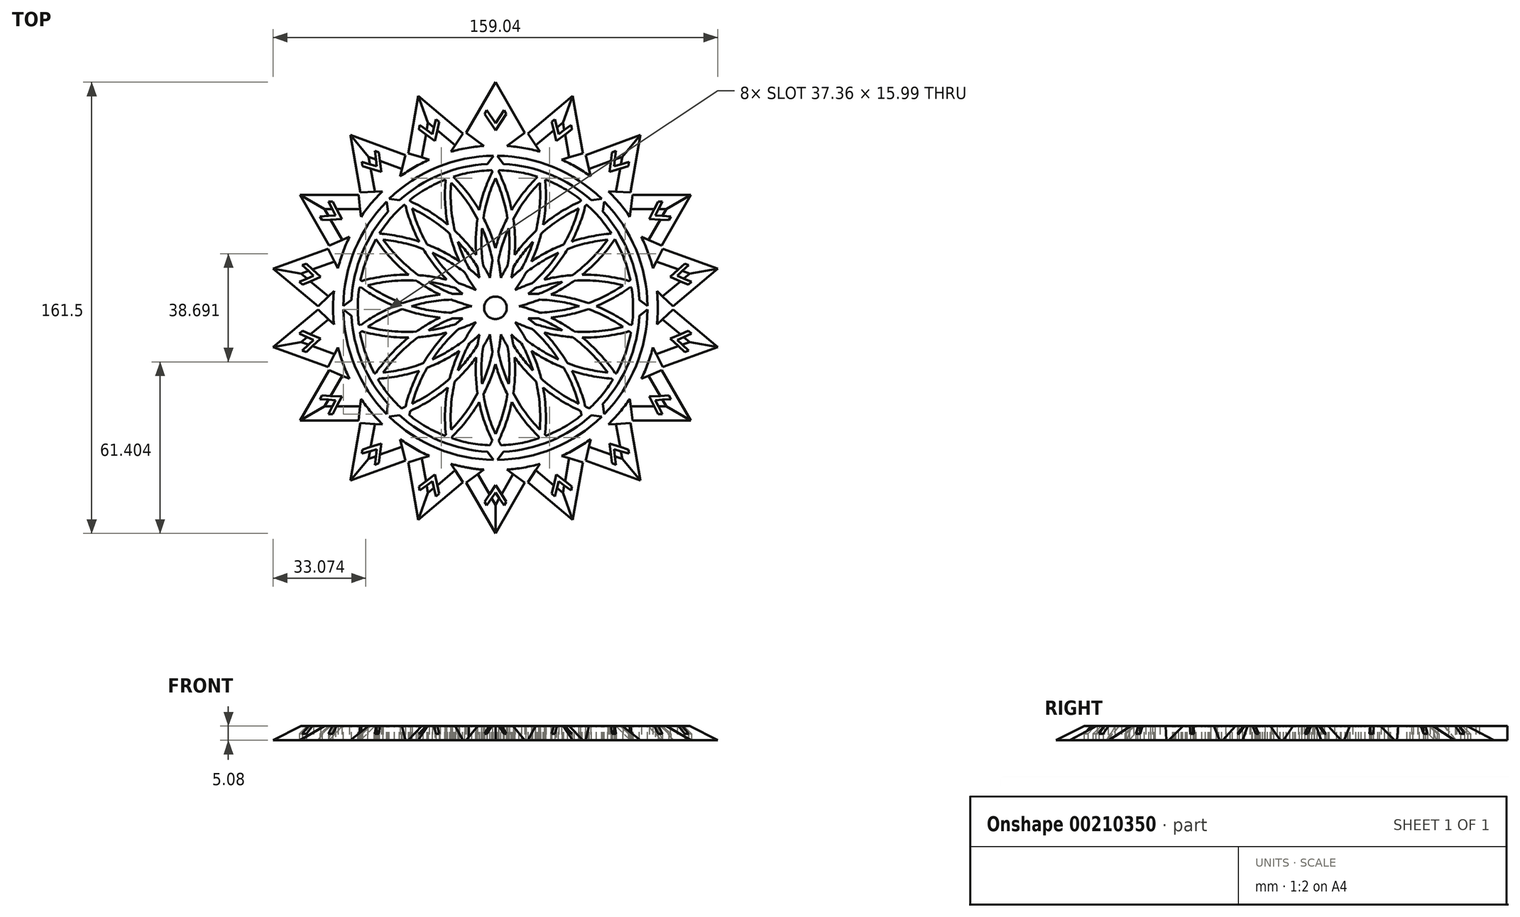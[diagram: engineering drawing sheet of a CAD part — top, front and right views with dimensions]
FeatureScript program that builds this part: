
annotation { "Feature Type Name" : "Feature", "Feature Type Description" : "" }
export const myFeature = defineFeature(function(context is Context, id is Id, definition is map)
    precondition{}
    {
        {
            var Q0;
            Q0=qCreatedBy(makeId("Top.planeOp"),FACE);
            var sketch = newSketch(context, id + "F0", { "sketchPlane" : qUnion([Q0])});
            skLineSegment(sketch, "E0", {"start": v(0, 0) * mm, "end": v(0, 63.5) * mm});
            skLineSegment(sketch, "E1", {"start": v(4.14, 57.94) * mm, "end": v(10.44, 62.64) * mm});
            skLineSegment(sketch, "E2", {"start": v(10.44, 62.64) * mm, "end": v(0, 80.75) * mm});
            skLineSegment(sketch, "E3", {"start": v(0, 80.75) * mm, "end": v(-10.44, 62.64) * mm});
            skLineSegment(sketch, "E4", {"start": v(-10.44, 62.64) * mm, "end": v(-4.14, 57.94) * mm});
            skLineSegment(sketch, "E5", {"start": v(0, 63.5) * mm, "end": v(3.84, 69.42) * mm});
            skLineSegment(sketch, "E6", {"start": v(3.08, 70.74) * mm, "end": v(0, 66.1) * mm});
            skLineSegment(sketch, "E7", {"start": v(0, 66.1) * mm, "end": v(-3.08, 70.74) * mm});
            skLineSegment(sketch, "E8", {"start": v(-3.84, 69.42) * mm, "end": v(0, 63.5) * mm});
            skLineSegment(sketch, "E9", {"start": v(0, 66.1) * mm, "end": v(0, 71.75) * mm});
            skLineSegment(sketch, "E10", {"start": v(-3.08, 70.74) * mm, "end": v(-3.84, 69.42) * mm});
            skLineSegment(sketch, "E11", {"start": v(3.08, 70.74) * mm, "end": v(3.84, 69.42) * mm});
            skLineSegment(sketch, "E12.1.0", {"start": v(31.24, 55.29) * mm, "end": v(27.62, 75.88) * mm});
            skLineSegment(sketch, "E12.1.1", {"start": v(27.62, 75.88) * mm, "end": v(11.6, 62.43) * mm});
            skLineSegment(sketch, "E12.1.2", {"start": v(22.61, 62.12) * mm, "end": v(21.3, 67.53) * mm});
            skLineSegment(sketch, "E12.1.3", {"start": v(21.3, 67.53) * mm, "end": v(20.13, 66.55) * mm});
            skLineSegment(sketch, "E12.1.4", {"start": v(20.13, 66.55) * mm, "end": v(21.72, 59.67) * mm});
            skLineSegment(sketch, "E12.1.5", {"start": v(21.72, 59.67) * mm, "end": v(27.35, 63.92) * mm});
            skLineSegment(sketch, "E12.1.6", {"start": v(27.09, 65.43) * mm, "end": v(27.35, 63.92) * mm});
            skLineSegment(sketch, "E12.1.7", {"start": v(27.09, 65.43) * mm, "end": v(22.61, 62.12) * mm});
            skLineSegment(sketch, "E12.1.10", {"start": v(11.6, 62.43) * mm, "end": v(15.93, 55.86) * mm});
            skLineSegment(sketch, "E12.1.11", {"start": v(23.7, 53.03) * mm, "end": v(31.24, 55.29) * mm});
            skLineSegment(sketch, "E12.2.0", {"start": v(48.26, 41.27) * mm, "end": v(51.9, 61.86) * mm});
            skLineSegment(sketch, "E12.2.1", {"start": v(51.9, 61.86) * mm, "end": v(32.26, 54.7) * mm});
            skLineSegment(sketch, "E12.2.2", {"start": v(42.5, 50.64) * mm, "end": v(43.12, 56.17) * mm});
            skLineSegment(sketch, "E12.2.3", {"start": v(43.12, 56.17) * mm, "end": v(41.68, 55.65) * mm});
            skLineSegment(sketch, "E12.2.4", {"start": v(41.68, 55.65) * mm, "end": v(40.82, 48.64) * mm});
            skLineSegment(sketch, "E12.2.5", {"start": v(40.82, 48.64) * mm, "end": v(47.56, 50.7) * mm});
            skLineSegment(sketch, "E12.2.6", {"start": v(47.83, 52.22) * mm, "end": v(47.56, 50.7) * mm});
            skLineSegment(sketch, "E12.2.7", {"start": v(47.83, 52.22) * mm, "end": v(42.5, 50.64) * mm});
            skLineSegment(sketch, "E12.2.10", {"start": v(32.26, 54.7) * mm, "end": v(34.07, 47.05) * mm});
            skLineSegment(sketch, "E12.2.11", {"start": v(40.41, 41.73) * mm, "end": v(48.26, 41.27) * mm});
            skLineSegment(sketch, "E12.3.0", {"start": v(59.47, 22.27) * mm, "end": v(69.93, 40.37) * mm});
            skLineSegment(sketch, "E12.3.1", {"start": v(69.93, 40.37) * mm, "end": v(49.02, 40.36) * mm});
            skLineSegment(sketch, "E12.3.2", {"start": v(57.25, 33.05) * mm, "end": v(59.73, 38.04) * mm});
            skLineSegment(sketch, "E12.3.3", {"start": v(59.73, 38.04) * mm, "end": v(58.2, 38.04) * mm});
            skLineSegment(sketch, "E12.3.4", {"start": v(58.2, 38.04) * mm, "end": v(55, 31.75) * mm});
            skLineSegment(sketch, "E12.3.5", {"start": v(55, 31.75) * mm, "end": v(62.04, 31.38) * mm});
            skLineSegment(sketch, "E12.3.6", {"start": v(62.8, 32.7) * mm, "end": v(62.04, 31.38) * mm});
            skLineSegment(sketch, "E12.3.7", {"start": v(62.8, 32.7) * mm, "end": v(57.25, 33.05) * mm});
            skLineSegment(sketch, "E12.3.10", {"start": v(49.02, 40.36) * mm, "end": v(48.1, 32.56) * mm});
            skLineSegment(sketch, "E12.3.11", {"start": v(52.25, 25.39) * mm, "end": v(59.47, 22.27) * mm});
            skLineSegment(sketch, "E12.4.0", {"start": v(63.5, 0.6) * mm, "end": v(79.52, 14.02) * mm});
            skLineSegment(sketch, "E12.4.1", {"start": v(79.52, 14.02) * mm, "end": v(59.87, 21.16) * mm});
            skLineSegment(sketch, "E12.4.2", {"start": v(65.1, 11.48) * mm, "end": v(69.14, 15.31) * mm});
            skLineSegment(sketch, "E12.4.3", {"start": v(69.14, 15.31) * mm, "end": v(67.7, 15.84) * mm});
            skLineSegment(sketch, "E12.4.4", {"start": v(67.7, 15.84) * mm, "end": v(62.54, 11.03) * mm});
            skLineSegment(sketch, "E12.4.5", {"start": v(62.54, 11.03) * mm, "end": v(69.03, 8.27) * mm});
            skLineSegment(sketch, "E12.4.6", {"start": v(70.2, 9.26) * mm, "end": v(69.03, 8.27) * mm});
            skLineSegment(sketch, "E12.4.7", {"start": v(70.2, 9.26) * mm, "end": v(65.1, 11.48) * mm});
            skLineSegment(sketch, "E12.4.10", {"start": v(59.87, 21.16) * mm, "end": v(56.34, 14.14) * mm});
            skLineSegment(sketch, "E12.4.11", {"start": v(57.78, 5.99) * mm, "end": v(63.5, 0.6) * mm});
            skLineSegment(sketch, "E12.5.0", {"start": v(59.87, -21.16) * mm, "end": v(79.52, -14.02) * mm});
            skLineSegment(sketch, "E12.5.1", {"start": v(79.52, -14.02) * mm, "end": v(63.5, -0.6) * mm});
            skLineSegment(sketch, "E12.5.2", {"start": v(65.1, -11.48) * mm, "end": v(70.2, -9.26) * mm});
            skLineSegment(sketch, "E12.5.3", {"start": v(70.2, -9.26) * mm, "end": v(69.03, -8.27) * mm});
            skLineSegment(sketch, "E12.5.4", {"start": v(69.03, -8.27) * mm, "end": v(62.54, -11.03) * mm});
            skLineSegment(sketch, "E12.5.5", {"start": v(62.54, -11.03) * mm, "end": v(67.7, -15.84) * mm});
            skLineSegment(sketch, "E12.5.6", {"start": v(69.14, -15.31) * mm, "end": v(67.7, -15.84) * mm});
            skLineSegment(sketch, "E12.5.7", {"start": v(69.14, -15.31) * mm, "end": v(65.1, -11.48) * mm});
            skLineSegment(sketch, "E12.5.10", {"start": v(63.5, -0.6) * mm, "end": v(57.78, -5.98) * mm});
            skLineSegment(sketch, "E12.5.11", {"start": v(56.34, -14.14) * mm, "end": v(59.87, -21.16) * mm});
            skLineSegment(sketch, "E12.6.0", {"start": v(49.02, -40.36) * mm, "end": v(69.93, -40.37) * mm});
            skLineSegment(sketch, "E12.6.1", {"start": v(69.93, -40.37) * mm, "end": v(59.47, -22.27) * mm});
            skLineSegment(sketch, "E12.6.2", {"start": v(57.25, -33.05) * mm, "end": v(62.8, -32.7) * mm});
            skLineSegment(sketch, "E12.6.3", {"start": v(62.8, -32.7) * mm, "end": v(62.04, -31.38) * mm});
            skLineSegment(sketch, "E12.6.4", {"start": v(62.04, -31.38) * mm, "end": v(55, -31.75) * mm});
            skLineSegment(sketch, "E12.6.5", {"start": v(55, -31.75) * mm, "end": v(58.2, -38.04) * mm});
            skLineSegment(sketch, "E12.6.6", {"start": v(59.73, -38.04) * mm, "end": v(58.2, -38.04) * mm});
            skLineSegment(sketch, "E12.6.7", {"start": v(59.73, -38.04) * mm, "end": v(57.25, -33.05) * mm});
            skLineSegment(sketch, "E12.6.10", {"start": v(59.47, -22.27) * mm, "end": v(52.25, -25.39) * mm});
            skLineSegment(sketch, "E12.6.11", {"start": v(48.1, -32.56) * mm, "end": v(49.02, -40.36) * mm});
            skLineSegment(sketch, "E12.7.0", {"start": v(32.26, -54.7) * mm, "end": v(51.9, -61.86) * mm});
            skLineSegment(sketch, "E12.7.1", {"start": v(51.9, -61.86) * mm, "end": v(48.26, -41.27) * mm});
            skLineSegment(sketch, "E12.7.2", {"start": v(42.5, -50.64) * mm, "end": v(47.83, -52.22) * mm});
            skLineSegment(sketch, "E12.7.3", {"start": v(47.83, -52.22) * mm, "end": v(47.56, -50.7) * mm});
            skLineSegment(sketch, "E12.7.4", {"start": v(47.56, -50.7) * mm, "end": v(40.82, -48.64) * mm});
            skLineSegment(sketch, "E12.7.5", {"start": v(40.82, -48.64) * mm, "end": v(41.68, -55.65) * mm});
            skLineSegment(sketch, "E12.7.6", {"start": v(43.12, -56.17) * mm, "end": v(41.68, -55.65) * mm});
            skLineSegment(sketch, "E12.7.7", {"start": v(43.12, -56.17) * mm, "end": v(42.5, -50.64) * mm});
            skLineSegment(sketch, "E12.7.10", {"start": v(48.26, -41.27) * mm, "end": v(40.42, -41.72) * mm});
            skLineSegment(sketch, "E12.7.11", {"start": v(34.07, -47.05) * mm, "end": v(32.26, -54.7) * mm});
            skLineSegment(sketch, "E12.8.0", {"start": v(11.6, -62.43) * mm, "end": v(27.62, -75.88) * mm});
            skLineSegment(sketch, "E12.8.1", {"start": v(27.62, -75.88) * mm, "end": v(31.24, -55.29) * mm});
            skLineSegment(sketch, "E12.8.2", {"start": v(22.61, -62.12) * mm, "end": v(27.09, -65.43) * mm});
            skLineSegment(sketch, "E12.8.3", {"start": v(27.09, -65.43) * mm, "end": v(27.35, -63.92) * mm});
            skLineSegment(sketch, "E12.8.4", {"start": v(27.35, -63.92) * mm, "end": v(21.72, -59.67) * mm});
            skLineSegment(sketch, "E12.8.5", {"start": v(21.72, -59.67) * mm, "end": v(20.13, -66.55) * mm});
            skLineSegment(sketch, "E12.8.6", {"start": v(21.3, -67.53) * mm, "end": v(20.13, -66.55) * mm});
            skLineSegment(sketch, "E12.8.7", {"start": v(21.3, -67.53) * mm, "end": v(22.61, -62.12) * mm});
            skLineSegment(sketch, "E12.8.10", {"start": v(31.24, -55.29) * mm, "end": v(23.7, -53.03) * mm});
            skLineSegment(sketch, "E12.8.11", {"start": v(15.93, -55.86) * mm, "end": v(11.6, -62.43) * mm});
            skLineSegment(sketch, "E12.9.0", {"start": v(-10.44, -62.64) * mm, "end": v(0, -80.75) * mm});
            skLineSegment(sketch, "E12.9.1", {"start": v(0, -80.75) * mm, "end": v(10.44, -62.64) * mm});
            skLineSegment(sketch, "E12.9.2", {"start": v(0, -66.1) * mm, "end": v(3.08, -70.74) * mm});
            skLineSegment(sketch, "E12.9.3", {"start": v(3.08, -70.74) * mm, "end": v(3.84, -69.42) * mm});
            skLineSegment(sketch, "E12.9.4", {"start": v(3.84, -69.42) * mm, "end": v(0, -63.5) * mm});
            skLineSegment(sketch, "E12.9.5", {"start": v(0, -63.5) * mm, "end": v(-3.84, -69.42) * mm});
            skLineSegment(sketch, "E12.9.6", {"start": v(-3.08, -70.74) * mm, "end": v(-3.84, -69.42) * mm});
            skLineSegment(sketch, "E12.9.7", {"start": v(-3.08, -70.74) * mm, "end": v(0, -66.1) * mm});
            skLineSegment(sketch, "E12.9.10", {"start": v(10.44, -62.64) * mm, "end": v(4.14, -57.94) * mm});
            skLineSegment(sketch, "E12.9.11", {"start": v(-4.14, -57.94) * mm, "end": v(-10.44, -62.64) * mm});
            skPoint(sketch, "E12.center", {"position": v(0, 0) * mm});
            skLineSegment(sketch, "E12.anchor1", {"start": v(0, 0) * mm, "end": v(10.44, 62.64) * mm, "construction": true});
            skLineSegment(sketch, "E12.anchor2", {"start": v(0, 0) * mm, "end": v(-10.44, -62.64) * mm, "construction": true});
            skLineSegment(sketch, "E13.1.0", {"start": v(-27.62, -75.88) * mm, "end": v(-11.6, -62.43) * mm});
            skLineSegment(sketch, "E13.1.1", {"start": v(-31.24, -55.29) * mm, "end": v(-27.62, -75.88) * mm});
            skLineSegment(sketch, "E13.1.2", {"start": v(-23.7, -53.03) * mm, "end": v(-31.24, -55.29) * mm});
            skLineSegment(sketch, "E13.1.5", {"start": v(-11.6, -62.43) * mm, "end": v(-15.93, -55.86) * mm});
            skLineSegment(sketch, "E13.1.6", {"start": v(-20.13, -66.55) * mm, "end": v(-21.72, -59.67) * mm});
            skLineSegment(sketch, "E13.1.7", {"start": v(-21.72, -59.67) * mm, "end": v(-27.35, -63.92) * mm});
            skLineSegment(sketch, "E13.1.8", {"start": v(-27.09, -65.43) * mm, "end": v(-27.35, -63.92) * mm});
            skLineSegment(sketch, "E13.1.9", {"start": v(-27.09, -65.43) * mm, "end": v(-22.61, -62.12) * mm});
            skLineSegment(sketch, "E13.1.10", {"start": v(-22.61, -62.12) * mm, "end": v(-21.3, -67.53) * mm});
            skLineSegment(sketch, "E13.1.11", {"start": v(-21.3, -67.53) * mm, "end": v(-20.13, -66.55) * mm});
            skLineSegment(sketch, "E13.2.0", {"start": v(-51.9, -61.86) * mm, "end": v(-32.26, -54.7) * mm});
            skLineSegment(sketch, "E13.2.1", {"start": v(-48.26, -41.27) * mm, "end": v(-51.9, -61.86) * mm});
            skLineSegment(sketch, "E13.2.2", {"start": v(-40.41, -41.73) * mm, "end": v(-48.26, -41.27) * mm});
            skLineSegment(sketch, "E13.2.5", {"start": v(-32.26, -54.7) * mm, "end": v(-34.07, -47.05) * mm});
            skLineSegment(sketch, "E13.2.6", {"start": v(-41.68, -55.65) * mm, "end": v(-40.82, -48.64) * mm});
            skLineSegment(sketch, "E13.2.7", {"start": v(-40.82, -48.64) * mm, "end": v(-47.56, -50.7) * mm});
            skLineSegment(sketch, "E13.2.8", {"start": v(-47.83, -52.22) * mm, "end": v(-47.56, -50.7) * mm});
            skLineSegment(sketch, "E13.2.9", {"start": v(-47.83, -52.22) * mm, "end": v(-42.5, -50.64) * mm});
            skLineSegment(sketch, "E13.2.10", {"start": v(-42.5, -50.64) * mm, "end": v(-43.12, -56.17) * mm});
            skLineSegment(sketch, "E13.2.11", {"start": v(-43.12, -56.17) * mm, "end": v(-41.68, -55.65) * mm});
            skLineSegment(sketch, "E13.3.0", {"start": v(-69.93, -40.37) * mm, "end": v(-49.02, -40.36) * mm});
            skLineSegment(sketch, "E13.3.1", {"start": v(-59.47, -22.27) * mm, "end": v(-69.93, -40.37) * mm});
            skLineSegment(sketch, "E13.3.2", {"start": v(-52.25, -25.39) * mm, "end": v(-59.47, -22.27) * mm});
            skLineSegment(sketch, "E13.3.5", {"start": v(-49.02, -40.36) * mm, "end": v(-48.1, -32.56) * mm});
            skLineSegment(sketch, "E13.3.6", {"start": v(-58.2, -38.04) * mm, "end": v(-55, -31.75) * mm});
            skLineSegment(sketch, "E13.3.7", {"start": v(-55, -31.75) * mm, "end": v(-62.04, -31.38) * mm});
            skLineSegment(sketch, "E13.3.8", {"start": v(-62.8, -32.7) * mm, "end": v(-62.04, -31.38) * mm});
            skLineSegment(sketch, "E13.3.9", {"start": v(-62.8, -32.7) * mm, "end": v(-57.25, -33.05) * mm});
            skLineSegment(sketch, "E13.3.10", {"start": v(-57.25, -33.05) * mm, "end": v(-59.73, -38.04) * mm});
            skLineSegment(sketch, "E13.3.11", {"start": v(-59.73, -38.04) * mm, "end": v(-58.2, -38.04) * mm});
            skLineSegment(sketch, "E13.4.0", {"start": v(-79.52, -14.02) * mm, "end": v(-59.87, -21.16) * mm});
            skLineSegment(sketch, "E13.4.1", {"start": v(-63.5, -0.6) * mm, "end": v(-79.52, -14.02) * mm});
            skLineSegment(sketch, "E13.4.2", {"start": v(-57.78, -5.99) * mm, "end": v(-63.5, -0.6) * mm});
            skLineSegment(sketch, "E13.4.5", {"start": v(-59.87, -21.16) * mm, "end": v(-56.34, -14.14) * mm});
            skLineSegment(sketch, "E13.4.6", {"start": v(-67.7, -15.84) * mm, "end": v(-62.54, -11.03) * mm});
            skLineSegment(sketch, "E13.4.7", {"start": v(-62.54, -11.03) * mm, "end": v(-69.03, -8.27) * mm});
            skLineSegment(sketch, "E13.4.8", {"start": v(-70.2, -9.26) * mm, "end": v(-69.03, -8.27) * mm});
            skLineSegment(sketch, "E13.4.9", {"start": v(-70.2, -9.26) * mm, "end": v(-65.1, -11.48) * mm});
            skLineSegment(sketch, "E13.4.10", {"start": v(-65.1, -11.48) * mm, "end": v(-69.14, -15.31) * mm});
            skLineSegment(sketch, "E13.4.11", {"start": v(-69.14, -15.31) * mm, "end": v(-67.7, -15.84) * mm});
            skLineSegment(sketch, "E13.5.0", {"start": v(-79.52, 14.02) * mm, "end": v(-63.5, 0.6) * mm});
            skLineSegment(sketch, "E13.5.1", {"start": v(-59.87, 21.16) * mm, "end": v(-79.52, 14.02) * mm});
            skLineSegment(sketch, "E13.5.2", {"start": v(-56.34, 14.14) * mm, "end": v(-59.87, 21.16) * mm});
            skLineSegment(sketch, "E13.5.5", {"start": v(-63.5, 0.6) * mm, "end": v(-57.78, 5.98) * mm});
            skLineSegment(sketch, "E13.5.6", {"start": v(-69.03, 8.27) * mm, "end": v(-62.54, 11.03) * mm});
            skLineSegment(sketch, "E13.5.7", {"start": v(-62.54, 11.03) * mm, "end": v(-67.7, 15.84) * mm});
            skLineSegment(sketch, "E13.5.8", {"start": v(-69.14, 15.31) * mm, "end": v(-67.7, 15.84) * mm});
            skLineSegment(sketch, "E13.5.9", {"start": v(-69.14, 15.31) * mm, "end": v(-65.1, 11.48) * mm});
            skLineSegment(sketch, "E13.5.10", {"start": v(-65.1, 11.48) * mm, "end": v(-70.2, 9.26) * mm});
            skLineSegment(sketch, "E13.5.11", {"start": v(-70.2, 9.26) * mm, "end": v(-69.03, 8.27) * mm});
            skLineSegment(sketch, "E13.6.0", {"start": v(-69.93, 40.37) * mm, "end": v(-59.47, 22.27) * mm});
            skLineSegment(sketch, "E13.6.1", {"start": v(-49.02, 40.36) * mm, "end": v(-69.93, 40.37) * mm});
            skLineSegment(sketch, "E13.6.2", {"start": v(-48.1, 32.56) * mm, "end": v(-49.02, 40.36) * mm});
            skLineSegment(sketch, "E13.6.5", {"start": v(-59.47, 22.27) * mm, "end": v(-52.25, 25.39) * mm});
            skLineSegment(sketch, "E13.6.6", {"start": v(-62.04, 31.38) * mm, "end": v(-55, 31.75) * mm});
            skLineSegment(sketch, "E13.6.7", {"start": v(-55, 31.75) * mm, "end": v(-58.2, 38.04) * mm});
            skLineSegment(sketch, "E13.6.8", {"start": v(-59.73, 38.04) * mm, "end": v(-58.2, 38.04) * mm});
            skLineSegment(sketch, "E13.6.9", {"start": v(-59.73, 38.04) * mm, "end": v(-57.25, 33.05) * mm});
            skLineSegment(sketch, "E13.6.10", {"start": v(-57.25, 33.05) * mm, "end": v(-62.8, 32.7) * mm});
            skLineSegment(sketch, "E13.6.11", {"start": v(-62.8, 32.7) * mm, "end": v(-62.04, 31.38) * mm});
            skLineSegment(sketch, "E13.7.0", {"start": v(-51.9, 61.86) * mm, "end": v(-48.26, 41.27) * mm});
            skLineSegment(sketch, "E13.7.1", {"start": v(-32.26, 54.7) * mm, "end": v(-51.9, 61.86) * mm});
            skLineSegment(sketch, "E13.7.2", {"start": v(-34.07, 47.05) * mm, "end": v(-32.26, 54.7) * mm});
            skLineSegment(sketch, "E13.7.5", {"start": v(-48.26, 41.27) * mm, "end": v(-40.42, 41.72) * mm});
            skLineSegment(sketch, "E13.7.6", {"start": v(-47.56, 50.7) * mm, "end": v(-40.82, 48.64) * mm});
            skLineSegment(sketch, "E13.7.7", {"start": v(-40.82, 48.64) * mm, "end": v(-41.68, 55.65) * mm});
            skLineSegment(sketch, "E13.7.8", {"start": v(-43.12, 56.17) * mm, "end": v(-41.68, 55.65) * mm});
            skLineSegment(sketch, "E13.7.9", {"start": v(-43.12, 56.17) * mm, "end": v(-42.5, 50.64) * mm});
            skLineSegment(sketch, "E13.7.10", {"start": v(-42.5, 50.64) * mm, "end": v(-47.83, 52.22) * mm});
            skLineSegment(sketch, "E13.7.11", {"start": v(-47.83, 52.22) * mm, "end": v(-47.56, 50.7) * mm});
            skLineSegment(sketch, "E13.8.0", {"start": v(-27.62, 75.88) * mm, "end": v(-31.24, 55.29) * mm});
            skLineSegment(sketch, "E13.8.1", {"start": v(-11.6, 62.43) * mm, "end": v(-27.62, 75.88) * mm});
            skLineSegment(sketch, "E13.8.2", {"start": v(-15.93, 55.86) * mm, "end": v(-11.6, 62.43) * mm});
            skLineSegment(sketch, "E13.8.5", {"start": v(-31.24, 55.29) * mm, "end": v(-23.7, 53.03) * mm});
            skLineSegment(sketch, "E13.8.6", {"start": v(-27.35, 63.92) * mm, "end": v(-21.72, 59.67) * mm});
            skLineSegment(sketch, "E13.8.7", {"start": v(-21.72, 59.67) * mm, "end": v(-20.13, 66.55) * mm});
            skLineSegment(sketch, "E13.8.8", {"start": v(-21.3, 67.53) * mm, "end": v(-20.13, 66.55) * mm});
            skLineSegment(sketch, "E13.8.9", {"start": v(-21.3, 67.53) * mm, "end": v(-22.61, 62.12) * mm});
            skLineSegment(sketch, "E13.8.10", {"start": v(-22.61, 62.12) * mm, "end": v(-27.09, 65.43) * mm});
            skLineSegment(sketch, "E13.8.11", {"start": v(-27.09, 65.43) * mm, "end": v(-27.35, 63.92) * mm});
            skLineSegment(sketch, "E13.anchor1", {"start": v(0, 0) * mm, "end": v(0, -80.75) * mm, "construction": true});
            skLineSegment(sketch, "E13.anchor2", {"start": v(0, 0) * mm, "end": v(0, 80.75) * mm, "construction": true});
            skArc(sketch, "E14", {"start": v(-56.34, -14.14) * mm, "mid": v(-54.59, -19.87) * mm, "end": v(-52.25, -25.39) * mm});
            skCircle(sketch, "E15", {"center": v(0, 0) * mm, "radius": 53.43 * mm});
            skArc(sketch, "E16.trimOffspring", {"start": v(10.44, -62.64) * mm, "mid": v(11.03, -62.54) * mm, "end": v(11.6, -62.43) * mm});
            skArc(sketch, "E17.trimOffspring", {"start": v(59.87, 21.16) * mm, "mid": v(59.67, 21.72) * mm, "end": v(59.47, 22.27) * mm});
            skArc(sketch, "E18.trimOffspring", {"start": v(-10.44, 62.64) * mm, "mid": v(-11.03, 62.54) * mm, "end": v(-11.6, 62.43) * mm});
            skArc(sketch, "E19.trimOffspring", {"start": v(-59.47, 22.27) * mm, "mid": v(-59.67, 21.72) * mm, "end": v(-59.87, 21.16) * mm});
            skArc(sketch, "E20.trimOffspring", {"start": v(-57.78, 5.98) * mm, "mid": v(-58.09, 0) * mm, "end": v(-57.78, -5.99) * mm});
            skArc(sketch, "E21.trimOffspring", {"start": v(-52.25, 25.39) * mm, "mid": v(-54.59, 19.87) * mm, "end": v(-56.34, 14.14) * mm});
            skArc(sketch, "E22.trimOffspring", {"start": v(-48.1, -32.56) * mm, "mid": v(-44.5, -37.34) * mm, "end": v(-40.41, -41.73) * mm});
            skArc(sketch, "E23.trimOffspring", {"start": v(-34.07, -47.05) * mm, "mid": v(-29.04, -50.3) * mm, "end": v(-23.7, -53.03) * mm});
            skArc(sketch, "E24.trimOffspring", {"start": v(-40.42, 41.72) * mm, "mid": v(-44.5, 37.34) * mm, "end": v(-48.1, 32.56) * mm});
            skArc(sketch, "E25.trimOffspring", {"start": v(-23.7, 53.03) * mm, "mid": v(-29.04, 50.3) * mm, "end": v(-34.07, 47.05) * mm});
            skArc(sketch, "E26.trimOffspring", {"start": v(-4.14, 57.94) * mm, "mid": v(-10.09, 57.2) * mm, "end": v(-15.93, 55.86) * mm});
            skArc(sketch, "E27.trimOffspring", {"start": v(15.93, 55.86) * mm, "mid": v(10.09, 57.2) * mm, "end": v(4.14, 57.94) * mm});
            skArc(sketch, "E28.trimOffspring", {"start": v(-15.93, -55.86) * mm, "mid": v(-12.76, -56.67) * mm, "end": v(-9.55, -57.3) * mm});
            skArc(sketch, "E29.trimOffspring", {"start": v(4.14, -57.94) * mm, "mid": v(10.09, -57.2) * mm, "end": v(15.93, -55.86) * mm});
            skArc(sketch, "E30.trimOffspring", {"start": v(23.7, -53.03) * mm, "mid": v(29.04, -50.3) * mm, "end": v(34.07, -47.05) * mm});
            skArc(sketch, "E31.trimOffspring", {"start": v(40.42, -41.72) * mm, "mid": v(44.5, -37.34) * mm, "end": v(48.1, -32.56) * mm});
            skArc(sketch, "E32.trimOffspring", {"start": v(52.25, -25.39) * mm, "mid": v(54.59, -19.87) * mm, "end": v(56.34, -14.14) * mm});
            skArc(sketch, "E33.trimOffspring", {"start": v(57.78, -5.98) * mm, "mid": v(58.09, 0) * mm, "end": v(57.78, 5.99) * mm});
            skArc(sketch, "E34.trimOffspring", {"start": v(56.34, 14.14) * mm, "mid": v(54.59, 19.87) * mm, "end": v(52.25, 25.39) * mm});
            skArc(sketch, "E35.trimOffspring", {"start": v(48.1, 32.56) * mm, "mid": v(44.5, 37.34) * mm, "end": v(40.41, 41.73) * mm});
            skArc(sketch, "E36.trimOffspring", {"start": v(34.07, 47.05) * mm, "mid": v(29.04, 50.3) * mm, "end": v(23.7, 53.03) * mm});
            skArc(sketch, "E37", {"start": v(-9.55, -57.3) * mm, "mid": v(-6.86, -57.72) * mm, "end": v(-4.14, -57.94) * mm});
            skSolve(sketch);
        }
        {
            var Q0;
            Q0=makeQuery(id+"F0.imprint","IMPRINT",FACE,{"disambiguationData":[TD([[makeQuery(id+"F0.imprint","IMPRINT",EDGE,{"derivedFrom":sQuery(id+"F0.wireOp",EDGE,"E12.1.0")}),1.0]])]});
            extrude(context, id + "F1", {"entities" : qUnion([Q0]), "depth" : 5.08 * mm});
        }
        {
            var Q0;
            Q0=makeQuery(id+"F1.opExtrude","CAP_EDGE",EDGE,{"disambiguationData":[OSD([sQuery(id+"F0.wireOp",EDGE,"E13.2.1")])],"isStart":false});
            var Q1;
            Q1=makeQuery(id+"F1.opExtrude","CAP_EDGE",EDGE,{"disambiguationData":[OSD([sQuery(id+"F0.wireOp",EDGE,"E13.2.0")])],"isStart":false});
            var Q2;
            Q2=makeQuery(id+"F1.opExtrude","CAP_EDGE",EDGE,{"disambiguationData":[OSD([sQuery(id+"F0.wireOp",EDGE,"E13.1.1")])],"isStart":false});
            var Q3;
            Q3=makeQuery(id+"F1.opExtrude","CAP_EDGE",EDGE,{"disambiguationData":[OSD([sQuery(id+"F0.wireOp",EDGE,"E13.1.0")])],"isStart":false});
            var Q4;
            Q4=makeQuery(id+"F1.opExtrude","CAP_EDGE",EDGE,{"disambiguationData":[OSD([sQuery(id+"F0.wireOp",EDGE,"E12.9.0")])],"isStart":false});
            var Q5;
            Q5=makeQuery(id+"F1.opExtrude","CAP_EDGE",EDGE,{"disambiguationData":[OSD([sQuery(id+"F0.wireOp",EDGE,"E12.9.1")])],"isStart":false});
            var Q6;
            Q6=makeQuery(id+"F1.opExtrude","CAP_EDGE",EDGE,{"disambiguationData":[OSD([sQuery(id+"F0.wireOp",EDGE,"E12.8.0")])],"isStart":false});
            var Q7;
            Q7=makeQuery(id+"F1.opExtrude","CAP_EDGE",EDGE,{"disambiguationData":[OSD([sQuery(id+"F0.wireOp",EDGE,"E12.8.1")])],"isStart":false});
            var Q8;
            Q8=makeQuery(id+"F1.opExtrude","CAP_EDGE",EDGE,{"disambiguationData":[OSD([sQuery(id+"F0.wireOp",EDGE,"E12.7.0")])],"isStart":false});
            var Q9;
            Q9=makeQuery(id+"F1.opExtrude","CAP_EDGE",EDGE,{"disambiguationData":[OSD([sQuery(id+"F0.wireOp",EDGE,"E12.7.1")])],"isStart":false});
            var Q10;
            Q10=makeQuery(id+"F1.opExtrude","CAP_EDGE",EDGE,{"disambiguationData":[OSD([sQuery(id+"F0.wireOp",EDGE,"E12.6.0")])],"isStart":false});
            var Q11;
            Q11=makeQuery(id+"F1.opExtrude","CAP_EDGE",EDGE,{"disambiguationData":[OSD([sQuery(id+"F0.wireOp",EDGE,"E12.6.1")])],"isStart":false});
            var Q12;
            Q12=makeQuery(id+"F1.opExtrude","CAP_EDGE",EDGE,{"disambiguationData":[OSD([sQuery(id+"F0.wireOp",EDGE,"E12.5.0")])],"isStart":false});
            var Q13;
            Q13=makeQuery(id+"F1.opExtrude","CAP_EDGE",EDGE,{"disambiguationData":[OSD([sQuery(id+"F0.wireOp",EDGE,"E12.5.1")])],"isStart":false});
            var Q14;
            Q14=makeQuery(id+"F1.opExtrude","CAP_EDGE",EDGE,{"disambiguationData":[OSD([sQuery(id+"F0.wireOp",EDGE,"E12.4.0")])],"isStart":false});
            var Q15;
            Q15=makeQuery(id+"F1.opExtrude","CAP_EDGE",EDGE,{"disambiguationData":[OSD([sQuery(id+"F0.wireOp",EDGE,"E12.4.1")])],"isStart":false});
            var Q16;
            Q16=makeQuery(id+"F1.opExtrude","CAP_EDGE",EDGE,{"disambiguationData":[OSD([sQuery(id+"F0.wireOp",EDGE,"E3")])],"isStart":false});
            var Q17;
            Q17=makeQuery(id+"F1.opExtrude","CAP_EDGE",EDGE,{"disambiguationData":[OSD([sQuery(id+"F0.wireOp",EDGE,"E13.8.1")])],"isStart":false});
            var Q18;
            Q18=makeQuery(id+"F1.opExtrude","CAP_EDGE",EDGE,{"disambiguationData":[OSD([sQuery(id+"F0.wireOp",EDGE,"E13.8.0")])],"isStart":false});
            var Q19;
            Q19=makeQuery(id+"F1.opExtrude","CAP_EDGE",EDGE,{"disambiguationData":[OSD([sQuery(id+"F0.wireOp",EDGE,"E13.7.1")])],"isStart":false});
            var Q20;
            Q20=makeQuery(id+"F1.opExtrude","CAP_EDGE",EDGE,{"disambiguationData":[OSD([sQuery(id+"F0.wireOp",EDGE,"E13.7.0")])],"isStart":false});
            var Q21;
            Q21=makeQuery(id+"F1.opExtrude","CAP_EDGE",EDGE,{"disambiguationData":[OSD([sQuery(id+"F0.wireOp",EDGE,"E13.6.1")])],"isStart":false});
            var Q22;
            Q22=makeQuery(id+"F1.opExtrude","CAP_EDGE",EDGE,{"disambiguationData":[OSD([sQuery(id+"F0.wireOp",EDGE,"E13.6.0")])],"isStart":false});
            var Q23;
            Q23=makeQuery(id+"F1.opExtrude","CAP_EDGE",EDGE,{"disambiguationData":[OSD([sQuery(id+"F0.wireOp",EDGE,"E13.5.1")])],"isStart":false});
            var Q24;
            Q24=makeQuery(id+"F1.opExtrude","CAP_EDGE",EDGE,{"disambiguationData":[OSD([sQuery(id+"F0.wireOp",EDGE,"E13.5.0")])],"isStart":false});
            var Q25;
            Q25=makeQuery(id+"F1.opExtrude","CAP_EDGE",EDGE,{"disambiguationData":[OSD([sQuery(id+"F0.wireOp",EDGE,"E13.4.1")])],"isStart":false});
            var Q26;
            Q26=makeQuery(id+"F1.opExtrude","CAP_EDGE",EDGE,{"disambiguationData":[OSD([sQuery(id+"F0.wireOp",EDGE,"E13.4.0")])],"isStart":false});
            var Q27;
            Q27=makeQuery(id+"F1.opExtrude","CAP_EDGE",EDGE,{"disambiguationData":[OSD([sQuery(id+"F0.wireOp",EDGE,"E13.3.1")])],"isStart":false});
            var Q28;
            Q28=makeQuery(id+"F1.opExtrude","CAP_EDGE",EDGE,{"disambiguationData":[OSD([sQuery(id+"F0.wireOp",EDGE,"E13.3.0")])],"isStart":false});
            var Q29;
            Q29=makeQuery(id+"F1.opExtrude","CAP_EDGE",EDGE,{"disambiguationData":[OSD([sQuery(id+"F0.wireOp",EDGE,"E2")])],"isStart":false});
            var Q30;
            Q30=makeQuery(id+"F1.opExtrude","CAP_EDGE",EDGE,{"disambiguationData":[OSD([sQuery(id+"F0.wireOp",EDGE,"E12.1.1")])],"isStart":false});
            var Q31;
            Q31=makeQuery(id+"F1.opExtrude","CAP_EDGE",EDGE,{"disambiguationData":[OSD([sQuery(id+"F0.wireOp",EDGE,"E12.1.0")])],"isStart":false});
            var Q32;
            Q32=makeQuery(id+"F1.opExtrude","CAP_EDGE",EDGE,{"disambiguationData":[OSD([sQuery(id+"F0.wireOp",EDGE,"E12.2.1")])],"isStart":false});
            var Q33;
            Q33=makeQuery(id+"F1.opExtrude","CAP_EDGE",EDGE,{"disambiguationData":[OSD([sQuery(id+"F0.wireOp",EDGE,"E12.2.0")])],"isStart":false});
            var Q34;
            Q34=makeQuery(id+"F1.opExtrude","CAP_EDGE",EDGE,{"disambiguationData":[OSD([sQuery(id+"F0.wireOp",EDGE,"E12.3.1")])],"isStart":false});
            var Q35;
            Q35=makeQuery(id+"F1.opExtrude","CAP_EDGE",EDGE,{"disambiguationData":[OSD([sQuery(id+"F0.wireOp",EDGE,"E12.3.0")])],"isStart":false});
            chamfer(context, id + "F2", {"entities" : qUnion([Q0, Q1, Q2, Q3, Q4, Q5, Q6, Q7, Q8, Q9, Q10, Q11, Q12, Q13, Q14, Q15, Q16, Q17, Q18, Q19, Q20, Q21, Q22, Q23, Q24, Q25, Q26, Q27, Q28, Q29, Q30, Q31, Q32, Q33, Q34, Q35]), "width" : 5.08 * mm, "tangentPropagation" : true});
        }
        {
            var Q0;
            Q0=makeQuery(id+"F1.opExtrude","CAP_FACE",FACE,{"disambiguationData":[OSD([sQuery(id+"F0.wireOp",EDGE,"E12.1.0"),sQuery(id+"F0.wireOp",EDGE,"E12.1.1"),sQuery(id+"F0.wireOp",EDGE,"E12.1.2"),sQuery(id+"F0.wireOp",EDGE,"E12.1.3"),sQuery(id+"F0.wireOp",EDGE,"E12.1.4"),sQuery(id+"F0.wireOp",EDGE,"E12.1.5"),sQuery(id+"F0.wireOp",EDGE,"E12.1.6"),sQuery(id+"F0.wireOp",EDGE,"E12.1.7"),sQuery(id+"F0.wireOp",EDGE,"E12.1.10"),sQuery(id+"F0.wireOp",EDGE,"E12.1.11"),sQuery(id+"F0.wireOp",EDGE,"E12.2.0"),sQuery(id+"F0.wireOp",EDGE,"E12.2.1"),sQuery(id+"F0.wireOp",EDGE,"E12.2.2"),sQuery(id+"F0.wireOp",EDGE,"E12.2.3"),sQuery(id+"F0.wireOp",EDGE,"E12.2.4"),sQuery(id+"F0.wireOp",EDGE,"E12.2.5"),sQuery(id+"F0.wireOp",EDGE,"E12.2.6"),sQuery(id+"F0.wireOp",EDGE,"E12.2.7"),sQuery(id+"F0.wireOp",EDGE,"E12.2.10"),sQuery(id+"F0.wireOp",EDGE,"E12.2.11"),sQuery(id+"F0.wireOp",EDGE,"E12.3.0"),sQuery(id+"F0.wireOp",EDGE,"E12.3.1"),sQuery(id+"F0.wireOp",EDGE,"E12.3.2"),sQuery(id+"F0.wireOp",EDGE,"E12.3.3"),sQuery(id+"F0.wireOp",EDGE,"E12.3.4"),sQuery(id+"F0.wireOp",EDGE,"E12.3.5"),sQuery(id+"F0.wireOp",EDGE,"E12.3.6"),sQuery(id+"F0.wireOp",EDGE,"E12.3.7"),sQuery(id+"F0.wireOp",EDGE,"E12.3.10"),sQuery(id+"F0.wireOp",EDGE,"E12.3.11"),sQuery(id+"F0.wireOp",EDGE,"E12.4.0"),sQuery(id+"F0.wireOp",EDGE,"E12.4.1"),sQuery(id+"F0.wireOp",EDGE,"E12.4.2"),sQuery(id+"F0.wireOp",EDGE,"E12.4.3"),sQuery(id+"F0.wireOp",EDGE,"E12.4.4"),sQuery(id+"F0.wireOp",EDGE,"E12.4.5"),sQuery(id+"F0.wireOp",EDGE,"E12.4.6"),sQuery(id+"F0.wireOp",EDGE,"E12.4.7"),sQuery(id+"F0.wireOp",EDGE,"E12.4.10"),sQuery(id+"F0.wireOp",EDGE,"E12.4.11"),sQuery(id+"F0.wireOp",EDGE,"E12.5.0"),sQuery(id+"F0.wireOp",EDGE,"E12.5.1"),sQuery(id+"F0.wireOp",EDGE,"E12.5.2"),sQuery(id+"F0.wireOp",EDGE,"E12.5.3"),sQuery(id+"F0.wireOp",EDGE,"E12.5.4"),sQuery(id+"F0.wireOp",EDGE,"E12.5.5"),sQuery(id+"F0.wireOp",EDGE,"E12.5.6"),sQuery(id+"F0.wireOp",EDGE,"E12.5.7"),sQuery(id+"F0.wireOp",EDGE,"E12.5.10"),sQuery(id+"F0.wireOp",EDGE,"E12.5.11"),sQuery(id+"F0.wireOp",EDGE,"E12.6.0"),sQuery(id+"F0.wireOp",EDGE,"E12.6.1"),sQuery(id+"F0.wireOp",EDGE,"E12.6.2"),sQuery(id+"F0.wireOp",EDGE,"E12.6.3"),sQuery(id+"F0.wireOp",EDGE,"E12.6.4"),sQuery(id+"F0.wireOp",EDGE,"E12.6.5"),sQuery(id+"F0.wireOp",EDGE,"E12.6.6"),sQuery(id+"F0.wireOp",EDGE,"E12.6.7"),sQuery(id+"F0.wireOp",EDGE,"E12.6.10"),sQuery(id+"F0.wireOp",EDGE,"E12.6.11"),sQuery(id+"F0.wireOp",EDGE,"E12.7.0"),sQuery(id+"F0.wireOp",EDGE,"E12.7.1"),sQuery(id+"F0.wireOp",EDGE,"E12.7.2"),sQuery(id+"F0.wireOp",EDGE,"E12.7.3"),sQuery(id+"F0.wireOp",EDGE,"E12.7.4"),sQuery(id+"F0.wireOp",EDGE,"E12.7.5"),sQuery(id+"F0.wireOp",EDGE,"E12.7.6"),sQuery(id+"F0.wireOp",EDGE,"E12.7.7"),sQuery(id+"F0.wireOp",EDGE,"E12.7.10"),sQuery(id+"F0.wireOp",EDGE,"E12.7.11"),sQuery(id+"F0.wireOp",EDGE,"E12.8.0"),sQuery(id+"F0.wireOp",EDGE,"E12.8.1"),sQuery(id+"F0.wireOp",EDGE,"E12.8.2"),sQuery(id+"F0.wireOp",EDGE,"E12.8.3"),sQuery(id+"F0.wireOp",EDGE,"E12.8.4"),sQuery(id+"F0.wireOp",EDGE,"E12.8.5"),sQuery(id+"F0.wireOp",EDGE,"E12.8.6"),sQuery(id+"F0.wireOp",EDGE,"E12.8.7"),sQuery(id+"F0.wireOp",EDGE,"E12.8.10"),sQuery(id+"F0.wireOp",EDGE,"E12.8.11"),sQuery(id+"F0.wireOp",EDGE,"E12.9.0"),sQuery(id+"F0.wireOp",EDGE,"E12.9.1"),sQuery(id+"F0.wireOp",EDGE,"E12.9.2"),sQuery(id+"F0.wireOp",EDGE,"E12.9.3"),sQuery(id+"F0.wireOp",EDGE,"E12.9.4"),sQuery(id+"F0.wireOp",EDGE,"E12.9.5"),sQuery(id+"F0.wireOp",EDGE,"E12.9.6"),sQuery(id+"F0.wireOp",EDGE,"E12.9.7"),sQuery(id+"F0.wireOp",EDGE,"E12.9.10"),sQuery(id+"F0.wireOp",EDGE,"E12.9.11"),sQuery(id+"F0.wireOp",EDGE,"E13.1.0"),sQuery(id+"F0.wireOp",EDGE,"E13.1.1"),sQuery(id+"F0.wireOp",EDGE,"E13.1.2"),sQuery(id+"F0.wireOp",EDGE,"E13.1.5"),sQuery(id+"F0.wireOp",EDGE,"E13.1.6"),sQuery(id+"F0.wireOp",EDGE,"E13.1.7"),sQuery(id+"F0.wireOp",EDGE,"E13.1.8"),sQuery(id+"F0.wireOp",EDGE,"E13.1.9"),sQuery(id+"F0.wireOp",EDGE,"E13.1.10"),sQuery(id+"F0.wireOp",EDGE,"E13.1.11"),sQuery(id+"F0.wireOp",EDGE,"E13.2.0"),sQuery(id+"F0.wireOp",EDGE,"E13.2.1"),sQuery(id+"F0.wireOp",EDGE,"E13.2.2"),sQuery(id+"F0.wireOp",EDGE,"E13.2.5"),sQuery(id+"F0.wireOp",EDGE,"E13.2.6"),sQuery(id+"F0.wireOp",EDGE,"E13.2.7"),sQuery(id+"F0.wireOp",EDGE,"E13.2.8"),sQuery(id+"F0.wireOp",EDGE,"E13.2.9"),sQuery(id+"F0.wireOp",EDGE,"E13.2.10"),sQuery(id+"F0.wireOp",EDGE,"E13.2.11"),sQuery(id+"F0.wireOp",EDGE,"E13.3.0"),sQuery(id+"F0.wireOp",EDGE,"E13.3.1"),sQuery(id+"F0.wireOp",EDGE,"E13.3.2"),sQuery(id+"F0.wireOp",EDGE,"E13.3.5"),sQuery(id+"F0.wireOp",EDGE,"E13.3.6"),sQuery(id+"F0.wireOp",EDGE,"E13.3.7"),sQuery(id+"F0.wireOp",EDGE,"E13.3.8"),sQuery(id+"F0.wireOp",EDGE,"E13.3.9"),sQuery(id+"F0.wireOp",EDGE,"E13.3.10"),sQuery(id+"F0.wireOp",EDGE,"E13.3.11"),sQuery(id+"F0.wireOp",EDGE,"E13.4.0"),sQuery(id+"F0.wireOp",EDGE,"E13.4.1"),sQuery(id+"F0.wireOp",EDGE,"E13.4.2"),sQuery(id+"F0.wireOp",EDGE,"E13.4.5"),sQuery(id+"F0.wireOp",EDGE,"E13.4.6"),sQuery(id+"F0.wireOp",EDGE,"E13.4.7"),sQuery(id+"F0.wireOp",EDGE,"E13.4.8"),sQuery(id+"F0.wireOp",EDGE,"E13.4.9"),sQuery(id+"F0.wireOp",EDGE,"E13.4.10"),sQuery(id+"F0.wireOp",EDGE,"E13.4.11"),sQuery(id+"F0.wireOp",EDGE,"E13.5.0"),sQuery(id+"F0.wireOp",EDGE,"E13.5.1"),sQuery(id+"F0.wireOp",EDGE,"E13.5.2"),sQuery(id+"F0.wireOp",EDGE,"E13.5.5"),sQuery(id+"F0.wireOp",EDGE,"E13.5.6"),sQuery(id+"F0.wireOp",EDGE,"E13.5.7"),sQuery(id+"F0.wireOp",EDGE,"E13.5.8"),sQuery(id+"F0.wireOp",EDGE,"E13.5.9"),sQuery(id+"F0.wireOp",EDGE,"E13.5.10"),sQuery(id+"F0.wireOp",EDGE,"E13.5.11"),sQuery(id+"F0.wireOp",EDGE,"E13.6.0"),sQuery(id+"F0.wireOp",EDGE,"E13.6.1"),sQuery(id+"F0.wireOp",EDGE,"E13.6.2"),sQuery(id+"F0.wireOp",EDGE,"E13.6.5"),sQuery(id+"F0.wireOp",EDGE,"E13.6.6"),sQuery(id+"F0.wireOp",EDGE,"E13.6.7"),sQuery(id+"F0.wireOp",EDGE,"E13.6.8"),sQuery(id+"F0.wireOp",EDGE,"E13.6.9"),sQuery(id+"F0.wireOp",EDGE,"E13.6.10"),sQuery(id+"F0.wireOp",EDGE,"E13.6.11"),sQuery(id+"F0.wireOp",EDGE,"E13.7.0"),sQuery(id+"F0.wireOp",EDGE,"E13.7.1"),sQuery(id+"F0.wireOp",EDGE,"E13.7.2"),sQuery(id+"F0.wireOp",EDGE,"E13.7.5"),sQuery(id+"F0.wireOp",EDGE,"E13.7.6"),sQuery(id+"F0.wireOp",EDGE,"E13.7.7"),sQuery(id+"F0.wireOp",EDGE,"E13.7.8"),sQuery(id+"F0.wireOp",EDGE,"E13.7.9"),sQuery(id+"F0.wireOp",EDGE,"E13.7.10"),sQuery(id+"F0.wireOp",EDGE,"E13.7.11"),sQuery(id+"F0.wireOp",EDGE,"E13.8.0"),sQuery(id+"F0.wireOp",EDGE,"E13.8.1"),sQuery(id+"F0.wireOp",EDGE,"E13.8.2"),sQuery(id+"F0.wireOp",EDGE,"E13.8.5"),sQuery(id+"F0.wireOp",EDGE,"E13.8.6"),sQuery(id+"F0.wireOp",EDGE,"E13.8.7"),sQuery(id+"F0.wireOp",EDGE,"E13.8.8"),sQuery(id+"F0.wireOp",EDGE,"E13.8.9"),sQuery(id+"F0.wireOp",EDGE,"E13.8.10"),sQuery(id+"F0.wireOp",EDGE,"E13.8.11"),sQuery(id+"F0.wireOp",EDGE,"E3"),sQuery(id+"F0.wireOp",EDGE,"E2"),sQuery(id+"F0.wireOp",EDGE,"E1"),sQuery(id+"F0.wireOp",EDGE,"E4"),sQuery(id+"F0.wireOp",EDGE,"E8"),sQuery(id+"F0.wireOp",EDGE,"E5"),sQuery(id+"F0.wireOp",EDGE,"E11"),sQuery(id+"F0.wireOp",EDGE,"E6"),sQuery(id+"F0.wireOp",EDGE,"E7"),sQuery(id+"F0.wireOp",EDGE,"E10"),sQuery(id+"F0.wireOp",EDGE,"E14"),sQuery(id+"F0.wireOp",EDGE,"E15"),sQuery(id+"F0.wireOp",EDGE,"E20.trimOffspring"),sQuery(id+"F0.wireOp",EDGE,"E21.trimOffspring"),sQuery(id+"F0.wireOp",EDGE,"E22.trimOffspring"),sQuery(id+"F0.wireOp",EDGE,"E23.trimOffspring"),sQuery(id+"F0.wireOp",EDGE,"E24.trimOffspring"),sQuery(id+"F0.wireOp",EDGE,"E25.trimOffspring"),sQuery(id+"F0.wireOp",EDGE,"E26.trimOffspring"),sQuery(id+"F0.wireOp",EDGE,"E27.trimOffspring"),sQuery(id+"F0.wireOp",EDGE,"E28.trimOffspring"),sQuery(id+"F0.wireOp",EDGE,"E29.trimOffspring"),sQuery(id+"F0.wireOp",EDGE,"E30.trimOffspring"),sQuery(id+"F0.wireOp",EDGE,"E31.trimOffspring"),sQuery(id+"F0.wireOp",EDGE,"E32.trimOffspring"),sQuery(id+"F0.wireOp",EDGE,"E33.trimOffspring"),sQuery(id+"F0.wireOp",EDGE,"E34.trimOffspring"),sQuery(id+"F0.wireOp",EDGE,"E35.trimOffspring"),sQuery(id+"F0.wireOp",EDGE,"E36.trimOffspring"),sQuery(id+"F0.wireOp",EDGE,"E37")])],"isStart":true});
            var sketch = newSketch(context, id + "F3", { "sketchPlane" : qUnion([Q0])});
            skCircle(sketch, "E38", {"center": v(0, 0) * mm, "radius": 53.54 * mm});
            skLineSegment(sketch, "E39", {"start": v(0, 0) * mm, "end": v(0, -53.43) * mm});
            skLineSegment(sketch, "E40", {"start": v(0, -53.43) * mm, "end": v(3.81, -53.43) * mm});
            skLineSegment(sketch, "E41", {"start": v(0, -53.43) * mm, "end": v(-3.8, -53.43) * mm});
            skArc(sketch, "E42", {"start": v(-3.8, -53.43) * mm, "mid": v(-2.42, -51.12) * mm, "end": v(-1.14, -48.75) * mm});
            skArc(sketch, "E43.0", {"start": v(-2.1, -54.52) * mm, "mid": v(-1.02, -52.76) * mm, "end": v(0, -50.96) * mm});
            skLineSegment(sketch, "E44", {"start": v(-2.1, -54.52) * mm, "end": v(-3.8, -53.43) * mm});
            skLineSegment(sketch, "E45", {"start": v(2.1, -54.52) * mm, "end": v(3.81, -53.43) * mm});
            skArc(sketch, "E46.trimOffspring", {"start": v(0, -46.4) * mm, "mid": v(4.44, -31.13) * mm, "end": v(4.44, -15.23) * mm});
            skArc(sketch, "E47.trimOffspring", {"start": v(1.14, -48.75) * mm, "mid": v(2.42, -51.12) * mm, "end": v(3.81, -53.43) * mm});
            skArc(sketch, "E48.trimOffspring", {"start": v(1.14, -48.75) * mm, "mid": v(5.99, -34.21) * mm, "end": v(6.88, -18.9) * mm});
            skArc(sketch, "E49.trimOffspring", {"start": v(0, -50.96) * mm, "mid": v(1.02, -52.76) * mm, "end": v(2.1, -54.52) * mm});
            skArc(sketch, "E50.1.0", {"start": v(32.2, -36.62) * mm, "mid": v(26.58, -22.36) * mm, "end": v(17.42, -10.06) * mm});
            skArc(sketch, "E50.1.1", {"start": v(29.82, -35.54) * mm, "mid": v(23.42, -21) * mm, "end": v(13.2, -8.82) * mm});
            skArc(sketch, "E50.1.5", {"start": v(32.2, -36.62) * mm, "mid": v(34.71, -37.6) * mm, "end": v(37.26, -38.48) * mm});
            skArc(sketch, "E50.1.6", {"start": v(32.76, -39.04) * mm, "mid": v(34.7, -39.76) * mm, "end": v(36.65, -40.42) * mm});
            skLineSegment(sketch, "E50.1.7", {"start": v(36.65, -40.42) * mm, "end": v(37.26, -38.48) * mm});
            skArc(sketch, "E50.1.8", {"start": v(33.44, -43.11) * mm, "mid": v(33.13, -41.07) * mm, "end": v(32.76, -39.04) * mm});
            skLineSegment(sketch, "E50.1.9", {"start": v(33.44, -43.11) * mm, "end": v(31.42, -43.38) * mm});
            skArc(sketch, "E50.1.10", {"start": v(31.42, -43.38) * mm, "mid": v(31.01, -40.72) * mm, "end": v(30.47, -38.08) * mm});
            skArc(sketch, "E50.2.0", {"start": v(48.21, -7.35) * mm, "mid": v(34.73, -0.04) * mm, "end": v(19.81, 3.5) * mm});
            skArc(sketch, "E50.2.1", {"start": v(45.69, -8.06) * mm, "mid": v(31.43, -1.03) * mm, "end": v(15.77, 1.73) * mm});
            skArc(sketch, "E50.2.5", {"start": v(48.21, -7.35) * mm, "mid": v(50.77, -6.5) * mm, "end": v(53.28, -5.53) * mm});
            skArc(sketch, "E50.2.6", {"start": v(50.19, -8.85) * mm, "mid": v(52.13, -8.16) * mm, "end": v(54.06, -7.4) * mm});
            skLineSegment(sketch, "E50.2.7", {"start": v(54.06, -7.4) * mm, "end": v(53.28, -5.53) * mm});
            skArc(sketch, "E50.2.8", {"start": v(53.33, -11.53) * mm, "mid": v(51.78, -10.16) * mm, "end": v(50.19, -8.85) * mm});
            skLineSegment(sketch, "E50.2.9", {"start": v(53.33, -11.53) * mm, "end": v(51.96, -13.03) * mm});
            skArc(sketch, "E50.2.10", {"start": v(51.96, -13.03) * mm, "mid": v(49.93, -11.26) * mm, "end": v(47.82, -9.58) * mm});
            skArc(sketch, "E50.3.0", {"start": v(41.65, 25.36) * mm, "mid": v(26.63, 22.3) * mm, "end": v(12.93, 15.41) * mm});
            skArc(sketch, "E50.3.1", {"start": v(40.18, 23.2) * mm, "mid": v(24.74, 19.41) * mm, "end": v(10.97, 11.46) * mm});
            skArc(sketch, "E50.3.5", {"start": v(41.65, 25.36) * mm, "mid": v(43.07, 27.65) * mm, "end": v(44.37, 30.01) * mm});
            skArc(sketch, "E50.3.6", {"start": v(44.13, 25.48) * mm, "mid": v(45.18, 27.26) * mm, "end": v(46.17, 29.08) * mm});
            skLineSegment(sketch, "E50.3.7", {"start": v(46.17, 29.08) * mm, "end": v(44.37, 30.01) * mm});
            skArc(sketch, "E50.3.8", {"start": v(48.27, 25.44) * mm, "mid": v(46.2, 25.5) * mm, "end": v(44.13, 25.48) * mm});
            skLineSegment(sketch, "E50.3.9", {"start": v(48.27, 25.44) * mm, "end": v(48.18, 23.41) * mm});
            skArc(sketch, "E50.3.10", {"start": v(48.18, 23.41) * mm, "mid": v(45.48, 23.47) * mm, "end": v(42.79, 23.4) * mm});
            skArc(sketch, "E50.4.0", {"start": v(15.6, 46.2) * mm, "mid": v(6.07, 34.2) * mm, "end": v(0, 20.12) * mm});
            skArc(sketch, "E50.4.1", {"start": v(15.87, 43.6) * mm, "mid": v(6.47, 30.77) * mm, "end": v(1.04, 15.83) * mm});
            skArc(sketch, "E50.4.5", {"start": v(15.6, 46.2) * mm, "mid": v(15.21, 48.87) * mm, "end": v(14.7, 51.5) * mm});
            skArc(sketch, "E50.4.6", {"start": v(17.43, 47.89) * mm, "mid": v(17.09, 49.93) * mm, "end": v(16.68, 51.95) * mm});
            skLineSegment(sketch, "E50.4.7", {"start": v(16.68, 51.95) * mm, "end": v(14.7, 51.5) * mm});
            skArc(sketch, "E50.4.8", {"start": v(20.62, 50.52) * mm, "mid": v(19, 49.23) * mm, "end": v(17.43, 47.89) * mm});
            skLineSegment(sketch, "E50.4.9", {"start": v(20.62, 50.52) * mm, "end": v(21.85, 48.9) * mm});
            skArc(sketch, "E50.4.10", {"start": v(21.85, 48.9) * mm, "mid": v(19.76, 47.21) * mm, "end": v(17.74, 45.43) * mm});
            skArc(sketch, "E50.5.0", {"start": v(-17.74, 45.43) * mm, "mid": v(-17.33, 30.1) * mm, "end": v(-12.93, 15.41) * mm});
            skArc(sketch, "E50.5.1", {"start": v(-15.87, 43.6) * mm, "mid": v(-14.82, 27.73) * mm, "end": v(-9.38, 12.8) * mm});
            skArc(sketch, "E50.5.5", {"start": v(-17.74, 45.43) * mm, "mid": v(-19.76, 47.21) * mm, "end": v(-21.85, 48.9) * mm});
            skArc(sketch, "E50.5.6", {"start": v(-17.43, 47.89) * mm, "mid": v(-19, 49.23) * mm, "end": v(-20.62, 50.52) * mm});
            skLineSegment(sketch, "E50.5.7", {"start": v(-20.62, 50.52) * mm, "end": v(-21.85, 48.9) * mm});
            skArc(sketch, "E50.5.8", {"start": v(-16.68, 51.95) * mm, "mid": v(-17.09, 49.93) * mm, "end": v(-17.43, 47.89) * mm});
            skLineSegment(sketch, "E50.5.9", {"start": v(-16.68, 51.95) * mm, "end": v(-14.7, 51.5) * mm});
            skArc(sketch, "E50.5.10", {"start": v(-14.7, 51.5) * mm, "mid": v(-15.21, 48.87) * mm, "end": v(-15.6, 46.2) * mm});
            skArc(sketch, "E50.6.0", {"start": v(-42.79, 23.4) * mm, "mid": v(-32.62, 11.92) * mm, "end": v(-19.81, 3.5) * mm});
            skArc(sketch, "E50.6.1", {"start": v(-40.18, 23.2) * mm, "mid": v(-29.18, 11.72) * mm, "end": v(-15.41, 3.77) * mm});
            skArc(sketch, "E50.6.5", {"start": v(-42.79, 23.4) * mm, "mid": v(-45.48, 23.47) * mm, "end": v(-48.18, 23.41) * mm});
            skArc(sketch, "E50.6.6", {"start": v(-44.13, 25.48) * mm, "mid": v(-46.2, 25.5) * mm, "end": v(-48.27, 25.44) * mm});
            skLineSegment(sketch, "E50.6.7", {"start": v(-48.27, 25.44) * mm, "end": v(-48.18, 23.41) * mm});
            skArc(sketch, "E50.6.8", {"start": v(-46.17, 29.08) * mm, "mid": v(-45.18, 27.26) * mm, "end": v(-44.13, 25.48) * mm});
            skLineSegment(sketch, "E50.6.9", {"start": v(-46.17, 29.08) * mm, "end": v(-44.37, 30.01) * mm});
            skArc(sketch, "E50.6.10", {"start": v(-44.37, 30.01) * mm, "mid": v(-43.07, 27.65) * mm, "end": v(-41.65, 25.36) * mm});
            skArc(sketch, "E50.7.0", {"start": v(-47.82, -9.58) * mm, "mid": v(-32.65, -11.84) * mm, "end": v(-17.42, -10.06) * mm});
            skArc(sketch, "E50.7.1", {"start": v(-45.69, -8.06) * mm, "mid": v(-29.89, -9.78) * mm, "end": v(-14.23, -7.02) * mm});
            skArc(sketch, "E50.7.5", {"start": v(-47.82, -9.58) * mm, "mid": v(-49.93, -11.26) * mm, "end": v(-51.96, -13.03) * mm});
            skArc(sketch, "E50.7.6", {"start": v(-50.19, -8.85) * mm, "mid": v(-51.78, -10.16) * mm, "end": v(-53.33, -11.53) * mm});
            skLineSegment(sketch, "E50.7.7", {"start": v(-53.33, -11.53) * mm, "end": v(-51.96, -13.03) * mm});
            skArc(sketch, "E50.7.8", {"start": v(-54.06, -7.4) * mm, "mid": v(-52.13, -8.16) * mm, "end": v(-50.19, -8.85) * mm});
            skLineSegment(sketch, "E50.7.9", {"start": v(-54.06, -7.4) * mm, "end": v(-53.28, -5.53) * mm});
            skArc(sketch, "E50.7.10", {"start": v(-53.28, -5.53) * mm, "mid": v(-50.77, -6.5) * mm, "end": v(-48.21, -7.35) * mm});
            skArc(sketch, "E50.8.0", {"start": v(-30.47, -38.08) * mm, "mid": v(-17.4, -30.06) * mm, "end": v(-6.88, -18.9) * mm});
            skArc(sketch, "E50.8.1", {"start": v(-29.82, -35.54) * mm, "mid": v(-16.6, -26.7) * mm, "end": v(-6.4, -14.52) * mm});
            skArc(sketch, "E50.8.5", {"start": v(-30.47, -38.08) * mm, "mid": v(-31.01, -40.72) * mm, "end": v(-31.42, -43.38) * mm});
            skArc(sketch, "E50.8.6", {"start": v(-32.76, -39.04) * mm, "mid": v(-33.13, -41.07) * mm, "end": v(-33.44, -43.11) * mm});
            skLineSegment(sketch, "E50.8.7", {"start": v(-33.44, -43.11) * mm, "end": v(-31.42, -43.38) * mm});
            skArc(sketch, "E50.8.8", {"start": v(-36.65, -40.42) * mm, "mid": v(-34.7, -39.76) * mm, "end": v(-32.76, -39.04) * mm});
            skLineSegment(sketch, "E50.8.9", {"start": v(-36.65, -40.42) * mm, "end": v(-37.26, -38.48) * mm});
            skArc(sketch, "E50.8.10", {"start": v(-37.26, -38.48) * mm, "mid": v(-34.71, -37.6) * mm, "end": v(-32.2, -36.62) * mm});
            skArc(sketch, "E51.trimOffspring", {"start": v(-17.42, -10.06) * mm, "mid": v(-26.58, -22.36) * mm, "end": v(-32.2, -36.62) * mm});
            skArc(sketch, "E52.trimOffspring", {"start": v(-13.2, -8.82) * mm, "mid": v(-8.55, -7.03) * mm, "end": v(-4.08, -4.86) * mm});
            skArc(sketch, "E53.trimOffspring", {"start": v(-13.2, -8.82) * mm, "mid": v(-23.42, -21) * mm, "end": v(-29.82, -35.54) * mm});
            skArc(sketch, "E54.trimOffspring", {"start": v(-15.77, 1.73) * mm, "mid": v(-11.07, 0.1) * mm, "end": v(-6.25, -1.1) * mm});
            skArc(sketch, "E55.trimOffspring", {"start": v(-19.81, 3.5) * mm, "mid": v(-34.73, -0.04) * mm, "end": v(-48.21, -7.35) * mm});
            skArc(sketch, "E56.trimOffspring", {"start": v(-15.77, 1.73) * mm, "mid": v(-31.43, -1.03) * mm, "end": v(-45.69, -8.06) * mm});
            skArc(sketch, "E57.trimOffspring", {"start": v(-10.97, 11.46) * mm, "mid": v(-24.74, 19.41) * mm, "end": v(-40.18, 23.2) * mm});
            skArc(sketch, "E58.trimOffspring", {"start": v(-12.93, 15.41) * mm, "mid": v(-26.63, 22.3) * mm, "end": v(-41.65, 25.36) * mm});
            skArc(sketch, "E59.trimOffspring", {"start": v(-10.97, 11.46) * mm, "mid": v(-8.41, 7.2) * mm, "end": v(-5.5, 3.17) * mm});
            skArc(sketch, "E60.trimOffspring", {"start": v(-1.04, 15.83) * mm, "mid": v(-6.47, 30.77) * mm, "end": v(-15.87, 43.6) * mm});
            skArc(sketch, "E61.trimOffspring", {"start": v(-1.04, 15.83) * mm, "mid": v(-1.81, 10.92) * mm, "end": v(-2.17, 5.96) * mm});
            skArc(sketch, "E62.trimOffspring", {"start": v(0, 20.12) * mm, "mid": v(-6.07, 34.2) * mm, "end": v(-15.6, 46.2) * mm});
            skArc(sketch, "E63.trimOffspring", {"start": v(9.38, 12.8) * mm, "mid": v(14.82, 27.73) * mm, "end": v(15.87, 43.6) * mm});
            skArc(sketch, "E64.trimOffspring", {"start": v(9.38, 12.8) * mm, "mid": v(5.63, 9.53) * mm, "end": v(2.17, 5.96) * mm});
            skArc(sketch, "E65.trimOffspring", {"start": v(12.93, 15.41) * mm, "mid": v(17.33, 30.1) * mm, "end": v(17.74, 45.43) * mm});
            skArc(sketch, "E66.trimOffspring", {"start": v(19.81, 3.5) * mm, "mid": v(32.62, 11.92) * mm, "end": v(42.79, 23.4) * mm});
            skArc(sketch, "E67.trimOffspring", {"start": v(15.41, 3.77) * mm, "mid": v(10.44, 3.68) * mm, "end": v(5.5, 3.17) * mm});
            skArc(sketch, "E68.trimOffspring", {"start": v(15.41, 3.77) * mm, "mid": v(29.18, 11.72) * mm, "end": v(40.18, 23.2) * mm});
            skArc(sketch, "E69.trimOffspring", {"start": v(14.23, -7.02) * mm, "mid": v(29.89, -9.78) * mm, "end": v(45.69, -8.06) * mm});
            skArc(sketch, "E70.trimOffspring", {"start": v(17.42, -10.06) * mm, "mid": v(32.65, -11.84) * mm, "end": v(47.82, -9.58) * mm});
            skArc(sketch, "E71.trimOffspring", {"start": v(14.23, -7.02) * mm, "mid": v(10.37, -3.89) * mm, "end": v(6.25, -1.1) * mm});
            skArc(sketch, "E72.trimOffspring", {"start": v(6.88, -18.9) * mm, "mid": v(17.4, -30.06) * mm, "end": v(30.47, -38.08) * mm});
            skArc(sketch, "E73.trimOffspring", {"start": v(6.4, -14.52) * mm, "mid": v(5.44, -9.64) * mm, "end": v(4.08, -4.86) * mm});
            skArc(sketch, "E74.trimOffspring", {"start": v(6.4, -14.52) * mm, "mid": v(16.6, -26.7) * mm, "end": v(29.82, -35.54) * mm});
            skArc(sketch, "E75.trimOffspring", {"start": v(-4.44, -15.23) * mm, "mid": v(-4.44, -31.13) * mm, "end": v(0, -46.4) * mm});
            skArc(sketch, "E76.trimOffspring", {"start": v(-4.44, -15.23) * mm, "mid": v(-2.03, -10.88) * mm, "end": v(0, -6.35) * mm});
            skArc(sketch, "E77.trimOffspring", {"start": v(-6.88, -18.9) * mm, "mid": v(-5.99, -34.21) * mm, "end": v(-1.14, -48.75) * mm});
            skArc(sketch, "E78.trimOffspring", {"start": v(-6.25, -1.1) * mm, "mid": v(-10.37, -3.89) * mm, "end": v(-14.23, -7.02) * mm});
            skArc(sketch, "E79.trimOffspring", {"start": v(-4.08, -4.86) * mm, "mid": v(-5.44, -9.64) * mm, "end": v(-6.4, -14.52) * mm});
            skArc(sketch, "E80.trimOffspring", {"start": v(0, -6.35) * mm, "mid": v(2.03, -10.88) * mm, "end": v(4.44, -15.23) * mm});
            skArc(sketch, "E81.trimOffspring", {"start": v(4.08, -4.86) * mm, "mid": v(8.55, -7.03) * mm, "end": v(13.2, -8.82) * mm});
            skArc(sketch, "E82.trimOffspring", {"start": v(6.25, -1.1) * mm, "mid": v(11.07, 0.1) * mm, "end": v(15.77, 1.73) * mm});
            skArc(sketch, "E83.trimOffspring", {"start": v(5.5, 3.17) * mm, "mid": v(8.41, 7.2) * mm, "end": v(10.97, 11.46) * mm});
            skArc(sketch, "E84.trimOffspring", {"start": v(2.17, 5.96) * mm, "mid": v(1.81, 10.92) * mm, "end": v(1.04, 15.83) * mm});
            skArc(sketch, "E85.trimOffspring", {"start": v(-2.17, 5.96) * mm, "mid": v(-5.63, 9.53) * mm, "end": v(-9.38, 12.8) * mm});
            skArc(sketch, "E86.trimOffspring", {"start": v(-5.5, 3.17) * mm, "mid": v(-10.44, 3.68) * mm, "end": v(-15.41, 3.77) * mm});
            skSolve(sketch);
        }
        {
            var Q0;
            Q0=makeQuery(id+"F3.imprint","IMPRINT",FACE,{"disambiguationData":[TD([[makeQuery(id+"F3.imprint","IMPRINT",EDGE,{"derivedFrom":sQuery(id+"F3.wireOp",EDGE,"E46.trimOffspring")}),-1.0]])]});
            extrude(context, id + "F4", {"entities" : qUnion([Q0]), "operationType" : NewBodyOperationType.ADD, "oppositeDirection" : true, "depth" : 5.08 * mm});
        }
        {
            var Q0;
            {var subQ0=sQuery(id+"F0.wireOp",EDGE,"E15");Q0=makeQuery(id+"F4.boolean.opBoolean","MERGE",FACE,{"derivedFrom":[makeQuery(id+"F2.opChamfer","SPLIT",FACE,{"disambiguationData":[OD(18.0)],"derivedFrom":makeQuery(id+"F1.opExtrude","CAP_FACE",FACE,{"disambiguationData":[OSD([sQuery(id+"F0.wireOp",EDGE,"E12.1.0"),sQuery(id+"F0.wireOp",EDGE,"E12.1.1"),sQuery(id+"F0.wireOp",EDGE,"E12.1.2"),sQuery(id+"F0.wireOp",EDGE,"E12.1.3"),sQuery(id+"F0.wireOp",EDGE,"E12.1.4"),sQuery(id+"F0.wireOp",EDGE,"E12.1.5"),sQuery(id+"F0.wireOp",EDGE,"E12.1.6"),sQuery(id+"F0.wireOp",EDGE,"E12.1.7"),sQuery(id+"F0.wireOp",EDGE,"E12.1.10"),sQuery(id+"F0.wireOp",EDGE,"E12.1.11"),sQuery(id+"F0.wireOp",EDGE,"E12.2.0"),sQuery(id+"F0.wireOp",EDGE,"E12.2.1"),sQuery(id+"F0.wireOp",EDGE,"E12.2.2"),sQuery(id+"F0.wireOp",EDGE,"E12.2.3"),sQuery(id+"F0.wireOp",EDGE,"E12.2.4"),sQuery(id+"F0.wireOp",EDGE,"E12.2.5"),sQuery(id+"F0.wireOp",EDGE,"E12.2.6"),sQuery(id+"F0.wireOp",EDGE,"E12.2.7"),sQuery(id+"F0.wireOp",EDGE,"E12.2.10"),sQuery(id+"F0.wireOp",EDGE,"E12.2.11"),sQuery(id+"F0.wireOp",EDGE,"E12.3.0"),sQuery(id+"F0.wireOp",EDGE,"E12.3.1"),sQuery(id+"F0.wireOp",EDGE,"E12.3.2"),sQuery(id+"F0.wireOp",EDGE,"E12.3.3"),sQuery(id+"F0.wireOp",EDGE,"E12.3.4"),sQuery(id+"F0.wireOp",EDGE,"E12.3.5"),sQuery(id+"F0.wireOp",EDGE,"E12.3.6"),sQuery(id+"F0.wireOp",EDGE,"E12.3.7"),sQuery(id+"F0.wireOp",EDGE,"E12.3.10"),sQuery(id+"F0.wireOp",EDGE,"E12.3.11"),sQuery(id+"F0.wireOp",EDGE,"E12.4.0"),sQuery(id+"F0.wireOp",EDGE,"E12.4.1"),sQuery(id+"F0.wireOp",EDGE,"E12.4.2"),sQuery(id+"F0.wireOp",EDGE,"E12.4.3"),sQuery(id+"F0.wireOp",EDGE,"E12.4.4"),sQuery(id+"F0.wireOp",EDGE,"E12.4.5"),sQuery(id+"F0.wireOp",EDGE,"E12.4.6"),sQuery(id+"F0.wireOp",EDGE,"E12.4.7"),sQuery(id+"F0.wireOp",EDGE,"E12.4.10"),sQuery(id+"F0.wireOp",EDGE,"E12.4.11"),sQuery(id+"F0.wireOp",EDGE,"E12.5.0"),sQuery(id+"F0.wireOp",EDGE,"E12.5.1"),sQuery(id+"F0.wireOp",EDGE,"E12.5.2"),sQuery(id+"F0.wireOp",EDGE,"E12.5.3"),sQuery(id+"F0.wireOp",EDGE,"E12.5.4"),sQuery(id+"F0.wireOp",EDGE,"E12.5.5"),sQuery(id+"F0.wireOp",EDGE,"E12.5.6"),sQuery(id+"F0.wireOp",EDGE,"E12.5.7"),sQuery(id+"F0.wireOp",EDGE,"E12.5.10"),sQuery(id+"F0.wireOp",EDGE,"E12.5.11"),sQuery(id+"F0.wireOp",EDGE,"E12.6.0"),sQuery(id+"F0.wireOp",EDGE,"E12.6.1"),sQuery(id+"F0.wireOp",EDGE,"E12.6.2"),sQuery(id+"F0.wireOp",EDGE,"E12.6.3"),sQuery(id+"F0.wireOp",EDGE,"E12.6.4"),sQuery(id+"F0.wireOp",EDGE,"E12.6.5"),sQuery(id+"F0.wireOp",EDGE,"E12.6.6"),sQuery(id+"F0.wireOp",EDGE,"E12.6.7"),sQuery(id+"F0.wireOp",EDGE,"E12.6.10"),sQuery(id+"F0.wireOp",EDGE,"E12.6.11"),sQuery(id+"F0.wireOp",EDGE,"E12.7.0"),sQuery(id+"F0.wireOp",EDGE,"E12.7.1"),sQuery(id+"F0.wireOp",EDGE,"E12.7.2"),sQuery(id+"F0.wireOp",EDGE,"E12.7.3"),sQuery(id+"F0.wireOp",EDGE,"E12.7.4"),sQuery(id+"F0.wireOp",EDGE,"E12.7.5"),sQuery(id+"F0.wireOp",EDGE,"E12.7.6"),sQuery(id+"F0.wireOp",EDGE,"E12.7.7"),sQuery(id+"F0.wireOp",EDGE,"E12.7.10"),sQuery(id+"F0.wireOp",EDGE,"E12.7.11"),sQuery(id+"F0.wireOp",EDGE,"E12.8.0"),sQuery(id+"F0.wireOp",EDGE,"E12.8.1"),sQuery(id+"F0.wireOp",EDGE,"E12.8.2"),sQuery(id+"F0.wireOp",EDGE,"E12.8.3"),sQuery(id+"F0.wireOp",EDGE,"E12.8.4"),sQuery(id+"F0.wireOp",EDGE,"E12.8.5"),sQuery(id+"F0.wireOp",EDGE,"E12.8.6"),sQuery(id+"F0.wireOp",EDGE,"E12.8.7"),sQuery(id+"F0.wireOp",EDGE,"E12.8.10"),sQuery(id+"F0.wireOp",EDGE,"E12.8.11"),sQuery(id+"F0.wireOp",EDGE,"E12.9.0"),sQuery(id+"F0.wireOp",EDGE,"E12.9.1"),sQuery(id+"F0.wireOp",EDGE,"E12.9.2"),sQuery(id+"F0.wireOp",EDGE,"E12.9.3"),sQuery(id+"F0.wireOp",EDGE,"E12.9.4"),sQuery(id+"F0.wireOp",EDGE,"E12.9.5"),sQuery(id+"F0.wireOp",EDGE,"E12.9.6"),sQuery(id+"F0.wireOp",EDGE,"E12.9.7"),sQuery(id+"F0.wireOp",EDGE,"E12.9.10"),sQuery(id+"F0.wireOp",EDGE,"E12.9.11"),sQuery(id+"F0.wireOp",EDGE,"E13.1.0"),sQuery(id+"F0.wireOp",EDGE,"E13.1.1"),sQuery(id+"F0.wireOp",EDGE,"E13.1.2"),sQuery(id+"F0.wireOp",EDGE,"E13.1.5"),sQuery(id+"F0.wireOp",EDGE,"E13.1.6"),sQuery(id+"F0.wireOp",EDGE,"E13.1.7"),sQuery(id+"F0.wireOp",EDGE,"E13.1.8"),sQuery(id+"F0.wireOp",EDGE,"E13.1.9"),sQuery(id+"F0.wireOp",EDGE,"E13.1.10"),sQuery(id+"F0.wireOp",EDGE,"E13.1.11"),sQuery(id+"F0.wireOp",EDGE,"E13.2.0"),sQuery(id+"F0.wireOp",EDGE,"E13.2.1"),sQuery(id+"F0.wireOp",EDGE,"E13.2.2"),sQuery(id+"F0.wireOp",EDGE,"E13.2.5"),sQuery(id+"F0.wireOp",EDGE,"E13.2.6"),sQuery(id+"F0.wireOp",EDGE,"E13.2.7"),sQuery(id+"F0.wireOp",EDGE,"E13.2.8"),sQuery(id+"F0.wireOp",EDGE,"E13.2.9"),sQuery(id+"F0.wireOp",EDGE,"E13.2.10"),sQuery(id+"F0.wireOp",EDGE,"E13.2.11"),sQuery(id+"F0.wireOp",EDGE,"E13.3.0"),sQuery(id+"F0.wireOp",EDGE,"E13.3.1"),sQuery(id+"F0.wireOp",EDGE,"E13.3.2"),sQuery(id+"F0.wireOp",EDGE,"E13.3.5"),sQuery(id+"F0.wireOp",EDGE,"E13.3.6"),sQuery(id+"F0.wireOp",EDGE,"E13.3.7"),sQuery(id+"F0.wireOp",EDGE,"E13.3.8"),sQuery(id+"F0.wireOp",EDGE,"E13.3.9"),sQuery(id+"F0.wireOp",EDGE,"E13.3.10"),sQuery(id+"F0.wireOp",EDGE,"E13.3.11"),sQuery(id+"F0.wireOp",EDGE,"E13.4.0"),sQuery(id+"F0.wireOp",EDGE,"E13.4.1"),sQuery(id+"F0.wireOp",EDGE,"E13.4.2"),sQuery(id+"F0.wireOp",EDGE,"E13.4.5"),sQuery(id+"F0.wireOp",EDGE,"E13.4.6"),sQuery(id+"F0.wireOp",EDGE,"E13.4.7"),sQuery(id+"F0.wireOp",EDGE,"E13.4.8"),sQuery(id+"F0.wireOp",EDGE,"E13.4.9"),sQuery(id+"F0.wireOp",EDGE,"E13.4.10"),sQuery(id+"F0.wireOp",EDGE,"E13.4.11"),sQuery(id+"F0.wireOp",EDGE,"E13.5.0"),sQuery(id+"F0.wireOp",EDGE,"E13.5.1"),sQuery(id+"F0.wireOp",EDGE,"E13.5.2"),sQuery(id+"F0.wireOp",EDGE,"E13.5.5"),sQuery(id+"F0.wireOp",EDGE,"E13.5.6"),sQuery(id+"F0.wireOp",EDGE,"E13.5.7"),sQuery(id+"F0.wireOp",EDGE,"E13.5.8"),sQuery(id+"F0.wireOp",EDGE,"E13.5.9"),sQuery(id+"F0.wireOp",EDGE,"E13.5.10"),sQuery(id+"F0.wireOp",EDGE,"E13.5.11"),sQuery(id+"F0.wireOp",EDGE,"E13.6.0"),sQuery(id+"F0.wireOp",EDGE,"E13.6.1"),sQuery(id+"F0.wireOp",EDGE,"E13.6.2"),sQuery(id+"F0.wireOp",EDGE,"E13.6.5"),sQuery(id+"F0.wireOp",EDGE,"E13.6.6"),sQuery(id+"F0.wireOp",EDGE,"E13.6.7"),sQuery(id+"F0.wireOp",EDGE,"E13.6.8"),sQuery(id+"F0.wireOp",EDGE,"E13.6.9"),sQuery(id+"F0.wireOp",EDGE,"E13.6.10"),sQuery(id+"F0.wireOp",EDGE,"E13.6.11"),sQuery(id+"F0.wireOp",EDGE,"E13.7.0"),sQuery(id+"F0.wireOp",EDGE,"E13.7.1"),sQuery(id+"F0.wireOp",EDGE,"E13.7.2"),sQuery(id+"F0.wireOp",EDGE,"E13.7.5"),sQuery(id+"F0.wireOp",EDGE,"E13.7.6"),sQuery(id+"F0.wireOp",EDGE,"E13.7.7"),sQuery(id+"F0.wireOp",EDGE,"E13.7.8"),sQuery(id+"F0.wireOp",EDGE,"E13.7.9"),sQuery(id+"F0.wireOp",EDGE,"E13.7.10"),sQuery(id+"F0.wireOp",EDGE,"E13.7.11"),sQuery(id+"F0.wireOp",EDGE,"E13.8.0"),sQuery(id+"F0.wireOp",EDGE,"E13.8.1"),sQuery(id+"F0.wireOp",EDGE,"E13.8.2"),sQuery(id+"F0.wireOp",EDGE,"E13.8.5"),sQuery(id+"F0.wireOp",EDGE,"E13.8.6"),sQuery(id+"F0.wireOp",EDGE,"E13.8.7"),sQuery(id+"F0.wireOp",EDGE,"E13.8.8"),sQuery(id+"F0.wireOp",EDGE,"E13.8.9"),sQuery(id+"F0.wireOp",EDGE,"E13.8.10"),sQuery(id+"F0.wireOp",EDGE,"E13.8.11"),sQuery(id+"F0.wireOp",EDGE,"E3"),sQuery(id+"F0.wireOp",EDGE,"E2"),sQuery(id+"F0.wireOp",EDGE,"E1"),sQuery(id+"F0.wireOp",EDGE,"E4"),sQuery(id+"F0.wireOp",EDGE,"E8"),sQuery(id+"F0.wireOp",EDGE,"E5"),sQuery(id+"F0.wireOp",EDGE,"E11"),sQuery(id+"F0.wireOp",EDGE,"E6"),sQuery(id+"F0.wireOp",EDGE,"E7"),sQuery(id+"F0.wireOp",EDGE,"E10"),sQuery(id+"F0.wireOp",EDGE,"E14"),subQ0,sQuery(id+"F0.wireOp",EDGE,"E20.trimOffspring"),sQuery(id+"F0.wireOp",EDGE,"E21.trimOffspring"),sQuery(id+"F0.wireOp",EDGE,"E22.trimOffspring"),sQuery(id+"F0.wireOp",EDGE,"E23.trimOffspring"),sQuery(id+"F0.wireOp",EDGE,"E24.trimOffspring"),sQuery(id+"F0.wireOp",EDGE,"E25.trimOffspring"),sQuery(id+"F0.wireOp",EDGE,"E26.trimOffspring"),sQuery(id+"F0.wireOp",EDGE,"E27.trimOffspring"),sQuery(id+"F0.wireOp",EDGE,"E28.trimOffspring"),sQuery(id+"F0.wireOp",EDGE,"E29.trimOffspring"),sQuery(id+"F0.wireOp",EDGE,"E30.trimOffspring"),sQuery(id+"F0.wireOp",EDGE,"E31.trimOffspring"),sQuery(id+"F0.wireOp",EDGE,"E32.trimOffspring"),sQuery(id+"F0.wireOp",EDGE,"E33.trimOffspring"),sQuery(id+"F0.wireOp",EDGE,"E34.trimOffspring"),sQuery(id+"F0.wireOp",EDGE,"E35.trimOffspring"),sQuery(id+"F0.wireOp",EDGE,"E36.trimOffspring"),sQuery(id+"F0.wireOp",EDGE,"E37")])],"isStart":false})}),makeQuery(id+"F4.opExtrude","CAP_FACE",FACE,{"disambiguationData":[OSD([subQ0,sQuery(id+"F3.wireOp",EDGE,"E42"),sQuery(id+"F3.wireOp",EDGE,"E43.0"),sQuery(id+"F3.wireOp",EDGE,"E46.trimOffspring"),sQuery(id+"F3.wireOp",EDGE,"E47.trimOffspring"),sQuery(id+"F3.wireOp",EDGE,"E48.trimOffspring"),sQuery(id+"F3.wireOp",EDGE,"E49.trimOffspring"),sQuery(id+"F3.wireOp",EDGE,"E50.1.0"),sQuery(id+"F3.wireOp",EDGE,"E50.1.1"),sQuery(id+"F3.wireOp",EDGE,"E50.1.5"),sQuery(id+"F3.wireOp",EDGE,"E50.1.6"),sQuery(id+"F3.wireOp",EDGE,"E50.1.8"),sQuery(id+"F3.wireOp",EDGE,"E50.1.10"),sQuery(id+"F3.wireOp",EDGE,"E50.2.0"),sQuery(id+"F3.wireOp",EDGE,"E50.2.1"),sQuery(id+"F3.wireOp",EDGE,"E50.2.5"),sQuery(id+"F3.wireOp",EDGE,"E50.2.6"),sQuery(id+"F3.wireOp",EDGE,"E50.2.8"),sQuery(id+"F3.wireOp",EDGE,"E50.2.10"),sQuery(id+"F3.wireOp",EDGE,"E50.3.0"),sQuery(id+"F3.wireOp",EDGE,"E50.3.1"),sQuery(id+"F3.wireOp",EDGE,"E50.3.5"),sQuery(id+"F3.wireOp",EDGE,"E50.3.6"),sQuery(id+"F3.wireOp",EDGE,"E50.3.8"),sQuery(id+"F3.wireOp",EDGE,"E50.3.10"),sQuery(id+"F3.wireOp",EDGE,"E50.4.0"),sQuery(id+"F3.wireOp",EDGE,"E50.4.1"),sQuery(id+"F3.wireOp",EDGE,"E50.4.5"),sQuery(id+"F3.wireOp",EDGE,"E50.4.6"),sQuery(id+"F3.wireOp",EDGE,"E50.4.8"),sQuery(id+"F3.wireOp",EDGE,"E50.4.10"),sQuery(id+"F3.wireOp",EDGE,"E50.5.0"),sQuery(id+"F3.wireOp",EDGE,"E50.5.1"),sQuery(id+"F3.wireOp",EDGE,"E50.5.5"),sQuery(id+"F3.wireOp",EDGE,"E50.5.6"),sQuery(id+"F3.wireOp",EDGE,"E50.5.8"),sQuery(id+"F3.wireOp",EDGE,"E50.5.10"),sQuery(id+"F3.wireOp",EDGE,"E50.6.0"),sQuery(id+"F3.wireOp",EDGE,"E50.6.1"),sQuery(id+"F3.wireOp",EDGE,"E50.6.5"),sQuery(id+"F3.wireOp",EDGE,"E50.6.6"),sQuery(id+"F3.wireOp",EDGE,"E50.6.8"),sQuery(id+"F3.wireOp",EDGE,"E50.6.10"),sQuery(id+"F3.wireOp",EDGE,"E50.7.0"),sQuery(id+"F3.wireOp",EDGE,"E50.7.1"),sQuery(id+"F3.wireOp",EDGE,"E50.7.5"),sQuery(id+"F3.wireOp",EDGE,"E50.7.6"),sQuery(id+"F3.wireOp",EDGE,"E50.7.8"),sQuery(id+"F3.wireOp",EDGE,"E50.7.10"),sQuery(id+"F3.wireOp",EDGE,"E50.8.0"),sQuery(id+"F3.wireOp",EDGE,"E50.8.1"),sQuery(id+"F3.wireOp",EDGE,"E50.8.5"),sQuery(id+"F3.wireOp",EDGE,"E50.8.6"),sQuery(id+"F3.wireOp",EDGE,"E50.8.8"),sQuery(id+"F3.wireOp",EDGE,"E50.8.10"),sQuery(id+"F3.wireOp",EDGE,"E51.trimOffspring"),sQuery(id+"F3.wireOp",EDGE,"E52.trimOffspring"),sQuery(id+"F3.wireOp",EDGE,"E53.trimOffspring"),sQuery(id+"F3.wireOp",EDGE,"E54.trimOffspring"),sQuery(id+"F3.wireOp",EDGE,"E55.trimOffspring"),sQuery(id+"F3.wireOp",EDGE,"E56.trimOffspring"),sQuery(id+"F3.wireOp",EDGE,"E57.trimOffspring"),sQuery(id+"F3.wireOp",EDGE,"E58.trimOffspring"),sQuery(id+"F3.wireOp",EDGE,"E59.trimOffspring"),sQuery(id+"F3.wireOp",EDGE,"E60.trimOffspring"),sQuery(id+"F3.wireOp",EDGE,"E61.trimOffspring"),sQuery(id+"F3.wireOp",EDGE,"E62.trimOffspring"),sQuery(id+"F3.wireOp",EDGE,"E63.trimOffspring"),sQuery(id+"F3.wireOp",EDGE,"E64.trimOffspring"),sQuery(id+"F3.wireOp",EDGE,"E65.trimOffspring"),sQuery(id+"F3.wireOp",EDGE,"E66.trimOffspring"),sQuery(id+"F3.wireOp",EDGE,"E67.trimOffspring"),sQuery(id+"F3.wireOp",EDGE,"E68.trimOffspring"),sQuery(id+"F3.wireOp",EDGE,"E69.trimOffspring"),sQuery(id+"F3.wireOp",EDGE,"E70.trimOffspring"),sQuery(id+"F3.wireOp",EDGE,"E71.trimOffspring"),sQuery(id+"F3.wireOp",EDGE,"E72.trimOffspring"),sQuery(id+"F3.wireOp",EDGE,"E73.trimOffspring"),sQuery(id+"F3.wireOp",EDGE,"E74.trimOffspring"),sQuery(id+"F3.wireOp",EDGE,"E75.trimOffspring"),sQuery(id+"F3.wireOp",EDGE,"E76.trimOffspring"),sQuery(id+"F3.wireOp",EDGE,"E77.trimOffspring"),sQuery(id+"F3.wireOp",EDGE,"E78.trimOffspring"),sQuery(id+"F3.wireOp",EDGE,"E79.trimOffspring"),sQuery(id+"F3.wireOp",EDGE,"E80.trimOffspring"),sQuery(id+"F3.wireOp",EDGE,"E81.trimOffspring"),sQuery(id+"F3.wireOp",EDGE,"E82.trimOffspring"),sQuery(id+"F3.wireOp",EDGE,"E83.trimOffspring"),sQuery(id+"F3.wireOp",EDGE,"E84.trimOffspring"),sQuery(id+"F3.wireOp",EDGE,"E85.trimOffspring"),sQuery(id+"F3.wireOp",EDGE,"E86.trimOffspring")])],"isStart":false})]});}
            var sketch = newSketch(context, id + "F5", { "sketchPlane" : qUnion([Q0])});
            skLineSegment(sketch, "E87", {"start": v(0, 1.2) * mm, "end": v(0, -52.24) * mm});
            skLineSegment(sketch, "E88", {"start": v(0, -52.24) * mm, "end": v(3.8, -52.24) * mm});
            skLineSegment(sketch, "E89", {"start": v(0, -52.24) * mm, "end": v(-3.81, -52.24) * mm});
            skArc(sketch, "E90", {"start": v(-3.81, -52.24) * mm, "mid": v(-2.42, -49.93) * mm, "end": v(-1.14, -47.56) * mm});
            skArc(sketch, "E91.0", {"start": v(-2.1, -53.33) * mm, "mid": v(-1.02, -51.57) * mm, "end": v(0, -49.77) * mm});
            skLineSegment(sketch, "E92", {"start": v(-2.1, -53.33) * mm, "end": v(-3.81, -52.24) * mm});
            skLineSegment(sketch, "E93", {"start": v(2.1, -53.33) * mm, "end": v(3.8, -52.24) * mm});
            skArc(sketch, "E94.trimOffspring", {"start": v(0, -45.2) * mm, "mid": v(4.44, -29.94) * mm, "end": v(4.44, -14.04) * mm});
            skArc(sketch, "E95.trimOffspring", {"start": v(1.14, -47.56) * mm, "mid": v(2.42, -49.93) * mm, "end": v(3.8, -52.24) * mm});
            skArc(sketch, "E96.trimOffspring", {"start": v(1.14, -47.56) * mm, "mid": v(5.99, -33.02) * mm, "end": v(6.88, -17.71) * mm});
            skArc(sketch, "E97.trimOffspring", {"start": v(0, -49.77) * mm, "mid": v(1.02, -51.57) * mm, "end": v(2.1, -53.33) * mm});
            skArc(sketch, "E98.1.0", {"start": v(32.2, -35.43) * mm, "mid": v(26.58, -21.17) * mm, "end": v(17.42, -8.87) * mm});
            skArc(sketch, "E98.1.1", {"start": v(29.82, -34.35) * mm, "mid": v(23.42, -19.8) * mm, "end": v(13.2, -7.62) * mm});
            skArc(sketch, "E98.1.5", {"start": v(32.2, -35.43) * mm, "mid": v(34.71, -36.42) * mm, "end": v(37.26, -37.29) * mm});
            skArc(sketch, "E98.1.6", {"start": v(32.76, -37.85) * mm, "mid": v(34.7, -38.57) * mm, "end": v(36.65, -39.23) * mm});
            skLineSegment(sketch, "E98.1.7", {"start": v(36.65, -39.23) * mm, "end": v(37.26, -37.29) * mm});
            skArc(sketch, "E98.1.8", {"start": v(33.44, -41.92) * mm, "mid": v(33.13, -39.88) * mm, "end": v(32.76, -37.85) * mm});
            skLineSegment(sketch, "E98.1.9", {"start": v(33.44, -41.92) * mm, "end": v(31.42, -42.19) * mm});
            skArc(sketch, "E98.1.10", {"start": v(31.42, -42.19) * mm, "mid": v(31.01, -39.53) * mm, "end": v(30.47, -36.89) * mm});
            skArc(sketch, "E98.2.0", {"start": v(48.21, -6.16) * mm, "mid": v(34.73, 1.15) * mm, "end": v(19.81, 4.68) * mm});
            skArc(sketch, "E98.2.1", {"start": v(45.69, -6.87) * mm, "mid": v(31.43, 0.16) * mm, "end": v(15.77, 2.92) * mm});
            skArc(sketch, "E98.2.5", {"start": v(48.21, -6.16) * mm, "mid": v(50.77, -5.3) * mm, "end": v(53.28, -4.33) * mm});
            skArc(sketch, "E98.2.6", {"start": v(50.19, -7.66) * mm, "mid": v(52.13, -6.97) * mm, "end": v(54.06, -6.21) * mm});
            skLineSegment(sketch, "E98.2.7", {"start": v(54.06, -6.21) * mm, "end": v(53.28, -4.33) * mm});
            skArc(sketch, "E98.2.8", {"start": v(53.33, -10.34) * mm, "mid": v(51.78, -8.97) * mm, "end": v(50.19, -7.66) * mm});
            skLineSegment(sketch, "E98.2.9", {"start": v(53.33, -10.34) * mm, "end": v(51.96, -11.84) * mm});
            skArc(sketch, "E98.2.10", {"start": v(51.96, -11.84) * mm, "mid": v(49.93, -10.07) * mm, "end": v(47.82, -8.4) * mm});
            skArc(sketch, "E98.3.0", {"start": v(41.65, 26.55) * mm, "mid": v(26.63, 23.48) * mm, "end": v(12.93, 16.6) * mm});
            skArc(sketch, "E98.3.1", {"start": v(40.18, 24.39) * mm, "mid": v(24.74, 20.6) * mm, "end": v(10.97, 12.65) * mm});
            skArc(sketch, "E98.3.5", {"start": v(41.65, 26.55) * mm, "mid": v(43.07, 28.85) * mm, "end": v(44.37, 31.2) * mm});
            skArc(sketch, "E98.3.6", {"start": v(44.13, 26.67) * mm, "mid": v(45.18, 28.45) * mm, "end": v(46.17, 30.27) * mm});
            skLineSegment(sketch, "E98.3.7", {"start": v(46.17, 30.27) * mm, "end": v(44.37, 31.2) * mm});
            skArc(sketch, "E98.3.8", {"start": v(48.26, 26.64) * mm, "mid": v(46.2, 26.7) * mm, "end": v(44.13, 26.67) * mm});
            skLineSegment(sketch, "E98.3.9", {"start": v(48.26, 26.64) * mm, "end": v(48.18, 24.6) * mm});
            skArc(sketch, "E98.3.10", {"start": v(48.18, 24.6) * mm, "mid": v(45.48, 24.66) * mm, "end": v(42.79, 24.58) * mm});
            skArc(sketch, "E98.4.0", {"start": v(15.6, 47.4) * mm, "mid": v(6.07, 35.39) * mm, "end": v(0, 21.31) * mm});
            skArc(sketch, "E98.4.1", {"start": v(15.87, 44.79) * mm, "mid": v(6.47, 31.96) * mm, "end": v(1.04, 17.02) * mm});
            skArc(sketch, "E98.4.5", {"start": v(15.6, 47.4) * mm, "mid": v(15.21, 50.06) * mm, "end": v(14.7, 52.7) * mm});
            skArc(sketch, "E98.4.6", {"start": v(17.43, 49.08) * mm, "mid": v(17.09, 51.12) * mm, "end": v(16.68, 53.14) * mm});
            skLineSegment(sketch, "E98.4.7", {"start": v(16.68, 53.14) * mm, "end": v(14.7, 52.7) * mm});
            skArc(sketch, "E98.4.8", {"start": v(20.62, 51.7) * mm, "mid": v(19, 50.42) * mm, "end": v(17.43, 49.08) * mm});
            skLineSegment(sketch, "E98.4.9", {"start": v(20.62, 51.7) * mm, "end": v(21.85, 50.1) * mm});
            skArc(sketch, "E98.4.10", {"start": v(21.85, 50.1) * mm, "mid": v(19.76, 48.4) * mm, "end": v(17.74, 46.62) * mm});
            skArc(sketch, "E98.5.0", {"start": v(-17.74, 46.62) * mm, "mid": v(-17.33, 31.3) * mm, "end": v(-12.93, 16.6) * mm});
            skArc(sketch, "E98.5.1", {"start": v(-15.87, 44.79) * mm, "mid": v(-14.82, 28.92) * mm, "end": v(-9.38, 13.99) * mm});
            skArc(sketch, "E98.5.5", {"start": v(-17.74, 46.62) * mm, "mid": v(-19.76, 48.4) * mm, "end": v(-21.85, 50.1) * mm});
            skArc(sketch, "E98.5.6", {"start": v(-17.43, 49.08) * mm, "mid": v(-19, 50.42) * mm, "end": v(-20.62, 51.7) * mm});
            skLineSegment(sketch, "E98.5.7", {"start": v(-20.62, 51.7) * mm, "end": v(-21.85, 50.1) * mm});
            skArc(sketch, "E98.5.8", {"start": v(-16.68, 53.14) * mm, "mid": v(-17.09, 51.12) * mm, "end": v(-17.43, 49.08) * mm});
            skLineSegment(sketch, "E98.5.9", {"start": v(-16.68, 53.14) * mm, "end": v(-14.7, 52.7) * mm});
            skArc(sketch, "E98.5.10", {"start": v(-14.7, 52.7) * mm, "mid": v(-15.21, 50.06) * mm, "end": v(-15.6, 47.4) * mm});
            skArc(sketch, "E98.6.0", {"start": v(-42.8, 24.58) * mm, "mid": v(-32.62, 13.11) * mm, "end": v(-19.81, 4.68) * mm});
            skArc(sketch, "E98.6.1", {"start": v(-40.18, 24.39) * mm, "mid": v(-29.18, 12.9) * mm, "end": v(-15.41, 4.96) * mm});
            skArc(sketch, "E98.6.5", {"start": v(-42.8, 24.58) * mm, "mid": v(-45.48, 24.66) * mm, "end": v(-48.18, 24.6) * mm});
            skArc(sketch, "E98.6.6", {"start": v(-44.13, 26.67) * mm, "mid": v(-46.2, 26.7) * mm, "end": v(-48.27, 26.64) * mm});
            skLineSegment(sketch, "E98.6.7", {"start": v(-48.27, 26.64) * mm, "end": v(-48.18, 24.6) * mm});
            skArc(sketch, "E98.6.8", {"start": v(-46.17, 30.27) * mm, "mid": v(-45.18, 28.45) * mm, "end": v(-44.13, 26.67) * mm});
            skLineSegment(sketch, "E98.6.9", {"start": v(-46.17, 30.27) * mm, "end": v(-44.37, 31.2) * mm});
            skArc(sketch, "E98.6.10", {"start": v(-44.37, 31.2) * mm, "mid": v(-43.07, 28.85) * mm, "end": v(-41.65, 26.55) * mm});
            skArc(sketch, "E98.7.0", {"start": v(-47.82, -8.4) * mm, "mid": v(-32.65, -10.65) * mm, "end": v(-17.42, -8.87) * mm});
            skArc(sketch, "E98.7.1", {"start": v(-45.69, -6.87) * mm, "mid": v(-29.89, -8.6) * mm, "end": v(-14.23, -5.83) * mm});
            skArc(sketch, "E98.7.5", {"start": v(-47.82, -8.4) * mm, "mid": v(-49.93, -10.07) * mm, "end": v(-51.96, -11.84) * mm});
            skArc(sketch, "E98.7.6", {"start": v(-50.19, -7.66) * mm, "mid": v(-51.78, -8.97) * mm, "end": v(-53.33, -10.34) * mm});
            skLineSegment(sketch, "E98.7.7", {"start": v(-53.33, -10.34) * mm, "end": v(-51.96, -11.84) * mm});
            skArc(sketch, "E98.7.8", {"start": v(-54.06, -6.21) * mm, "mid": v(-52.13, -6.97) * mm, "end": v(-50.19, -7.66) * mm});
            skLineSegment(sketch, "E98.7.9", {"start": v(-54.06, -6.21) * mm, "end": v(-53.28, -4.33) * mm});
            skArc(sketch, "E98.7.10", {"start": v(-53.28, -4.33) * mm, "mid": v(-50.77, -5.3) * mm, "end": v(-48.21, -6.16) * mm});
            skArc(sketch, "E98.8.0", {"start": v(-30.47, -36.89) * mm, "mid": v(-17.4, -28.87) * mm, "end": v(-6.88, -17.71) * mm});
            skArc(sketch, "E98.8.1", {"start": v(-29.82, -34.35) * mm, "mid": v(-16.6, -25.51) * mm, "end": v(-6.4, -13.33) * mm});
            skArc(sketch, "E98.8.5", {"start": v(-30.47, -36.89) * mm, "mid": v(-31.01, -39.53) * mm, "end": v(-31.42, -42.19) * mm});
            skArc(sketch, "E98.8.6", {"start": v(-32.76, -37.85) * mm, "mid": v(-33.13, -39.88) * mm, "end": v(-33.44, -41.92) * mm});
            skLineSegment(sketch, "E98.8.7", {"start": v(-33.44, -41.92) * mm, "end": v(-31.42, -42.19) * mm});
            skArc(sketch, "E98.8.8", {"start": v(-36.65, -39.23) * mm, "mid": v(-34.7, -38.57) * mm, "end": v(-32.76, -37.85) * mm});
            skLineSegment(sketch, "E98.8.9", {"start": v(-36.65, -39.23) * mm, "end": v(-37.26, -37.29) * mm});
            skArc(sketch, "E98.8.10", {"start": v(-37.26, -37.29) * mm, "mid": v(-34.71, -36.42) * mm, "end": v(-32.2, -35.43) * mm});
            skArc(sketch, "E99.trimOffspring", {"start": v(-17.42, -8.87) * mm, "mid": v(-26.58, -21.17) * mm, "end": v(-32.2, -35.43) * mm});
            skArc(sketch, "E100.trimOffspring", {"start": v(-13.2, -7.62) * mm, "mid": v(-8.55, -5.84) * mm, "end": v(-4.08, -3.67) * mm});
            skArc(sketch, "E101.trimOffspring", {"start": v(-13.2, -7.62) * mm, "mid": v(-23.42, -19.8) * mm, "end": v(-29.82, -34.35) * mm});
            skArc(sketch, "E102.trimOffspring", {"start": v(-15.77, 2.92) * mm, "mid": v(-11.07, 1.3) * mm, "end": v(-6.25, 0.09) * mm});
            skArc(sketch, "E103.trimOffspring", {"start": v(-19.81, 4.68) * mm, "mid": v(-34.73, 1.15) * mm, "end": v(-48.21, -6.16) * mm});
            skArc(sketch, "E104.trimOffspring", {"start": v(-15.77, 2.92) * mm, "mid": v(-31.43, 0.16) * mm, "end": v(-45.69, -6.87) * mm});
            skArc(sketch, "E105.trimOffspring", {"start": v(-10.97, 12.65) * mm, "mid": v(-24.74, 20.6) * mm, "end": v(-40.18, 24.39) * mm});
            skArc(sketch, "E106.trimOffspring", {"start": v(-12.93, 16.6) * mm, "mid": v(-26.63, 23.48) * mm, "end": v(-41.65, 26.55) * mm});
            skArc(sketch, "E107.trimOffspring", {"start": v(-10.97, 12.65) * mm, "mid": v(-8.41, 8.4) * mm, "end": v(-5.5, 4.36) * mm});
            skArc(sketch, "E108.trimOffspring", {"start": v(-1.04, 17.02) * mm, "mid": v(-6.47, 31.96) * mm, "end": v(-15.87, 44.79) * mm});
            skArc(sketch, "E109.trimOffspring", {"start": v(-1.04, 17.02) * mm, "mid": v(-1.81, 12.11) * mm, "end": v(-2.17, 7.15) * mm});
            skArc(sketch, "E110.trimOffspring", {"start": v(0, 21.31) * mm, "mid": v(-6.07, 35.39) * mm, "end": v(-15.6, 47.4) * mm});
            skArc(sketch, "E111.trimOffspring", {"start": v(9.38, 13.99) * mm, "mid": v(14.82, 28.92) * mm, "end": v(15.87, 44.79) * mm});
            skArc(sketch, "E112.trimOffspring", {"start": v(9.38, 13.99) * mm, "mid": v(5.63, 10.72) * mm, "end": v(2.17, 7.15) * mm});
            skArc(sketch, "E113.trimOffspring", {"start": v(12.93, 16.6) * mm, "mid": v(17.33, 31.3) * mm, "end": v(17.74, 46.62) * mm});
            skArc(sketch, "E114.trimOffspring", {"start": v(19.81, 4.68) * mm, "mid": v(32.62, 13.11) * mm, "end": v(42.79, 24.58) * mm});
            skArc(sketch, "E115.trimOffspring", {"start": v(15.41, 4.96) * mm, "mid": v(10.44, 4.87) * mm, "end": v(5.5, 4.36) * mm});
            skArc(sketch, "E116.trimOffspring", {"start": v(15.41, 4.96) * mm, "mid": v(29.18, 12.9) * mm, "end": v(40.18, 24.39) * mm});
            skArc(sketch, "E117.trimOffspring", {"start": v(14.23, -5.83) * mm, "mid": v(29.89, -8.6) * mm, "end": v(45.69, -6.87) * mm});
            skArc(sketch, "E118.trimOffspring", {"start": v(17.42, -8.87) * mm, "mid": v(32.65, -10.65) * mm, "end": v(47.82, -8.4) * mm});
            skArc(sketch, "E119.trimOffspring", {"start": v(14.23, -5.83) * mm, "mid": v(10.37, -2.7) * mm, "end": v(6.25, 0.09) * mm});
            skArc(sketch, "E120.trimOffspring", {"start": v(6.88, -17.71) * mm, "mid": v(17.4, -28.87) * mm, "end": v(30.47, -36.89) * mm});
            skArc(sketch, "E121.trimOffspring", {"start": v(6.4, -13.33) * mm, "mid": v(5.44, -8.45) * mm, "end": v(4.08, -3.67) * mm});
            skArc(sketch, "E122.trimOffspring", {"start": v(6.4, -13.33) * mm, "mid": v(16.6, -25.51) * mm, "end": v(29.82, -34.35) * mm});
            skArc(sketch, "E123.trimOffspring", {"start": v(-4.44, -14.04) * mm, "mid": v(-4.45, -29.94) * mm, "end": v(0, -45.2) * mm});
            skArc(sketch, "E124.trimOffspring", {"start": v(-4.44, -14.04) * mm, "mid": v(-2.03, -9.7) * mm, "end": v(0, -5.15) * mm});
            skArc(sketch, "E125.trimOffspring", {"start": v(-6.88, -17.71) * mm, "mid": v(-5.99, -33.02) * mm, "end": v(-1.14, -47.56) * mm});
            skArc(sketch, "E126.trimOffspring", {"start": v(-6.25, 0.09) * mm, "mid": v(-10.37, -2.7) * mm, "end": v(-14.23, -5.83) * mm});
            skArc(sketch, "E127.trimOffspring", {"start": v(-4.08, -3.67) * mm, "mid": v(-5.44, -8.45) * mm, "end": v(-6.4, -13.33) * mm});
            skArc(sketch, "E128.trimOffspring", {"start": v(0, -5.15) * mm, "mid": v(2.03, -9.7) * mm, "end": v(4.44, -14.04) * mm});
            skArc(sketch, "E129.trimOffspring", {"start": v(4.08, -3.67) * mm, "mid": v(8.55, -5.84) * mm, "end": v(13.2, -7.62) * mm});
            skArc(sketch, "E130.trimOffspring", {"start": v(6.25, 0.09) * mm, "mid": v(11.07, 1.3) * mm, "end": v(15.77, 2.92) * mm});
            skArc(sketch, "E131.trimOffspring", {"start": v(5.5, 4.36) * mm, "mid": v(8.41, 8.4) * mm, "end": v(10.97, 12.65) * mm});
            skArc(sketch, "E132.trimOffspring", {"start": v(2.17, 7.15) * mm, "mid": v(1.81, 12.11) * mm, "end": v(1.04, 17.02) * mm});
            skArc(sketch, "E133.trimOffspring", {"start": v(-2.17, 7.15) * mm, "mid": v(-5.63, 10.72) * mm, "end": v(-9.38, 13.99) * mm});
            skArc(sketch, "E134.trimOffspring", {"start": v(-5.5, 4.36) * mm, "mid": v(-10.44, 4.87) * mm, "end": v(-15.41, 4.96) * mm});
            skSolve(sketch);
        }
        {
            var Q0;
            Q0=qSketchRegion(id+"F5",true);
            extrude(context, id + "F6", {"entities" : qUnion([Q0]), "operationType" : NewBodyOperationType.ADD, "oppositeDirection" : true, "depth" : 5.08 * mm});
        }
        {
            var Q0;
            {var subQ0=sQuery(id+"F0.wireOp",EDGE,"E15");Q0=makeQuery(id+"F6.boolean.opBoolean","MERGE",FACE,{"derivedFrom":[makeQuery(id+"F4.boolean.opBoolean","MERGE",FACE,{"derivedFrom":[makeQuery(id+"F2.opChamfer","SPLIT",FACE,{"disambiguationData":[OD(18.0)],"derivedFrom":makeQuery(id+"F1.opExtrude","CAP_FACE",FACE,{"disambiguationData":[OSD([sQuery(id+"F0.wireOp",EDGE,"E12.1.0"),sQuery(id+"F0.wireOp",EDGE,"E12.1.1"),sQuery(id+"F0.wireOp",EDGE,"E12.1.2"),sQuery(id+"F0.wireOp",EDGE,"E12.1.3"),sQuery(id+"F0.wireOp",EDGE,"E12.1.4"),sQuery(id+"F0.wireOp",EDGE,"E12.1.5"),sQuery(id+"F0.wireOp",EDGE,"E12.1.6"),sQuery(id+"F0.wireOp",EDGE,"E12.1.7"),sQuery(id+"F0.wireOp",EDGE,"E12.1.10"),sQuery(id+"F0.wireOp",EDGE,"E12.1.11"),sQuery(id+"F0.wireOp",EDGE,"E12.2.0"),sQuery(id+"F0.wireOp",EDGE,"E12.2.1"),sQuery(id+"F0.wireOp",EDGE,"E12.2.2"),sQuery(id+"F0.wireOp",EDGE,"E12.2.3"),sQuery(id+"F0.wireOp",EDGE,"E12.2.4"),sQuery(id+"F0.wireOp",EDGE,"E12.2.5"),sQuery(id+"F0.wireOp",EDGE,"E12.2.6"),sQuery(id+"F0.wireOp",EDGE,"E12.2.7"),sQuery(id+"F0.wireOp",EDGE,"E12.2.10"),sQuery(id+"F0.wireOp",EDGE,"E12.2.11"),sQuery(id+"F0.wireOp",EDGE,"E12.3.0"),sQuery(id+"F0.wireOp",EDGE,"E12.3.1"),sQuery(id+"F0.wireOp",EDGE,"E12.3.2"),sQuery(id+"F0.wireOp",EDGE,"E12.3.3"),sQuery(id+"F0.wireOp",EDGE,"E12.3.4"),sQuery(id+"F0.wireOp",EDGE,"E12.3.5"),sQuery(id+"F0.wireOp",EDGE,"E12.3.6"),sQuery(id+"F0.wireOp",EDGE,"E12.3.7"),sQuery(id+"F0.wireOp",EDGE,"E12.3.10"),sQuery(id+"F0.wireOp",EDGE,"E12.3.11"),sQuery(id+"F0.wireOp",EDGE,"E12.4.0"),sQuery(id+"F0.wireOp",EDGE,"E12.4.1"),sQuery(id+"F0.wireOp",EDGE,"E12.4.2"),sQuery(id+"F0.wireOp",EDGE,"E12.4.3"),sQuery(id+"F0.wireOp",EDGE,"E12.4.4"),sQuery(id+"F0.wireOp",EDGE,"E12.4.5"),sQuery(id+"F0.wireOp",EDGE,"E12.4.6"),sQuery(id+"F0.wireOp",EDGE,"E12.4.7"),sQuery(id+"F0.wireOp",EDGE,"E12.4.10"),sQuery(id+"F0.wireOp",EDGE,"E12.4.11"),sQuery(id+"F0.wireOp",EDGE,"E12.5.0"),sQuery(id+"F0.wireOp",EDGE,"E12.5.1"),sQuery(id+"F0.wireOp",EDGE,"E12.5.2"),sQuery(id+"F0.wireOp",EDGE,"E12.5.3"),sQuery(id+"F0.wireOp",EDGE,"E12.5.4"),sQuery(id+"F0.wireOp",EDGE,"E12.5.5"),sQuery(id+"F0.wireOp",EDGE,"E12.5.6"),sQuery(id+"F0.wireOp",EDGE,"E12.5.7"),sQuery(id+"F0.wireOp",EDGE,"E12.5.10"),sQuery(id+"F0.wireOp",EDGE,"E12.5.11"),sQuery(id+"F0.wireOp",EDGE,"E12.6.0"),sQuery(id+"F0.wireOp",EDGE,"E12.6.1"),sQuery(id+"F0.wireOp",EDGE,"E12.6.2"),sQuery(id+"F0.wireOp",EDGE,"E12.6.3"),sQuery(id+"F0.wireOp",EDGE,"E12.6.4"),sQuery(id+"F0.wireOp",EDGE,"E12.6.5"),sQuery(id+"F0.wireOp",EDGE,"E12.6.6"),sQuery(id+"F0.wireOp",EDGE,"E12.6.7"),sQuery(id+"F0.wireOp",EDGE,"E12.6.10"),sQuery(id+"F0.wireOp",EDGE,"E12.6.11"),sQuery(id+"F0.wireOp",EDGE,"E12.7.0"),sQuery(id+"F0.wireOp",EDGE,"E12.7.1"),sQuery(id+"F0.wireOp",EDGE,"E12.7.2"),sQuery(id+"F0.wireOp",EDGE,"E12.7.3"),sQuery(id+"F0.wireOp",EDGE,"E12.7.4"),sQuery(id+"F0.wireOp",EDGE,"E12.7.5"),sQuery(id+"F0.wireOp",EDGE,"E12.7.6"),sQuery(id+"F0.wireOp",EDGE,"E12.7.7"),sQuery(id+"F0.wireOp",EDGE,"E12.7.10"),sQuery(id+"F0.wireOp",EDGE,"E12.7.11"),sQuery(id+"F0.wireOp",EDGE,"E12.8.0"),sQuery(id+"F0.wireOp",EDGE,"E12.8.1"),sQuery(id+"F0.wireOp",EDGE,"E12.8.2"),sQuery(id+"F0.wireOp",EDGE,"E12.8.3"),sQuery(id+"F0.wireOp",EDGE,"E12.8.4"),sQuery(id+"F0.wireOp",EDGE,"E12.8.5"),sQuery(id+"F0.wireOp",EDGE,"E12.8.6"),sQuery(id+"F0.wireOp",EDGE,"E12.8.7"),sQuery(id+"F0.wireOp",EDGE,"E12.8.10"),sQuery(id+"F0.wireOp",EDGE,"E12.8.11"),sQuery(id+"F0.wireOp",EDGE,"E12.9.0"),sQuery(id+"F0.wireOp",EDGE,"E12.9.1"),sQuery(id+"F0.wireOp",EDGE,"E12.9.2"),sQuery(id+"F0.wireOp",EDGE,"E12.9.3"),sQuery(id+"F0.wireOp",EDGE,"E12.9.4"),sQuery(id+"F0.wireOp",EDGE,"E12.9.5"),sQuery(id+"F0.wireOp",EDGE,"E12.9.6"),sQuery(id+"F0.wireOp",EDGE,"E12.9.7"),sQuery(id+"F0.wireOp",EDGE,"E12.9.10"),sQuery(id+"F0.wireOp",EDGE,"E12.9.11"),sQuery(id+"F0.wireOp",EDGE,"E13.1.0"),sQuery(id+"F0.wireOp",EDGE,"E13.1.1"),sQuery(id+"F0.wireOp",EDGE,"E13.1.2"),sQuery(id+"F0.wireOp",EDGE,"E13.1.5"),sQuery(id+"F0.wireOp",EDGE,"E13.1.6"),sQuery(id+"F0.wireOp",EDGE,"E13.1.7"),sQuery(id+"F0.wireOp",EDGE,"E13.1.8"),sQuery(id+"F0.wireOp",EDGE,"E13.1.9"),sQuery(id+"F0.wireOp",EDGE,"E13.1.10"),sQuery(id+"F0.wireOp",EDGE,"E13.1.11"),sQuery(id+"F0.wireOp",EDGE,"E13.2.0"),sQuery(id+"F0.wireOp",EDGE,"E13.2.1"),sQuery(id+"F0.wireOp",EDGE,"E13.2.2"),sQuery(id+"F0.wireOp",EDGE,"E13.2.5"),sQuery(id+"F0.wireOp",EDGE,"E13.2.6"),sQuery(id+"F0.wireOp",EDGE,"E13.2.7"),sQuery(id+"F0.wireOp",EDGE,"E13.2.8"),sQuery(id+"F0.wireOp",EDGE,"E13.2.9"),sQuery(id+"F0.wireOp",EDGE,"E13.2.10"),sQuery(id+"F0.wireOp",EDGE,"E13.2.11"),sQuery(id+"F0.wireOp",EDGE,"E13.3.0"),sQuery(id+"F0.wireOp",EDGE,"E13.3.1"),sQuery(id+"F0.wireOp",EDGE,"E13.3.2"),sQuery(id+"F0.wireOp",EDGE,"E13.3.5"),sQuery(id+"F0.wireOp",EDGE,"E13.3.6"),sQuery(id+"F0.wireOp",EDGE,"E13.3.7"),sQuery(id+"F0.wireOp",EDGE,"E13.3.8"),sQuery(id+"F0.wireOp",EDGE,"E13.3.9"),sQuery(id+"F0.wireOp",EDGE,"E13.3.10"),sQuery(id+"F0.wireOp",EDGE,"E13.3.11"),sQuery(id+"F0.wireOp",EDGE,"E13.4.0"),sQuery(id+"F0.wireOp",EDGE,"E13.4.1"),sQuery(id+"F0.wireOp",EDGE,"E13.4.2"),sQuery(id+"F0.wireOp",EDGE,"E13.4.5"),sQuery(id+"F0.wireOp",EDGE,"E13.4.6"),sQuery(id+"F0.wireOp",EDGE,"E13.4.7"),sQuery(id+"F0.wireOp",EDGE,"E13.4.8"),sQuery(id+"F0.wireOp",EDGE,"E13.4.9"),sQuery(id+"F0.wireOp",EDGE,"E13.4.10"),sQuery(id+"F0.wireOp",EDGE,"E13.4.11"),sQuery(id+"F0.wireOp",EDGE,"E13.5.0"),sQuery(id+"F0.wireOp",EDGE,"E13.5.1"),sQuery(id+"F0.wireOp",EDGE,"E13.5.2"),sQuery(id+"F0.wireOp",EDGE,"E13.5.5"),sQuery(id+"F0.wireOp",EDGE,"E13.5.6"),sQuery(id+"F0.wireOp",EDGE,"E13.5.7"),sQuery(id+"F0.wireOp",EDGE,"E13.5.8"),sQuery(id+"F0.wireOp",EDGE,"E13.5.9"),sQuery(id+"F0.wireOp",EDGE,"E13.5.10"),sQuery(id+"F0.wireOp",EDGE,"E13.5.11"),sQuery(id+"F0.wireOp",EDGE,"E13.6.0"),sQuery(id+"F0.wireOp",EDGE,"E13.6.1"),sQuery(id+"F0.wireOp",EDGE,"E13.6.2"),sQuery(id+"F0.wireOp",EDGE,"E13.6.5"),sQuery(id+"F0.wireOp",EDGE,"E13.6.6"),sQuery(id+"F0.wireOp",EDGE,"E13.6.7"),sQuery(id+"F0.wireOp",EDGE,"E13.6.8"),sQuery(id+"F0.wireOp",EDGE,"E13.6.9"),sQuery(id+"F0.wireOp",EDGE,"E13.6.10"),sQuery(id+"F0.wireOp",EDGE,"E13.6.11"),sQuery(id+"F0.wireOp",EDGE,"E13.7.0"),sQuery(id+"F0.wireOp",EDGE,"E13.7.1"),sQuery(id+"F0.wireOp",EDGE,"E13.7.2"),sQuery(id+"F0.wireOp",EDGE,"E13.7.5"),sQuery(id+"F0.wireOp",EDGE,"E13.7.6"),sQuery(id+"F0.wireOp",EDGE,"E13.7.7"),sQuery(id+"F0.wireOp",EDGE,"E13.7.8"),sQuery(id+"F0.wireOp",EDGE,"E13.7.9"),sQuery(id+"F0.wireOp",EDGE,"E13.7.10"),sQuery(id+"F0.wireOp",EDGE,"E13.7.11"),sQuery(id+"F0.wireOp",EDGE,"E13.8.0"),sQuery(id+"F0.wireOp",EDGE,"E13.8.1"),sQuery(id+"F0.wireOp",EDGE,"E13.8.2"),sQuery(id+"F0.wireOp",EDGE,"E13.8.5"),sQuery(id+"F0.wireOp",EDGE,"E13.8.6"),sQuery(id+"F0.wireOp",EDGE,"E13.8.7"),sQuery(id+"F0.wireOp",EDGE,"E13.8.8"),sQuery(id+"F0.wireOp",EDGE,"E13.8.9"),sQuery(id+"F0.wireOp",EDGE,"E13.8.10"),sQuery(id+"F0.wireOp",EDGE,"E13.8.11"),sQuery(id+"F0.wireOp",EDGE,"E3"),sQuery(id+"F0.wireOp",EDGE,"E2"),sQuery(id+"F0.wireOp",EDGE,"E1"),sQuery(id+"F0.wireOp",EDGE,"E4"),sQuery(id+"F0.wireOp",EDGE,"E8"),sQuery(id+"F0.wireOp",EDGE,"E5"),sQuery(id+"F0.wireOp",EDGE,"E11"),sQuery(id+"F0.wireOp",EDGE,"E6"),sQuery(id+"F0.wireOp",EDGE,"E7"),sQuery(id+"F0.wireOp",EDGE,"E10"),sQuery(id+"F0.wireOp",EDGE,"E14"),subQ0,sQuery(id+"F0.wireOp",EDGE,"E20.trimOffspring"),sQuery(id+"F0.wireOp",EDGE,"E21.trimOffspring"),sQuery(id+"F0.wireOp",EDGE,"E22.trimOffspring"),sQuery(id+"F0.wireOp",EDGE,"E23.trimOffspring"),sQuery(id+"F0.wireOp",EDGE,"E24.trimOffspring"),sQuery(id+"F0.wireOp",EDGE,"E25.trimOffspring"),sQuery(id+"F0.wireOp",EDGE,"E26.trimOffspring"),sQuery(id+"F0.wireOp",EDGE,"E27.trimOffspring"),sQuery(id+"F0.wireOp",EDGE,"E28.trimOffspring"),sQuery(id+"F0.wireOp",EDGE,"E29.trimOffspring"),sQuery(id+"F0.wireOp",EDGE,"E30.trimOffspring"),sQuery(id+"F0.wireOp",EDGE,"E31.trimOffspring"),sQuery(id+"F0.wireOp",EDGE,"E32.trimOffspring"),sQuery(id+"F0.wireOp",EDGE,"E33.trimOffspring"),sQuery(id+"F0.wireOp",EDGE,"E34.trimOffspring"),sQuery(id+"F0.wireOp",EDGE,"E35.trimOffspring"),sQuery(id+"F0.wireOp",EDGE,"E36.trimOffspring"),sQuery(id+"F0.wireOp",EDGE,"E37")])],"isStart":false})}),makeQuery(id+"F4.opExtrude","CAP_FACE",FACE,{"disambiguationData":[OSD([subQ0,sQuery(id+"F3.wireOp",EDGE,"E42"),sQuery(id+"F3.wireOp",EDGE,"E43.0"),sQuery(id+"F3.wireOp",EDGE,"E46.trimOffspring"),sQuery(id+"F3.wireOp",EDGE,"E47.trimOffspring"),sQuery(id+"F3.wireOp",EDGE,"E48.trimOffspring"),sQuery(id+"F3.wireOp",EDGE,"E49.trimOffspring"),sQuery(id+"F3.wireOp",EDGE,"E50.1.0"),sQuery(id+"F3.wireOp",EDGE,"E50.1.1"),sQuery(id+"F3.wireOp",EDGE,"E50.1.5"),sQuery(id+"F3.wireOp",EDGE,"E50.1.6"),sQuery(id+"F3.wireOp",EDGE,"E50.1.8"),sQuery(id+"F3.wireOp",EDGE,"E50.1.10"),sQuery(id+"F3.wireOp",EDGE,"E50.2.0"),sQuery(id+"F3.wireOp",EDGE,"E50.2.1"),sQuery(id+"F3.wireOp",EDGE,"E50.2.5"),sQuery(id+"F3.wireOp",EDGE,"E50.2.6"),sQuery(id+"F3.wireOp",EDGE,"E50.2.8"),sQuery(id+"F3.wireOp",EDGE,"E50.2.10"),sQuery(id+"F3.wireOp",EDGE,"E50.3.0"),sQuery(id+"F3.wireOp",EDGE,"E50.3.1"),sQuery(id+"F3.wireOp",EDGE,"E50.3.5"),sQuery(id+"F3.wireOp",EDGE,"E50.3.6"),sQuery(id+"F3.wireOp",EDGE,"E50.3.8"),sQuery(id+"F3.wireOp",EDGE,"E50.3.10"),sQuery(id+"F3.wireOp",EDGE,"E50.4.0"),sQuery(id+"F3.wireOp",EDGE,"E50.4.1"),sQuery(id+"F3.wireOp",EDGE,"E50.4.5"),sQuery(id+"F3.wireOp",EDGE,"E50.4.6"),sQuery(id+"F3.wireOp",EDGE,"E50.4.8"),sQuery(id+"F3.wireOp",EDGE,"E50.4.10"),sQuery(id+"F3.wireOp",EDGE,"E50.5.0"),sQuery(id+"F3.wireOp",EDGE,"E50.5.1"),sQuery(id+"F3.wireOp",EDGE,"E50.5.5"),sQuery(id+"F3.wireOp",EDGE,"E50.5.6"),sQuery(id+"F3.wireOp",EDGE,"E50.5.8"),sQuery(id+"F3.wireOp",EDGE,"E50.5.10"),sQuery(id+"F3.wireOp",EDGE,"E50.6.0"),sQuery(id+"F3.wireOp",EDGE,"E50.6.1"),sQuery(id+"F3.wireOp",EDGE,"E50.6.5"),sQuery(id+"F3.wireOp",EDGE,"E50.6.6"),sQuery(id+"F3.wireOp",EDGE,"E50.6.8"),sQuery(id+"F3.wireOp",EDGE,"E50.6.10"),sQuery(id+"F3.wireOp",EDGE,"E50.7.0"),sQuery(id+"F3.wireOp",EDGE,"E50.7.1"),sQuery(id+"F3.wireOp",EDGE,"E50.7.5"),sQuery(id+"F3.wireOp",EDGE,"E50.7.6"),sQuery(id+"F3.wireOp",EDGE,"E50.7.8"),sQuery(id+"F3.wireOp",EDGE,"E50.7.10"),sQuery(id+"F3.wireOp",EDGE,"E50.8.0"),sQuery(id+"F3.wireOp",EDGE,"E50.8.1"),sQuery(id+"F3.wireOp",EDGE,"E50.8.5"),sQuery(id+"F3.wireOp",EDGE,"E50.8.6"),sQuery(id+"F3.wireOp",EDGE,"E50.8.8"),sQuery(id+"F3.wireOp",EDGE,"E50.8.10"),sQuery(id+"F3.wireOp",EDGE,"E51.trimOffspring"),sQuery(id+"F3.wireOp",EDGE,"E52.trimOffspring"),sQuery(id+"F3.wireOp",EDGE,"E53.trimOffspring"),sQuery(id+"F3.wireOp",EDGE,"E54.trimOffspring"),sQuery(id+"F3.wireOp",EDGE,"E55.trimOffspring"),sQuery(id+"F3.wireOp",EDGE,"E56.trimOffspring"),sQuery(id+"F3.wireOp",EDGE,"E57.trimOffspring"),sQuery(id+"F3.wireOp",EDGE,"E58.trimOffspring"),sQuery(id+"F3.wireOp",EDGE,"E59.trimOffspring"),sQuery(id+"F3.wireOp",EDGE,"E60.trimOffspring"),sQuery(id+"F3.wireOp",EDGE,"E61.trimOffspring"),sQuery(id+"F3.wireOp",EDGE,"E62.trimOffspring"),sQuery(id+"F3.wireOp",EDGE,"E63.trimOffspring"),sQuery(id+"F3.wireOp",EDGE,"E64.trimOffspring"),sQuery(id+"F3.wireOp",EDGE,"E65.trimOffspring"),sQuery(id+"F3.wireOp",EDGE,"E66.trimOffspring"),sQuery(id+"F3.wireOp",EDGE,"E67.trimOffspring"),sQuery(id+"F3.wireOp",EDGE,"E68.trimOffspring"),sQuery(id+"F3.wireOp",EDGE,"E69.trimOffspring"),sQuery(id+"F3.wireOp",EDGE,"E70.trimOffspring"),sQuery(id+"F3.wireOp",EDGE,"E71.trimOffspring"),sQuery(id+"F3.wireOp",EDGE,"E72.trimOffspring"),sQuery(id+"F3.wireOp",EDGE,"E73.trimOffspring"),sQuery(id+"F3.wireOp",EDGE,"E74.trimOffspring"),sQuery(id+"F3.wireOp",EDGE,"E75.trimOffspring"),sQuery(id+"F3.wireOp",EDGE,"E76.trimOffspring"),sQuery(id+"F3.wireOp",EDGE,"E77.trimOffspring"),sQuery(id+"F3.wireOp",EDGE,"E78.trimOffspring"),sQuery(id+"F3.wireOp",EDGE,"E79.trimOffspring"),sQuery(id+"F3.wireOp",EDGE,"E80.trimOffspring"),sQuery(id+"F3.wireOp",EDGE,"E81.trimOffspring"),sQuery(id+"F3.wireOp",EDGE,"E82.trimOffspring"),sQuery(id+"F3.wireOp",EDGE,"E83.trimOffspring"),sQuery(id+"F3.wireOp",EDGE,"E84.trimOffspring"),sQuery(id+"F3.wireOp",EDGE,"E85.trimOffspring"),sQuery(id+"F3.wireOp",EDGE,"E86.trimOffspring")])],"isStart":false})]}),makeQuery(id+"F6.opExtrude","CAP_FACE",FACE,{"disambiguationData":[OSD([sQuery(id+"F5.wireOp",EDGE,"E88"),sQuery(id+"F5.wireOp",EDGE,"E89"),sQuery(id+"F5.wireOp",EDGE,"E90"),sQuery(id+"F5.wireOp",EDGE,"E91.0"),sQuery(id+"F5.wireOp",EDGE,"E92"),sQuery(id+"F5.wireOp",EDGE,"E93"),sQuery(id+"F5.wireOp",EDGE,"E94.trimOffspring"),sQuery(id+"F5.wireOp",EDGE,"E95.trimOffspring"),sQuery(id+"F5.wireOp",EDGE,"E96.trimOffspring"),sQuery(id+"F5.wireOp",EDGE,"E97.trimOffspring"),sQuery(id+"F5.wireOp",EDGE,"E98.1.0"),sQuery(id+"F5.wireOp",EDGE,"E98.1.1"),sQuery(id+"F5.wireOp",EDGE,"E98.1.5"),sQuery(id+"F5.wireOp",EDGE,"E98.1.6"),sQuery(id+"F5.wireOp",EDGE,"E98.1.7"),sQuery(id+"F5.wireOp",EDGE,"E98.1.8"),sQuery(id+"F5.wireOp",EDGE,"E98.1.9"),sQuery(id+"F5.wireOp",EDGE,"E98.1.10"),sQuery(id+"F5.wireOp",EDGE,"E98.2.0"),sQuery(id+"F5.wireOp",EDGE,"E98.2.1"),sQuery(id+"F5.wireOp",EDGE,"E98.2.5"),sQuery(id+"F5.wireOp",EDGE,"E98.2.6"),sQuery(id+"F5.wireOp",EDGE,"E98.2.7"),sQuery(id+"F5.wireOp",EDGE,"E98.2.8"),sQuery(id+"F5.wireOp",EDGE,"E98.2.9"),sQuery(id+"F5.wireOp",EDGE,"E98.2.10"),sQuery(id+"F5.wireOp",EDGE,"E98.3.0"),sQuery(id+"F5.wireOp",EDGE,"E98.3.1"),sQuery(id+"F5.wireOp",EDGE,"E98.3.5"),sQuery(id+"F5.wireOp",EDGE,"E98.3.6"),sQuery(id+"F5.wireOp",EDGE,"E98.3.7"),sQuery(id+"F5.wireOp",EDGE,"E98.3.8"),sQuery(id+"F5.wireOp",EDGE,"E98.3.9"),sQuery(id+"F5.wireOp",EDGE,"E98.3.10"),sQuery(id+"F5.wireOp",EDGE,"E98.4.0"),sQuery(id+"F5.wireOp",EDGE,"E98.4.1"),sQuery(id+"F5.wireOp",EDGE,"E98.4.5"),sQuery(id+"F5.wireOp",EDGE,"E98.4.6"),sQuery(id+"F5.wireOp",EDGE,"E98.4.7"),sQuery(id+"F5.wireOp",EDGE,"E98.4.8"),sQuery(id+"F5.wireOp",EDGE,"E98.4.9"),sQuery(id+"F5.wireOp",EDGE,"E98.4.10"),sQuery(id+"F5.wireOp",EDGE,"E98.5.0"),sQuery(id+"F5.wireOp",EDGE,"E98.5.1"),sQuery(id+"F5.wireOp",EDGE,"E98.5.5"),sQuery(id+"F5.wireOp",EDGE,"E98.5.6"),sQuery(id+"F5.wireOp",EDGE,"E98.5.7"),sQuery(id+"F5.wireOp",EDGE,"E98.5.8"),sQuery(id+"F5.wireOp",EDGE,"E98.5.9"),sQuery(id+"F5.wireOp",EDGE,"E98.5.10"),sQuery(id+"F5.wireOp",EDGE,"E98.6.0"),sQuery(id+"F5.wireOp",EDGE,"E98.6.1"),sQuery(id+"F5.wireOp",EDGE,"E98.6.5"),sQuery(id+"F5.wireOp",EDGE,"E98.6.6"),sQuery(id+"F5.wireOp",EDGE,"E98.6.7"),sQuery(id+"F5.wireOp",EDGE,"E98.6.8"),sQuery(id+"F5.wireOp",EDGE,"E98.6.9"),sQuery(id+"F5.wireOp",EDGE,"E98.6.10"),sQuery(id+"F5.wireOp",EDGE,"E98.7.0"),sQuery(id+"F5.wireOp",EDGE,"E98.7.1"),sQuery(id+"F5.wireOp",EDGE,"E98.7.5"),sQuery(id+"F5.wireOp",EDGE,"E98.7.6"),sQuery(id+"F5.wireOp",EDGE,"E98.7.7"),sQuery(id+"F5.wireOp",EDGE,"E98.7.8"),sQuery(id+"F5.wireOp",EDGE,"E98.7.9"),sQuery(id+"F5.wireOp",EDGE,"E98.7.10"),sQuery(id+"F5.wireOp",EDGE,"E98.8.0"),sQuery(id+"F5.wireOp",EDGE,"E98.8.1"),sQuery(id+"F5.wireOp",EDGE,"E98.8.5"),sQuery(id+"F5.wireOp",EDGE,"E98.8.6"),sQuery(id+"F5.wireOp",EDGE,"E98.8.7"),sQuery(id+"F5.wireOp",EDGE,"E98.8.8"),sQuery(id+"F5.wireOp",EDGE,"E98.8.9"),sQuery(id+"F5.wireOp",EDGE,"E98.8.10"),sQuery(id+"F5.wireOp",EDGE,"E99.trimOffspring"),sQuery(id+"F5.wireOp",EDGE,"E100.trimOffspring"),sQuery(id+"F5.wireOp",EDGE,"E101.trimOffspring"),sQuery(id+"F5.wireOp",EDGE,"E102.trimOffspring"),sQuery(id+"F5.wireOp",EDGE,"E103.trimOffspring"),sQuery(id+"F5.wireOp",EDGE,"E104.trimOffspring"),sQuery(id+"F5.wireOp",EDGE,"E105.trimOffspring"),sQuery(id+"F5.wireOp",EDGE,"E106.trimOffspring"),sQuery(id+"F5.wireOp",EDGE,"E107.trimOffspring"),sQuery(id+"F5.wireOp",EDGE,"E108.trimOffspring"),sQuery(id+"F5.wireOp",EDGE,"E109.trimOffspring"),sQuery(id+"F5.wireOp",EDGE,"E110.trimOffspring"),sQuery(id+"F5.wireOp",EDGE,"E111.trimOffspring"),sQuery(id+"F5.wireOp",EDGE,"E112.trimOffspring"),sQuery(id+"F5.wireOp",EDGE,"E113.trimOffspring"),sQuery(id+"F5.wireOp",EDGE,"E114.trimOffspring"),sQuery(id+"F5.wireOp",EDGE,"E115.trimOffspring"),sQuery(id+"F5.wireOp",EDGE,"E116.trimOffspring"),sQuery(id+"F5.wireOp",EDGE,"E117.trimOffspring"),sQuery(id+"F5.wireOp",EDGE,"E118.trimOffspring"),sQuery(id+"F5.wireOp",EDGE,"E119.trimOffspring"),sQuery(id+"F5.wireOp",EDGE,"E120.trimOffspring"),sQuery(id+"F5.wireOp",EDGE,"E121.trimOffspring"),sQuery(id+"F5.wireOp",EDGE,"E122.trimOffspring"),sQuery(id+"F5.wireOp",EDGE,"E123.trimOffspring"),sQuery(id+"F5.wireOp",EDGE,"E124.trimOffspring"),sQuery(id+"F5.wireOp",EDGE,"E125.trimOffspring"),sQuery(id+"F5.wireOp",EDGE,"E126.trimOffspring"),sQuery(id+"F5.wireOp",EDGE,"E127.trimOffspring"),sQuery(id+"F5.wireOp",EDGE,"E128.trimOffspring"),sQuery(id+"F5.wireOp",EDGE,"E129.trimOffspring"),sQuery(id+"F5.wireOp",EDGE,"E130.trimOffspring"),sQuery(id+"F5.wireOp",EDGE,"E131.trimOffspring"),sQuery(id+"F5.wireOp",EDGE,"E132.trimOffspring"),sQuery(id+"F5.wireOp",EDGE,"E133.trimOffspring"),sQuery(id+"F5.wireOp",EDGE,"E134.trimOffspring")])],"isStart":true})]});}
            var sketch = newSketch(context, id + "F7", { "sketchPlane" : qUnion([Q0])});
            skCircle(sketch, "E135", {"center": v(0, 0) * mm, "radius": 55.24 * mm});
            skCircle(sketch, "E136", {"center": v(0, 0) * mm, "radius": 47.58 * mm});
            skCircle(sketch, "E137", {"center": v(0, 0) * mm, "radius": 49.27 * mm});
            skSolve(sketch);
        }
        {
            var Q0;
            Q0=qSketchRegion(id+"F7",true);
            extrude(context, id + "F8", {"entities" : qUnion([Q0]), "operationType" : NewBodyOperationType.ADD, "oppositeDirection" : true, "depth" : 5.08 * mm});
        }
        {
            var Q0;
            {var subQ0=sQuery(id+"F0.wireOp",EDGE,"E15");Q0=makeQuery(id+"F8.boolean.opBoolean","MERGE",FACE,{"derivedFrom":[makeQuery(id+"F6.boolean.opBoolean","MERGE",FACE,{"derivedFrom":[makeQuery(id+"F4.boolean.opBoolean","MERGE",FACE,{"derivedFrom":[makeQuery(id+"F2.opChamfer","SPLIT",FACE,{"disambiguationData":[OD(18.0)],"derivedFrom":makeQuery(id+"F1.opExtrude","CAP_FACE",FACE,{"disambiguationData":[OSD([sQuery(id+"F0.wireOp",EDGE,"E12.1.0"),sQuery(id+"F0.wireOp",EDGE,"E12.1.1"),sQuery(id+"F0.wireOp",EDGE,"E12.1.2"),sQuery(id+"F0.wireOp",EDGE,"E12.1.3"),sQuery(id+"F0.wireOp",EDGE,"E12.1.4"),sQuery(id+"F0.wireOp",EDGE,"E12.1.5"),sQuery(id+"F0.wireOp",EDGE,"E12.1.6"),sQuery(id+"F0.wireOp",EDGE,"E12.1.7"),sQuery(id+"F0.wireOp",EDGE,"E12.1.10"),sQuery(id+"F0.wireOp",EDGE,"E12.1.11"),sQuery(id+"F0.wireOp",EDGE,"E12.2.0"),sQuery(id+"F0.wireOp",EDGE,"E12.2.1"),sQuery(id+"F0.wireOp",EDGE,"E12.2.2"),sQuery(id+"F0.wireOp",EDGE,"E12.2.3"),sQuery(id+"F0.wireOp",EDGE,"E12.2.4"),sQuery(id+"F0.wireOp",EDGE,"E12.2.5"),sQuery(id+"F0.wireOp",EDGE,"E12.2.6"),sQuery(id+"F0.wireOp",EDGE,"E12.2.7"),sQuery(id+"F0.wireOp",EDGE,"E12.2.10"),sQuery(id+"F0.wireOp",EDGE,"E12.2.11"),sQuery(id+"F0.wireOp",EDGE,"E12.3.0"),sQuery(id+"F0.wireOp",EDGE,"E12.3.1"),sQuery(id+"F0.wireOp",EDGE,"E12.3.2"),sQuery(id+"F0.wireOp",EDGE,"E12.3.3"),sQuery(id+"F0.wireOp",EDGE,"E12.3.4"),sQuery(id+"F0.wireOp",EDGE,"E12.3.5"),sQuery(id+"F0.wireOp",EDGE,"E12.3.6"),sQuery(id+"F0.wireOp",EDGE,"E12.3.7"),sQuery(id+"F0.wireOp",EDGE,"E12.3.10"),sQuery(id+"F0.wireOp",EDGE,"E12.3.11"),sQuery(id+"F0.wireOp",EDGE,"E12.4.0"),sQuery(id+"F0.wireOp",EDGE,"E12.4.1"),sQuery(id+"F0.wireOp",EDGE,"E12.4.2"),sQuery(id+"F0.wireOp",EDGE,"E12.4.3"),sQuery(id+"F0.wireOp",EDGE,"E12.4.4"),sQuery(id+"F0.wireOp",EDGE,"E12.4.5"),sQuery(id+"F0.wireOp",EDGE,"E12.4.6"),sQuery(id+"F0.wireOp",EDGE,"E12.4.7"),sQuery(id+"F0.wireOp",EDGE,"E12.4.10"),sQuery(id+"F0.wireOp",EDGE,"E12.4.11"),sQuery(id+"F0.wireOp",EDGE,"E12.5.0"),sQuery(id+"F0.wireOp",EDGE,"E12.5.1"),sQuery(id+"F0.wireOp",EDGE,"E12.5.2"),sQuery(id+"F0.wireOp",EDGE,"E12.5.3"),sQuery(id+"F0.wireOp",EDGE,"E12.5.4"),sQuery(id+"F0.wireOp",EDGE,"E12.5.5"),sQuery(id+"F0.wireOp",EDGE,"E12.5.6"),sQuery(id+"F0.wireOp",EDGE,"E12.5.7"),sQuery(id+"F0.wireOp",EDGE,"E12.5.10"),sQuery(id+"F0.wireOp",EDGE,"E12.5.11"),sQuery(id+"F0.wireOp",EDGE,"E12.6.0"),sQuery(id+"F0.wireOp",EDGE,"E12.6.1"),sQuery(id+"F0.wireOp",EDGE,"E12.6.2"),sQuery(id+"F0.wireOp",EDGE,"E12.6.3"),sQuery(id+"F0.wireOp",EDGE,"E12.6.4"),sQuery(id+"F0.wireOp",EDGE,"E12.6.5"),sQuery(id+"F0.wireOp",EDGE,"E12.6.6"),sQuery(id+"F0.wireOp",EDGE,"E12.6.7"),sQuery(id+"F0.wireOp",EDGE,"E12.6.10"),sQuery(id+"F0.wireOp",EDGE,"E12.6.11"),sQuery(id+"F0.wireOp",EDGE,"E12.7.0"),sQuery(id+"F0.wireOp",EDGE,"E12.7.1"),sQuery(id+"F0.wireOp",EDGE,"E12.7.2"),sQuery(id+"F0.wireOp",EDGE,"E12.7.3"),sQuery(id+"F0.wireOp",EDGE,"E12.7.4"),sQuery(id+"F0.wireOp",EDGE,"E12.7.5"),sQuery(id+"F0.wireOp",EDGE,"E12.7.6"),sQuery(id+"F0.wireOp",EDGE,"E12.7.7"),sQuery(id+"F0.wireOp",EDGE,"E12.7.10"),sQuery(id+"F0.wireOp",EDGE,"E12.7.11"),sQuery(id+"F0.wireOp",EDGE,"E12.8.0"),sQuery(id+"F0.wireOp",EDGE,"E12.8.1"),sQuery(id+"F0.wireOp",EDGE,"E12.8.2"),sQuery(id+"F0.wireOp",EDGE,"E12.8.3"),sQuery(id+"F0.wireOp",EDGE,"E12.8.4"),sQuery(id+"F0.wireOp",EDGE,"E12.8.5"),sQuery(id+"F0.wireOp",EDGE,"E12.8.6"),sQuery(id+"F0.wireOp",EDGE,"E12.8.7"),sQuery(id+"F0.wireOp",EDGE,"E12.8.10"),sQuery(id+"F0.wireOp",EDGE,"E12.8.11"),sQuery(id+"F0.wireOp",EDGE,"E12.9.0"),sQuery(id+"F0.wireOp",EDGE,"E12.9.1"),sQuery(id+"F0.wireOp",EDGE,"E12.9.2"),sQuery(id+"F0.wireOp",EDGE,"E12.9.3"),sQuery(id+"F0.wireOp",EDGE,"E12.9.4"),sQuery(id+"F0.wireOp",EDGE,"E12.9.5"),sQuery(id+"F0.wireOp",EDGE,"E12.9.6"),sQuery(id+"F0.wireOp",EDGE,"E12.9.7"),sQuery(id+"F0.wireOp",EDGE,"E12.9.10"),sQuery(id+"F0.wireOp",EDGE,"E12.9.11"),sQuery(id+"F0.wireOp",EDGE,"E13.1.0"),sQuery(id+"F0.wireOp",EDGE,"E13.1.1"),sQuery(id+"F0.wireOp",EDGE,"E13.1.2"),sQuery(id+"F0.wireOp",EDGE,"E13.1.5"),sQuery(id+"F0.wireOp",EDGE,"E13.1.6"),sQuery(id+"F0.wireOp",EDGE,"E13.1.7"),sQuery(id+"F0.wireOp",EDGE,"E13.1.8"),sQuery(id+"F0.wireOp",EDGE,"E13.1.9"),sQuery(id+"F0.wireOp",EDGE,"E13.1.10"),sQuery(id+"F0.wireOp",EDGE,"E13.1.11"),sQuery(id+"F0.wireOp",EDGE,"E13.2.0"),sQuery(id+"F0.wireOp",EDGE,"E13.2.1"),sQuery(id+"F0.wireOp",EDGE,"E13.2.2"),sQuery(id+"F0.wireOp",EDGE,"E13.2.5"),sQuery(id+"F0.wireOp",EDGE,"E13.2.6"),sQuery(id+"F0.wireOp",EDGE,"E13.2.7"),sQuery(id+"F0.wireOp",EDGE,"E13.2.8"),sQuery(id+"F0.wireOp",EDGE,"E13.2.9"),sQuery(id+"F0.wireOp",EDGE,"E13.2.10"),sQuery(id+"F0.wireOp",EDGE,"E13.2.11"),sQuery(id+"F0.wireOp",EDGE,"E13.3.0"),sQuery(id+"F0.wireOp",EDGE,"E13.3.1"),sQuery(id+"F0.wireOp",EDGE,"E13.3.2"),sQuery(id+"F0.wireOp",EDGE,"E13.3.5"),sQuery(id+"F0.wireOp",EDGE,"E13.3.6"),sQuery(id+"F0.wireOp",EDGE,"E13.3.7"),sQuery(id+"F0.wireOp",EDGE,"E13.3.8"),sQuery(id+"F0.wireOp",EDGE,"E13.3.9"),sQuery(id+"F0.wireOp",EDGE,"E13.3.10"),sQuery(id+"F0.wireOp",EDGE,"E13.3.11"),sQuery(id+"F0.wireOp",EDGE,"E13.4.0"),sQuery(id+"F0.wireOp",EDGE,"E13.4.1"),sQuery(id+"F0.wireOp",EDGE,"E13.4.2"),sQuery(id+"F0.wireOp",EDGE,"E13.4.5"),sQuery(id+"F0.wireOp",EDGE,"E13.4.6"),sQuery(id+"F0.wireOp",EDGE,"E13.4.7"),sQuery(id+"F0.wireOp",EDGE,"E13.4.8"),sQuery(id+"F0.wireOp",EDGE,"E13.4.9"),sQuery(id+"F0.wireOp",EDGE,"E13.4.10"),sQuery(id+"F0.wireOp",EDGE,"E13.4.11"),sQuery(id+"F0.wireOp",EDGE,"E13.5.0"),sQuery(id+"F0.wireOp",EDGE,"E13.5.1"),sQuery(id+"F0.wireOp",EDGE,"E13.5.2"),sQuery(id+"F0.wireOp",EDGE,"E13.5.5"),sQuery(id+"F0.wireOp",EDGE,"E13.5.6"),sQuery(id+"F0.wireOp",EDGE,"E13.5.7"),sQuery(id+"F0.wireOp",EDGE,"E13.5.8"),sQuery(id+"F0.wireOp",EDGE,"E13.5.9"),sQuery(id+"F0.wireOp",EDGE,"E13.5.10"),sQuery(id+"F0.wireOp",EDGE,"E13.5.11"),sQuery(id+"F0.wireOp",EDGE,"E13.6.0"),sQuery(id+"F0.wireOp",EDGE,"E13.6.1"),sQuery(id+"F0.wireOp",EDGE,"E13.6.2"),sQuery(id+"F0.wireOp",EDGE,"E13.6.5"),sQuery(id+"F0.wireOp",EDGE,"E13.6.6"),sQuery(id+"F0.wireOp",EDGE,"E13.6.7"),sQuery(id+"F0.wireOp",EDGE,"E13.6.8"),sQuery(id+"F0.wireOp",EDGE,"E13.6.9"),sQuery(id+"F0.wireOp",EDGE,"E13.6.10"),sQuery(id+"F0.wireOp",EDGE,"E13.6.11"),sQuery(id+"F0.wireOp",EDGE,"E13.7.0"),sQuery(id+"F0.wireOp",EDGE,"E13.7.1"),sQuery(id+"F0.wireOp",EDGE,"E13.7.2"),sQuery(id+"F0.wireOp",EDGE,"E13.7.5"),sQuery(id+"F0.wireOp",EDGE,"E13.7.6"),sQuery(id+"F0.wireOp",EDGE,"E13.7.7"),sQuery(id+"F0.wireOp",EDGE,"E13.7.8"),sQuery(id+"F0.wireOp",EDGE,"E13.7.9"),sQuery(id+"F0.wireOp",EDGE,"E13.7.10"),sQuery(id+"F0.wireOp",EDGE,"E13.7.11"),sQuery(id+"F0.wireOp",EDGE,"E13.8.0"),sQuery(id+"F0.wireOp",EDGE,"E13.8.1"),sQuery(id+"F0.wireOp",EDGE,"E13.8.2"),sQuery(id+"F0.wireOp",EDGE,"E13.8.5"),sQuery(id+"F0.wireOp",EDGE,"E13.8.6"),sQuery(id+"F0.wireOp",EDGE,"E13.8.7"),sQuery(id+"F0.wireOp",EDGE,"E13.8.8"),sQuery(id+"F0.wireOp",EDGE,"E13.8.9"),sQuery(id+"F0.wireOp",EDGE,"E13.8.10"),sQuery(id+"F0.wireOp",EDGE,"E13.8.11"),sQuery(id+"F0.wireOp",EDGE,"E3"),sQuery(id+"F0.wireOp",EDGE,"E2"),sQuery(id+"F0.wireOp",EDGE,"E1"),sQuery(id+"F0.wireOp",EDGE,"E4"),sQuery(id+"F0.wireOp",EDGE,"E8"),sQuery(id+"F0.wireOp",EDGE,"E5"),sQuery(id+"F0.wireOp",EDGE,"E11"),sQuery(id+"F0.wireOp",EDGE,"E6"),sQuery(id+"F0.wireOp",EDGE,"E7"),sQuery(id+"F0.wireOp",EDGE,"E10"),sQuery(id+"F0.wireOp",EDGE,"E14"),subQ0,sQuery(id+"F0.wireOp",EDGE,"E20.trimOffspring"),sQuery(id+"F0.wireOp",EDGE,"E21.trimOffspring"),sQuery(id+"F0.wireOp",EDGE,"E22.trimOffspring"),sQuery(id+"F0.wireOp",EDGE,"E23.trimOffspring"),sQuery(id+"F0.wireOp",EDGE,"E24.trimOffspring"),sQuery(id+"F0.wireOp",EDGE,"E25.trimOffspring"),sQuery(id+"F0.wireOp",EDGE,"E26.trimOffspring"),sQuery(id+"F0.wireOp",EDGE,"E27.trimOffspring"),sQuery(id+"F0.wireOp",EDGE,"E28.trimOffspring"),sQuery(id+"F0.wireOp",EDGE,"E29.trimOffspring"),sQuery(id+"F0.wireOp",EDGE,"E30.trimOffspring"),sQuery(id+"F0.wireOp",EDGE,"E31.trimOffspring"),sQuery(id+"F0.wireOp",EDGE,"E32.trimOffspring"),sQuery(id+"F0.wireOp",EDGE,"E33.trimOffspring"),sQuery(id+"F0.wireOp",EDGE,"E34.trimOffspring"),sQuery(id+"F0.wireOp",EDGE,"E35.trimOffspring"),sQuery(id+"F0.wireOp",EDGE,"E36.trimOffspring"),sQuery(id+"F0.wireOp",EDGE,"E37")])],"isStart":false})}),makeQuery(id+"F4.opExtrude","CAP_FACE",FACE,{"disambiguationData":[OSD([subQ0,sQuery(id+"F3.wireOp",EDGE,"E42"),sQuery(id+"F3.wireOp",EDGE,"E43.0"),sQuery(id+"F3.wireOp",EDGE,"E46.trimOffspring"),sQuery(id+"F3.wireOp",EDGE,"E47.trimOffspring"),sQuery(id+"F3.wireOp",EDGE,"E48.trimOffspring"),sQuery(id+"F3.wireOp",EDGE,"E49.trimOffspring"),sQuery(id+"F3.wireOp",EDGE,"E50.1.0"),sQuery(id+"F3.wireOp",EDGE,"E50.1.1"),sQuery(id+"F3.wireOp",EDGE,"E50.1.5"),sQuery(id+"F3.wireOp",EDGE,"E50.1.6"),sQuery(id+"F3.wireOp",EDGE,"E50.1.8"),sQuery(id+"F3.wireOp",EDGE,"E50.1.10"),sQuery(id+"F3.wireOp",EDGE,"E50.2.0"),sQuery(id+"F3.wireOp",EDGE,"E50.2.1"),sQuery(id+"F3.wireOp",EDGE,"E50.2.5"),sQuery(id+"F3.wireOp",EDGE,"E50.2.6"),sQuery(id+"F3.wireOp",EDGE,"E50.2.8"),sQuery(id+"F3.wireOp",EDGE,"E50.2.10"),sQuery(id+"F3.wireOp",EDGE,"E50.3.0"),sQuery(id+"F3.wireOp",EDGE,"E50.3.1"),sQuery(id+"F3.wireOp",EDGE,"E50.3.5"),sQuery(id+"F3.wireOp",EDGE,"E50.3.6"),sQuery(id+"F3.wireOp",EDGE,"E50.3.8"),sQuery(id+"F3.wireOp",EDGE,"E50.3.10"),sQuery(id+"F3.wireOp",EDGE,"E50.4.0"),sQuery(id+"F3.wireOp",EDGE,"E50.4.1"),sQuery(id+"F3.wireOp",EDGE,"E50.4.5"),sQuery(id+"F3.wireOp",EDGE,"E50.4.6"),sQuery(id+"F3.wireOp",EDGE,"E50.4.8"),sQuery(id+"F3.wireOp",EDGE,"E50.4.10"),sQuery(id+"F3.wireOp",EDGE,"E50.5.0"),sQuery(id+"F3.wireOp",EDGE,"E50.5.1"),sQuery(id+"F3.wireOp",EDGE,"E50.5.5"),sQuery(id+"F3.wireOp",EDGE,"E50.5.6"),sQuery(id+"F3.wireOp",EDGE,"E50.5.8"),sQuery(id+"F3.wireOp",EDGE,"E50.5.10"),sQuery(id+"F3.wireOp",EDGE,"E50.6.0"),sQuery(id+"F3.wireOp",EDGE,"E50.6.1"),sQuery(id+"F3.wireOp",EDGE,"E50.6.5"),sQuery(id+"F3.wireOp",EDGE,"E50.6.6"),sQuery(id+"F3.wireOp",EDGE,"E50.6.8"),sQuery(id+"F3.wireOp",EDGE,"E50.6.10"),sQuery(id+"F3.wireOp",EDGE,"E50.7.0"),sQuery(id+"F3.wireOp",EDGE,"E50.7.1"),sQuery(id+"F3.wireOp",EDGE,"E50.7.5"),sQuery(id+"F3.wireOp",EDGE,"E50.7.6"),sQuery(id+"F3.wireOp",EDGE,"E50.7.8"),sQuery(id+"F3.wireOp",EDGE,"E50.7.10"),sQuery(id+"F3.wireOp",EDGE,"E50.8.0"),sQuery(id+"F3.wireOp",EDGE,"E50.8.1"),sQuery(id+"F3.wireOp",EDGE,"E50.8.5"),sQuery(id+"F3.wireOp",EDGE,"E50.8.6"),sQuery(id+"F3.wireOp",EDGE,"E50.8.8"),sQuery(id+"F3.wireOp",EDGE,"E50.8.10"),sQuery(id+"F3.wireOp",EDGE,"E51.trimOffspring"),sQuery(id+"F3.wireOp",EDGE,"E52.trimOffspring"),sQuery(id+"F3.wireOp",EDGE,"E53.trimOffspring"),sQuery(id+"F3.wireOp",EDGE,"E54.trimOffspring"),sQuery(id+"F3.wireOp",EDGE,"E55.trimOffspring"),sQuery(id+"F3.wireOp",EDGE,"E56.trimOffspring"),sQuery(id+"F3.wireOp",EDGE,"E57.trimOffspring"),sQuery(id+"F3.wireOp",EDGE,"E58.trimOffspring"),sQuery(id+"F3.wireOp",EDGE,"E59.trimOffspring"),sQuery(id+"F3.wireOp",EDGE,"E60.trimOffspring"),sQuery(id+"F3.wireOp",EDGE,"E61.trimOffspring"),sQuery(id+"F3.wireOp",EDGE,"E62.trimOffspring"),sQuery(id+"F3.wireOp",EDGE,"E63.trimOffspring"),sQuery(id+"F3.wireOp",EDGE,"E64.trimOffspring"),sQuery(id+"F3.wireOp",EDGE,"E65.trimOffspring"),sQuery(id+"F3.wireOp",EDGE,"E66.trimOffspring"),sQuery(id+"F3.wireOp",EDGE,"E67.trimOffspring"),sQuery(id+"F3.wireOp",EDGE,"E68.trimOffspring"),sQuery(id+"F3.wireOp",EDGE,"E69.trimOffspring"),sQuery(id+"F3.wireOp",EDGE,"E70.trimOffspring"),sQuery(id+"F3.wireOp",EDGE,"E71.trimOffspring"),sQuery(id+"F3.wireOp",EDGE,"E72.trimOffspring"),sQuery(id+"F3.wireOp",EDGE,"E73.trimOffspring"),sQuery(id+"F3.wireOp",EDGE,"E74.trimOffspring"),sQuery(id+"F3.wireOp",EDGE,"E75.trimOffspring"),sQuery(id+"F3.wireOp",EDGE,"E76.trimOffspring"),sQuery(id+"F3.wireOp",EDGE,"E77.trimOffspring"),sQuery(id+"F3.wireOp",EDGE,"E78.trimOffspring"),sQuery(id+"F3.wireOp",EDGE,"E79.trimOffspring"),sQuery(id+"F3.wireOp",EDGE,"E80.trimOffspring"),sQuery(id+"F3.wireOp",EDGE,"E81.trimOffspring"),sQuery(id+"F3.wireOp",EDGE,"E82.trimOffspring"),sQuery(id+"F3.wireOp",EDGE,"E83.trimOffspring"),sQuery(id+"F3.wireOp",EDGE,"E84.trimOffspring"),sQuery(id+"F3.wireOp",EDGE,"E85.trimOffspring"),sQuery(id+"F3.wireOp",EDGE,"E86.trimOffspring")])],"isStart":false})]}),makeQuery(id+"F6.opExtrude","CAP_FACE",FACE,{"disambiguationData":[OSD([sQuery(id+"F5.wireOp",EDGE,"E88"),sQuery(id+"F5.wireOp",EDGE,"E89"),sQuery(id+"F5.wireOp",EDGE,"E90"),sQuery(id+"F5.wireOp",EDGE,"E91.0"),sQuery(id+"F5.wireOp",EDGE,"E92"),sQuery(id+"F5.wireOp",EDGE,"E93"),sQuery(id+"F5.wireOp",EDGE,"E94.trimOffspring"),sQuery(id+"F5.wireOp",EDGE,"E95.trimOffspring"),sQuery(id+"F5.wireOp",EDGE,"E96.trimOffspring"),sQuery(id+"F5.wireOp",EDGE,"E97.trimOffspring"),sQuery(id+"F5.wireOp",EDGE,"E98.1.0"),sQuery(id+"F5.wireOp",EDGE,"E98.1.1"),sQuery(id+"F5.wireOp",EDGE,"E98.1.5"),sQuery(id+"F5.wireOp",EDGE,"E98.1.6"),sQuery(id+"F5.wireOp",EDGE,"E98.1.7"),sQuery(id+"F5.wireOp",EDGE,"E98.1.8"),sQuery(id+"F5.wireOp",EDGE,"E98.1.9"),sQuery(id+"F5.wireOp",EDGE,"E98.1.10"),sQuery(id+"F5.wireOp",EDGE,"E98.2.0"),sQuery(id+"F5.wireOp",EDGE,"E98.2.1"),sQuery(id+"F5.wireOp",EDGE,"E98.2.5"),sQuery(id+"F5.wireOp",EDGE,"E98.2.6"),sQuery(id+"F5.wireOp",EDGE,"E98.2.7"),sQuery(id+"F5.wireOp",EDGE,"E98.2.8"),sQuery(id+"F5.wireOp",EDGE,"E98.2.9"),sQuery(id+"F5.wireOp",EDGE,"E98.2.10"),sQuery(id+"F5.wireOp",EDGE,"E98.3.0"),sQuery(id+"F5.wireOp",EDGE,"E98.3.1"),sQuery(id+"F5.wireOp",EDGE,"E98.3.5"),sQuery(id+"F5.wireOp",EDGE,"E98.3.6"),sQuery(id+"F5.wireOp",EDGE,"E98.3.7"),sQuery(id+"F5.wireOp",EDGE,"E98.3.8"),sQuery(id+"F5.wireOp",EDGE,"E98.3.9"),sQuery(id+"F5.wireOp",EDGE,"E98.3.10"),sQuery(id+"F5.wireOp",EDGE,"E98.4.0"),sQuery(id+"F5.wireOp",EDGE,"E98.4.1"),sQuery(id+"F5.wireOp",EDGE,"E98.4.5"),sQuery(id+"F5.wireOp",EDGE,"E98.4.6"),sQuery(id+"F5.wireOp",EDGE,"E98.4.7"),sQuery(id+"F5.wireOp",EDGE,"E98.4.8"),sQuery(id+"F5.wireOp",EDGE,"E98.4.9"),sQuery(id+"F5.wireOp",EDGE,"E98.4.10"),sQuery(id+"F5.wireOp",EDGE,"E98.5.0"),sQuery(id+"F5.wireOp",EDGE,"E98.5.1"),sQuery(id+"F5.wireOp",EDGE,"E98.5.5"),sQuery(id+"F5.wireOp",EDGE,"E98.5.6"),sQuery(id+"F5.wireOp",EDGE,"E98.5.7"),sQuery(id+"F5.wireOp",EDGE,"E98.5.8"),sQuery(id+"F5.wireOp",EDGE,"E98.5.9"),sQuery(id+"F5.wireOp",EDGE,"E98.5.10"),sQuery(id+"F5.wireOp",EDGE,"E98.6.0"),sQuery(id+"F5.wireOp",EDGE,"E98.6.1"),sQuery(id+"F5.wireOp",EDGE,"E98.6.5"),sQuery(id+"F5.wireOp",EDGE,"E98.6.6"),sQuery(id+"F5.wireOp",EDGE,"E98.6.7"),sQuery(id+"F5.wireOp",EDGE,"E98.6.8"),sQuery(id+"F5.wireOp",EDGE,"E98.6.9"),sQuery(id+"F5.wireOp",EDGE,"E98.6.10"),sQuery(id+"F5.wireOp",EDGE,"E98.7.0"),sQuery(id+"F5.wireOp",EDGE,"E98.7.1"),sQuery(id+"F5.wireOp",EDGE,"E98.7.5"),sQuery(id+"F5.wireOp",EDGE,"E98.7.6"),sQuery(id+"F5.wireOp",EDGE,"E98.7.7"),sQuery(id+"F5.wireOp",EDGE,"E98.7.8"),sQuery(id+"F5.wireOp",EDGE,"E98.7.9"),sQuery(id+"F5.wireOp",EDGE,"E98.7.10"),sQuery(id+"F5.wireOp",EDGE,"E98.8.0"),sQuery(id+"F5.wireOp",EDGE,"E98.8.1"),sQuery(id+"F5.wireOp",EDGE,"E98.8.5"),sQuery(id+"F5.wireOp",EDGE,"E98.8.6"),sQuery(id+"F5.wireOp",EDGE,"E98.8.7"),sQuery(id+"F5.wireOp",EDGE,"E98.8.8"),sQuery(id+"F5.wireOp",EDGE,"E98.8.9"),sQuery(id+"F5.wireOp",EDGE,"E98.8.10"),sQuery(id+"F5.wireOp",EDGE,"E99.trimOffspring"),sQuery(id+"F5.wireOp",EDGE,"E100.trimOffspring"),sQuery(id+"F5.wireOp",EDGE,"E101.trimOffspring"),sQuery(id+"F5.wireOp",EDGE,"E102.trimOffspring"),sQuery(id+"F5.wireOp",EDGE,"E103.trimOffspring"),sQuery(id+"F5.wireOp",EDGE,"E104.trimOffspring"),sQuery(id+"F5.wireOp",EDGE,"E105.trimOffspring"),sQuery(id+"F5.wireOp",EDGE,"E106.trimOffspring"),sQuery(id+"F5.wireOp",EDGE,"E107.trimOffspring"),sQuery(id+"F5.wireOp",EDGE,"E108.trimOffspring"),sQuery(id+"F5.wireOp",EDGE,"E109.trimOffspring"),sQuery(id+"F5.wireOp",EDGE,"E110.trimOffspring"),sQuery(id+"F5.wireOp",EDGE,"E111.trimOffspring"),sQuery(id+"F5.wireOp",EDGE,"E112.trimOffspring"),sQuery(id+"F5.wireOp",EDGE,"E113.trimOffspring"),sQuery(id+"F5.wireOp",EDGE,"E114.trimOffspring"),sQuery(id+"F5.wireOp",EDGE,"E115.trimOffspring"),sQuery(id+"F5.wireOp",EDGE,"E116.trimOffspring"),sQuery(id+"F5.wireOp",EDGE,"E117.trimOffspring"),sQuery(id+"F5.wireOp",EDGE,"E118.trimOffspring"),sQuery(id+"F5.wireOp",EDGE,"E119.trimOffspring"),sQuery(id+"F5.wireOp",EDGE,"E120.trimOffspring"),sQuery(id+"F5.wireOp",EDGE,"E121.trimOffspring"),sQuery(id+"F5.wireOp",EDGE,"E122.trimOffspring"),sQuery(id+"F5.wireOp",EDGE,"E123.trimOffspring"),sQuery(id+"F5.wireOp",EDGE,"E124.trimOffspring"),sQuery(id+"F5.wireOp",EDGE,"E125.trimOffspring"),sQuery(id+"F5.wireOp",EDGE,"E126.trimOffspring"),sQuery(id+"F5.wireOp",EDGE,"E127.trimOffspring"),sQuery(id+"F5.wireOp",EDGE,"E128.trimOffspring"),sQuery(id+"F5.wireOp",EDGE,"E129.trimOffspring"),sQuery(id+"F5.wireOp",EDGE,"E130.trimOffspring"),sQuery(id+"F5.wireOp",EDGE,"E131.trimOffspring"),sQuery(id+"F5.wireOp",EDGE,"E132.trimOffspring"),sQuery(id+"F5.wireOp",EDGE,"E133.trimOffspring"),sQuery(id+"F5.wireOp",EDGE,"E134.trimOffspring")])],"isStart":true})]}),makeQuery(id+"F8.opExtrude","CAP_FACE",FACE,{"disambiguationData":[OSD([sQuery(id+"F7.wireOp",EDGE,"E135"),sQuery(id+"F7.wireOp",EDGE,"E137")])],"isStart":true})]});}
            var sketch = newSketch(context, id + "F9", { "sketchPlane" : qUnion([Q0])});
            skCircle(sketch, "E138", {"center": v(0, 0) * mm, "radius": 54.45 * mm});
            skCircle(sketch, "E139", {"center": v(0, 0) * mm, "radius": 51.6 * mm});
            skSolve(sketch);
        }
        {
            var Q0;
            Q0=qSketchRegion(id+"F9",true);
            extrude(context, id + "F10", {"entities" : qUnion([Q0]), "operationType" : NewBodyOperationType.REMOVE, "oppositeDirection" : true, "depth" : 25.4 * mm});
        }
        {
            var Q0;
            {var subQ0=sQuery(id+"F5.wireOp",EDGE,"E98.7.0");var subQ1=sQuery(id+"F5.wireOp",EDGE,"E98.6.0");var subQ2=sQuery(id+"F5.wireOp",EDGE,"E134.trimOffspring");var subQ3=sQuery(id+"F5.wireOp",EDGE,"E98.5.1");var subQ4=sQuery(id+"F5.wireOp",EDGE,"E98.3.0");var subQ5=sQuery(id+"F5.wireOp",EDGE,"E110.trimOffspring");var subQ6=sQuery(id+"F5.wireOp",EDGE,"E98.2.5");var subQ7=sQuery(id+"F5.wireOp",EDGE,"E98.2.0");var subQ8=sQuery(id+"F3.wireOp",EDGE,"E80.trimOffspring");var subQ9=sQuery(id+"F5.wireOp",EDGE,"E102.trimOffspring");var subQ10=sQuery(id+"F5.wireOp",EDGE,"E98.1.5");var subQ11=sQuery(id+"F5.wireOp",EDGE,"E98.4.0");var subQ12=sQuery(id+"F5.wireOp",EDGE,"E118.trimOffspring");var subQ13=sQuery(id+"F5.wireOp",EDGE,"E96.trimOffspring");var subQ14=sQuery(id+"F5.wireOp",EDGE,"E98.8.1");var subQ15=sQuery(id+"F5.wireOp",EDGE,"E94.trimOffspring");var subQ16=sQuery(id+"F5.wireOp",EDGE,"E90");var subQ17=sQuery(id+"F5.wireOp",EDGE,"E98.6.1");var subQ18=sQuery(id+"F3.wireOp",EDGE,"E42");var subQ19=sQuery(id+"F3.wireOp",EDGE,"E85.trimOffspring");var subQ20=sQuery(id+"F3.wireOp",EDGE,"E84.trimOffspring");var subQ21=sQuery(id+"F5.wireOp",EDGE,"E98.8.10");var subQ22=sQuery(id+"F3.wireOp",EDGE,"E83.trimOffspring");var subQ23=sQuery(id+"F3.wireOp",EDGE,"E82.trimOffspring");var subQ24=sQuery(id+"F3.wireOp",EDGE,"E81.trimOffspring");var subQ25=sQuery(id+"F3.wireOp",EDGE,"E79.trimOffspring");var subQ26=sQuery(id+"F3.wireOp",EDGE,"E76.trimOffspring");var subQ27=sQuery(id+"F5.wireOp",EDGE,"E98.7.10");var subQ28=sQuery(id+"F3.wireOp",EDGE,"E71.trimOffspring");var subQ29=sQuery(id+"F3.wireOp",EDGE,"E68.trimOffspring");var subQ30=sQuery(id+"F5.wireOp",EDGE,"E114.trimOffspring");var subQ31=sQuery(id+"F3.wireOp",EDGE,"E67.trimOffspring");var subQ32=sQuery(id+"F5.wireOp",EDGE,"E98.1.0");var subQ33=sQuery(id+"F5.wireOp",EDGE,"E98.7.1");var subQ34=sQuery(id+"F3.wireOp",EDGE,"E50.1.0");var subQ35=sQuery(id+"F3.wireOp",EDGE,"E66.trimOffspring");var subQ36=sQuery(id+"F7.wireOp",EDGE,"E137");var subQ37=sQuery(id+"F3.wireOp",EDGE,"E65.trimOffspring");var subQ38=sQuery(id+"F3.wireOp",EDGE,"E64.trimOffspring");var subQ39=sQuery(id+"F3.wireOp",EDGE,"E63.trimOffspring");var subQ40=sQuery(id+"F3.wireOp",EDGE,"E61.trimOffspring");var subQ41=sQuery(id+"F5.wireOp",EDGE,"E119.trimOffspring");var subQ42=sQuery(id+"F5.wireOp",EDGE,"E98.2.1");var subQ43=sQuery(id+"F3.wireOp",EDGE,"E50.5.0");var subQ44=sQuery(id+"F3.wireOp",EDGE,"E86.trimOffspring");var subQ45=sQuery(id+"F5.wireOp",EDGE,"E98.4.1");var subQ46=sQuery(id+"F3.wireOp",EDGE,"E50.2.5");var subQ47=sQuery(id+"F3.wireOp",EDGE,"E62.trimOffspring");var subQ48=sQuery(id+"F5.wireOp",EDGE,"E98.8.5");var subQ49=sQuery(id+"F3.wireOp",EDGE,"E50.4.10");var subQ50=sQuery(id+"F3.wireOp",EDGE,"E50.4.5");var subQ51=sQuery(id+"F5.wireOp",EDGE,"E98.7.5");var subQ52=sQuery(id+"F3.wireOp",EDGE,"E50.4.1");var subQ53=sQuery(id+"F3.wireOp",EDGE,"E72.trimOffspring");var subQ54=sQuery(id+"F3.wireOp",EDGE,"E50.6.10");var subQ55=sQuery(id+"F5.wireOp",EDGE,"E133.trimOffspring");var subQ56=sQuery(id+"F3.wireOp",EDGE,"E50.8.5");var subQ57=sQuery(id+"F3.wireOp",EDGE,"E50.4.0");var subQ58=sQuery(id+"F5.wireOp",EDGE,"E98.1.10");var subQ59=sQuery(id+"F3.wireOp",EDGE,"E70.trimOffspring");var subQ60=sQuery(id+"F5.wireOp",EDGE,"E101.trimOffspring");var subQ61=sQuery(id+"F3.wireOp",EDGE,"E50.8.1");var subQ62=sQuery(id+"F3.wireOp",EDGE,"E50.3.10");var subQ63=sQuery(id+"F3.wireOp",EDGE,"E50.8.0");var subQ64=sQuery(id+"F3.wireOp",EDGE,"E50.5.1");var subQ65=sQuery(id+"F3.wireOp",EDGE,"E73.trimOffspring");var subQ66=sQuery(id+"F3.wireOp",EDGE,"E50.7.0");var subQ67=sQuery(id+"F3.wireOp",EDGE,"E50.2.10");var subQ68=sQuery(id+"F3.wireOp",EDGE,"E75.trimOffspring");var subQ69=sQuery(id+"F3.wireOp",EDGE,"E50.1.5");var subQ70=sQuery(id+"F3.wireOp",EDGE,"E48.trimOffspring");var subQ71=sQuery(id+"F3.wireOp",EDGE,"E50.2.1");var subQ72=sQuery(id+"F3.wireOp",EDGE,"E47.trimOffspring");var subQ73=sQuery(id+"F3.wireOp",EDGE,"E50.1.10");var subQ74=sQuery(id+"F3.wireOp",EDGE,"E77.trimOffspring");var subQ75=sQuery(id+"F3.wireOp",EDGE,"E78.trimOffspring");var subQ76=sQuery(id+"F3.wireOp",EDGE,"E50.3.5");var subQ77=sQuery(id+"F3.wireOp",EDGE,"E50.2.0");var subQ78=sQuery(id+"F3.wireOp",EDGE,"E52.trimOffspring");var subQ79=sQuery(id+"F5.wireOp",EDGE,"E130.trimOffspring");var subQ80=sQuery(id+"F3.wireOp",EDGE,"E50.1.1");var subQ81=sQuery(id+"F3.wireOp",EDGE,"E50.5.5");var subQ82=sQuery(id+"F5.wireOp",EDGE,"E112.trimOffspring");var subQ83=sQuery(id+"F3.wireOp",EDGE,"E50.3.1");var subQ84=sQuery(id+"F3.wireOp",EDGE,"E50.5.10");var subQ85=sQuery(id+"F3.wireOp",EDGE,"E50.6.0");var subQ86=sQuery(id+"F3.wireOp",EDGE,"E50.7.5");var subQ87=sQuery(id+"F3.wireOp",EDGE,"E69.trimOffspring");var subQ88=sQuery(id+"F5.wireOp",EDGE,"E127.trimOffspring");var subQ89=sQuery(id+"F3.wireOp",EDGE,"E57.trimOffspring");var subQ90=sQuery(id+"F5.wireOp",EDGE,"E111.trimOffspring");var subQ91=sQuery(id+"F5.wireOp",EDGE,"E98.5.0");var subQ92=sQuery(id+"F5.wireOp",EDGE,"E126.trimOffspring");var subQ93=sQuery(id+"F3.wireOp",EDGE,"E50.6.1");var subQ94=sQuery(id+"F3.wireOp",EDGE,"E46.trimOffspring");var subQ95=sQuery(id+"F3.wireOp",EDGE,"E58.trimOffspring");var subQ96=sQuery(id+"F3.wireOp",EDGE,"E59.trimOffspring");var subQ97=sQuery(id+"F5.wireOp",EDGE,"E98.3.1");var subQ98=sQuery(id+"F3.wireOp",EDGE,"E50.6.5");var subQ99=sQuery(id+"F3.wireOp",EDGE,"E50.7.10");var subQ100=sQuery(id+"F5.wireOp",EDGE,"E122.trimOffspring");var subQ101=sQuery(id+"F3.wireOp",EDGE,"E60.trimOffspring");var subQ102=sQuery(id+"F5.wireOp",EDGE,"E106.trimOffspring");var subQ103=sQuery(id+"F3.wireOp",EDGE,"E74.trimOffspring");var subQ104=sQuery(id+"F3.wireOp",EDGE,"E50.3.0");var subQ105=sQuery(id+"F3.wireOp",EDGE,"E50.7.1");var subQ106=sQuery(id+"F3.wireOp",EDGE,"E50.8.10");var subQ107=sQuery(id+"F5.wireOp",EDGE,"E98.1.1");var subQ108=sQuery(id+"F3.wireOp",EDGE,"E51.trimOffspring");var subQ109=sQuery(id+"F3.wireOp",EDGE,"E53.trimOffspring");var subQ110=sQuery(id+"F5.wireOp",EDGE,"E104.trimOffspring");var subQ111=sQuery(id+"F5.wireOp",EDGE,"E98.2.10");var subQ112=sQuery(id+"F5.wireOp",EDGE,"E109.trimOffspring");var subQ113=sQuery(id+"F3.wireOp",EDGE,"E54.trimOffspring");var subQ114=sQuery(id+"F5.wireOp",EDGE,"E117.trimOffspring");var subQ115=sQuery(id+"F5.wireOp",EDGE,"E95.trimOffspring");var subQ116=sQuery(id+"F3.wireOp",EDGE,"E55.trimOffspring");var subQ117=sQuery(id+"F3.wireOp",EDGE,"E56.trimOffspring");var subQ118=sQuery(id+"F5.wireOp",EDGE,"E98.8.0");var subQ119=sQuery(id+"F5.wireOp",EDGE,"E99.trimOffspring");var subQ120=sQuery(id+"F5.wireOp",EDGE,"E100.trimOffspring");var subQ121=sQuery(id+"F5.wireOp",EDGE,"E103.trimOffspring");var subQ122=sQuery(id+"F5.wireOp",EDGE,"E105.trimOffspring");var subQ123=sQuery(id+"F5.wireOp",EDGE,"E107.trimOffspring");var subQ124=sQuery(id+"F5.wireOp",EDGE,"E108.trimOffspring");var subQ125=sQuery(id+"F5.wireOp",EDGE,"E113.trimOffspring");var subQ126=sQuery(id+"F5.wireOp",EDGE,"E115.trimOffspring");var subQ127=sQuery(id+"F5.wireOp",EDGE,"E116.trimOffspring");var subQ128=sQuery(id+"F5.wireOp",EDGE,"E120.trimOffspring");var subQ129=sQuery(id+"F5.wireOp",EDGE,"E121.trimOffspring");var subQ130=sQuery(id+"F5.wireOp",EDGE,"E123.trimOffspring");var subQ131=sQuery(id+"F5.wireOp",EDGE,"E124.trimOffspring");var subQ132=sQuery(id+"F5.wireOp",EDGE,"E125.trimOffspring");var subQ133=sQuery(id+"F5.wireOp",EDGE,"E128.trimOffspring");var subQ134=sQuery(id+"F5.wireOp",EDGE,"E129.trimOffspring");var subQ135=sQuery(id+"F5.wireOp",EDGE,"E131.trimOffspring");var subQ136=sQuery(id+"F5.wireOp",EDGE,"E132.trimOffspring");var subQ137=sQuery(id+"F0.wireOp",EDGE,"E15");Q0=makeQuery(id+"F10.boolean.opBoolean","SPLIT",FACE,{"disambiguationData":[TD([makeQuery(id+"F4.opExtrude","SWEPT_FACE",FACE,{"disambiguationData":[OSD([subQ18])]})])],"derivedFrom":makeQuery(id+"F8.boolean.opBoolean","MERGE",FACE,{"derivedFrom":[makeQuery(id+"F6.boolean.opBoolean","MERGE",FACE,{"derivedFrom":[makeQuery(id+"F4.boolean.opBoolean","MERGE",FACE,{"derivedFrom":[makeQuery(id+"F2.opChamfer","SPLIT",FACE,{"disambiguationData":[OD(18.0)],"derivedFrom":makeQuery(id+"F1.opExtrude","CAP_FACE",FACE,{"disambiguationData":[OSD([sQuery(id+"F0.wireOp",EDGE,"E12.1.0"),sQuery(id+"F0.wireOp",EDGE,"E12.1.1"),sQuery(id+"F0.wireOp",EDGE,"E12.1.2"),sQuery(id+"F0.wireOp",EDGE,"E12.1.3"),sQuery(id+"F0.wireOp",EDGE,"E12.1.4"),sQuery(id+"F0.wireOp",EDGE,"E12.1.5"),sQuery(id+"F0.wireOp",EDGE,"E12.1.6"),sQuery(id+"F0.wireOp",EDGE,"E12.1.7"),sQuery(id+"F0.wireOp",EDGE,"E12.1.10"),sQuery(id+"F0.wireOp",EDGE,"E12.1.11"),sQuery(id+"F0.wireOp",EDGE,"E12.2.0"),sQuery(id+"F0.wireOp",EDGE,"E12.2.1"),sQuery(id+"F0.wireOp",EDGE,"E12.2.2"),sQuery(id+"F0.wireOp",EDGE,"E12.2.3"),sQuery(id+"F0.wireOp",EDGE,"E12.2.4"),sQuery(id+"F0.wireOp",EDGE,"E12.2.5"),sQuery(id+"F0.wireOp",EDGE,"E12.2.6"),sQuery(id+"F0.wireOp",EDGE,"E12.2.7"),sQuery(id+"F0.wireOp",EDGE,"E12.2.10"),sQuery(id+"F0.wireOp",EDGE,"E12.2.11"),sQuery(id+"F0.wireOp",EDGE,"E12.3.0"),sQuery(id+"F0.wireOp",EDGE,"E12.3.1"),sQuery(id+"F0.wireOp",EDGE,"E12.3.2"),sQuery(id+"F0.wireOp",EDGE,"E12.3.3"),sQuery(id+"F0.wireOp",EDGE,"E12.3.4"),sQuery(id+"F0.wireOp",EDGE,"E12.3.5"),sQuery(id+"F0.wireOp",EDGE,"E12.3.6"),sQuery(id+"F0.wireOp",EDGE,"E12.3.7"),sQuery(id+"F0.wireOp",EDGE,"E12.3.10"),sQuery(id+"F0.wireOp",EDGE,"E12.3.11"),sQuery(id+"F0.wireOp",EDGE,"E12.4.0"),sQuery(id+"F0.wireOp",EDGE,"E12.4.1"),sQuery(id+"F0.wireOp",EDGE,"E12.4.2"),sQuery(id+"F0.wireOp",EDGE,"E12.4.3"),sQuery(id+"F0.wireOp",EDGE,"E12.4.4"),sQuery(id+"F0.wireOp",EDGE,"E12.4.5"),sQuery(id+"F0.wireOp",EDGE,"E12.4.6"),sQuery(id+"F0.wireOp",EDGE,"E12.4.7"),sQuery(id+"F0.wireOp",EDGE,"E12.4.10"),sQuery(id+"F0.wireOp",EDGE,"E12.4.11"),sQuery(id+"F0.wireOp",EDGE,"E12.5.0"),sQuery(id+"F0.wireOp",EDGE,"E12.5.1"),sQuery(id+"F0.wireOp",EDGE,"E12.5.2"),sQuery(id+"F0.wireOp",EDGE,"E12.5.3"),sQuery(id+"F0.wireOp",EDGE,"E12.5.4"),sQuery(id+"F0.wireOp",EDGE,"E12.5.5"),sQuery(id+"F0.wireOp",EDGE,"E12.5.6"),sQuery(id+"F0.wireOp",EDGE,"E12.5.7"),sQuery(id+"F0.wireOp",EDGE,"E12.5.10"),sQuery(id+"F0.wireOp",EDGE,"E12.5.11"),sQuery(id+"F0.wireOp",EDGE,"E12.6.0"),sQuery(id+"F0.wireOp",EDGE,"E12.6.1"),sQuery(id+"F0.wireOp",EDGE,"E12.6.2"),sQuery(id+"F0.wireOp",EDGE,"E12.6.3"),sQuery(id+"F0.wireOp",EDGE,"E12.6.4"),sQuery(id+"F0.wireOp",EDGE,"E12.6.5"),sQuery(id+"F0.wireOp",EDGE,"E12.6.6"),sQuery(id+"F0.wireOp",EDGE,"E12.6.7"),sQuery(id+"F0.wireOp",EDGE,"E12.6.10"),sQuery(id+"F0.wireOp",EDGE,"E12.6.11"),sQuery(id+"F0.wireOp",EDGE,"E12.7.0"),sQuery(id+"F0.wireOp",EDGE,"E12.7.1"),sQuery(id+"F0.wireOp",EDGE,"E12.7.2"),sQuery(id+"F0.wireOp",EDGE,"E12.7.3"),sQuery(id+"F0.wireOp",EDGE,"E12.7.4"),sQuery(id+"F0.wireOp",EDGE,"E12.7.5"),sQuery(id+"F0.wireOp",EDGE,"E12.7.6"),sQuery(id+"F0.wireOp",EDGE,"E12.7.7"),sQuery(id+"F0.wireOp",EDGE,"E12.7.10"),sQuery(id+"F0.wireOp",EDGE,"E12.7.11"),sQuery(id+"F0.wireOp",EDGE,"E12.8.0"),sQuery(id+"F0.wireOp",EDGE,"E12.8.1"),sQuery(id+"F0.wireOp",EDGE,"E12.8.2"),sQuery(id+"F0.wireOp",EDGE,"E12.8.3"),sQuery(id+"F0.wireOp",EDGE,"E12.8.4"),sQuery(id+"F0.wireOp",EDGE,"E12.8.5"),sQuery(id+"F0.wireOp",EDGE,"E12.8.6"),sQuery(id+"F0.wireOp",EDGE,"E12.8.7"),sQuery(id+"F0.wireOp",EDGE,"E12.8.10"),sQuery(id+"F0.wireOp",EDGE,"E12.8.11"),sQuery(id+"F0.wireOp",EDGE,"E12.9.0"),sQuery(id+"F0.wireOp",EDGE,"E12.9.1"),sQuery(id+"F0.wireOp",EDGE,"E12.9.2"),sQuery(id+"F0.wireOp",EDGE,"E12.9.3"),sQuery(id+"F0.wireOp",EDGE,"E12.9.4"),sQuery(id+"F0.wireOp",EDGE,"E12.9.5"),sQuery(id+"F0.wireOp",EDGE,"E12.9.6"),sQuery(id+"F0.wireOp",EDGE,"E12.9.7"),sQuery(id+"F0.wireOp",EDGE,"E12.9.10"),sQuery(id+"F0.wireOp",EDGE,"E12.9.11"),sQuery(id+"F0.wireOp",EDGE,"E13.1.0"),sQuery(id+"F0.wireOp",EDGE,"E13.1.1"),sQuery(id+"F0.wireOp",EDGE,"E13.1.2"),sQuery(id+"F0.wireOp",EDGE,"E13.1.5"),sQuery(id+"F0.wireOp",EDGE,"E13.1.6"),sQuery(id+"F0.wireOp",EDGE,"E13.1.7"),sQuery(id+"F0.wireOp",EDGE,"E13.1.8"),sQuery(id+"F0.wireOp",EDGE,"E13.1.9"),sQuery(id+"F0.wireOp",EDGE,"E13.1.10"),sQuery(id+"F0.wireOp",EDGE,"E13.1.11"),sQuery(id+"F0.wireOp",EDGE,"E13.2.0"),sQuery(id+"F0.wireOp",EDGE,"E13.2.1"),sQuery(id+"F0.wireOp",EDGE,"E13.2.2"),sQuery(id+"F0.wireOp",EDGE,"E13.2.5"),sQuery(id+"F0.wireOp",EDGE,"E13.2.6"),sQuery(id+"F0.wireOp",EDGE,"E13.2.7"),sQuery(id+"F0.wireOp",EDGE,"E13.2.8"),sQuery(id+"F0.wireOp",EDGE,"E13.2.9"),sQuery(id+"F0.wireOp",EDGE,"E13.2.10"),sQuery(id+"F0.wireOp",EDGE,"E13.2.11"),sQuery(id+"F0.wireOp",EDGE,"E13.3.0"),sQuery(id+"F0.wireOp",EDGE,"E13.3.1"),sQuery(id+"F0.wireOp",EDGE,"E13.3.2"),sQuery(id+"F0.wireOp",EDGE,"E13.3.5"),sQuery(id+"F0.wireOp",EDGE,"E13.3.6"),sQuery(id+"F0.wireOp",EDGE,"E13.3.7"),sQuery(id+"F0.wireOp",EDGE,"E13.3.8"),sQuery(id+"F0.wireOp",EDGE,"E13.3.9"),sQuery(id+"F0.wireOp",EDGE,"E13.3.10"),sQuery(id+"F0.wireOp",EDGE,"E13.3.11"),sQuery(id+"F0.wireOp",EDGE,"E13.4.0"),sQuery(id+"F0.wireOp",EDGE,"E13.4.1"),sQuery(id+"F0.wireOp",EDGE,"E13.4.2"),sQuery(id+"F0.wireOp",EDGE,"E13.4.5"),sQuery(id+"F0.wireOp",EDGE,"E13.4.6"),sQuery(id+"F0.wireOp",EDGE,"E13.4.7"),sQuery(id+"F0.wireOp",EDGE,"E13.4.8"),sQuery(id+"F0.wireOp",EDGE,"E13.4.9"),sQuery(id+"F0.wireOp",EDGE,"E13.4.10"),sQuery(id+"F0.wireOp",EDGE,"E13.4.11"),sQuery(id+"F0.wireOp",EDGE,"E13.5.0"),sQuery(id+"F0.wireOp",EDGE,"E13.5.1"),sQuery(id+"F0.wireOp",EDGE,"E13.5.2"),sQuery(id+"F0.wireOp",EDGE,"E13.5.5"),sQuery(id+"F0.wireOp",EDGE,"E13.5.6"),sQuery(id+"F0.wireOp",EDGE,"E13.5.7"),sQuery(id+"F0.wireOp",EDGE,"E13.5.8"),sQuery(id+"F0.wireOp",EDGE,"E13.5.9"),sQuery(id+"F0.wireOp",EDGE,"E13.5.10"),sQuery(id+"F0.wireOp",EDGE,"E13.5.11"),sQuery(id+"F0.wireOp",EDGE,"E13.6.0"),sQuery(id+"F0.wireOp",EDGE,"E13.6.1"),sQuery(id+"F0.wireOp",EDGE,"E13.6.2"),sQuery(id+"F0.wireOp",EDGE,"E13.6.5"),sQuery(id+"F0.wireOp",EDGE,"E13.6.6"),sQuery(id+"F0.wireOp",EDGE,"E13.6.7"),sQuery(id+"F0.wireOp",EDGE,"E13.6.8"),sQuery(id+"F0.wireOp",EDGE,"E13.6.9"),sQuery(id+"F0.wireOp",EDGE,"E13.6.10"),sQuery(id+"F0.wireOp",EDGE,"E13.6.11"),sQuery(id+"F0.wireOp",EDGE,"E13.7.0"),sQuery(id+"F0.wireOp",EDGE,"E13.7.1"),sQuery(id+"F0.wireOp",EDGE,"E13.7.2"),sQuery(id+"F0.wireOp",EDGE,"E13.7.5"),sQuery(id+"F0.wireOp",EDGE,"E13.7.6"),sQuery(id+"F0.wireOp",EDGE,"E13.7.7"),sQuery(id+"F0.wireOp",EDGE,"E13.7.8"),sQuery(id+"F0.wireOp",EDGE,"E13.7.9"),sQuery(id+"F0.wireOp",EDGE,"E13.7.10"),sQuery(id+"F0.wireOp",EDGE,"E13.7.11"),sQuery(id+"F0.wireOp",EDGE,"E13.8.0"),sQuery(id+"F0.wireOp",EDGE,"E13.8.1"),sQuery(id+"F0.wireOp",EDGE,"E13.8.2"),sQuery(id+"F0.wireOp",EDGE,"E13.8.5"),sQuery(id+"F0.wireOp",EDGE,"E13.8.6"),sQuery(id+"F0.wireOp",EDGE,"E13.8.7"),sQuery(id+"F0.wireOp",EDGE,"E13.8.8"),sQuery(id+"F0.wireOp",EDGE,"E13.8.9"),sQuery(id+"F0.wireOp",EDGE,"E13.8.10"),sQuery(id+"F0.wireOp",EDGE,"E13.8.11"),sQuery(id+"F0.wireOp",EDGE,"E3"),sQuery(id+"F0.wireOp",EDGE,"E2"),sQuery(id+"F0.wireOp",EDGE,"E1"),sQuery(id+"F0.wireOp",EDGE,"E4"),sQuery(id+"F0.wireOp",EDGE,"E8"),sQuery(id+"F0.wireOp",EDGE,"E5"),sQuery(id+"F0.wireOp",EDGE,"E11"),sQuery(id+"F0.wireOp",EDGE,"E6"),sQuery(id+"F0.wireOp",EDGE,"E7"),sQuery(id+"F0.wireOp",EDGE,"E10"),sQuery(id+"F0.wireOp",EDGE,"E14"),subQ137,sQuery(id+"F0.wireOp",EDGE,"E20.trimOffspring"),sQuery(id+"F0.wireOp",EDGE,"E21.trimOffspring"),sQuery(id+"F0.wireOp",EDGE,"E22.trimOffspring"),sQuery(id+"F0.wireOp",EDGE,"E23.trimOffspring"),sQuery(id+"F0.wireOp",EDGE,"E24.trimOffspring"),sQuery(id+"F0.wireOp",EDGE,"E25.trimOffspring"),sQuery(id+"F0.wireOp",EDGE,"E26.trimOffspring"),sQuery(id+"F0.wireOp",EDGE,"E27.trimOffspring"),sQuery(id+"F0.wireOp",EDGE,"E28.trimOffspring"),sQuery(id+"F0.wireOp",EDGE,"E29.trimOffspring"),sQuery(id+"F0.wireOp",EDGE,"E30.trimOffspring"),sQuery(id+"F0.wireOp",EDGE,"E31.trimOffspring"),sQuery(id+"F0.wireOp",EDGE,"E32.trimOffspring"),sQuery(id+"F0.wireOp",EDGE,"E33.trimOffspring"),sQuery(id+"F0.wireOp",EDGE,"E34.trimOffspring"),sQuery(id+"F0.wireOp",EDGE,"E35.trimOffspring"),sQuery(id+"F0.wireOp",EDGE,"E36.trimOffspring"),sQuery(id+"F0.wireOp",EDGE,"E37")])],"isStart":false})}),makeQuery(id+"F4.opExtrude","CAP_FACE",FACE,{"disambiguationData":[OSD([subQ137,subQ18,sQuery(id+"F3.wireOp",EDGE,"E43.0"),subQ94,subQ72,subQ70,sQuery(id+"F3.wireOp",EDGE,"E49.trimOffspring"),subQ34,subQ80,subQ69,sQuery(id+"F3.wireOp",EDGE,"E50.1.6"),sQuery(id+"F3.wireOp",EDGE,"E50.1.8"),subQ73,subQ77,subQ71,subQ46,sQuery(id+"F3.wireOp",EDGE,"E50.2.6"),sQuery(id+"F3.wireOp",EDGE,"E50.2.8"),subQ67,subQ104,subQ83,subQ76,sQuery(id+"F3.wireOp",EDGE,"E50.3.6"),sQuery(id+"F3.wireOp",EDGE,"E50.3.8"),subQ62,subQ57,subQ52,subQ50,sQuery(id+"F3.wireOp",EDGE,"E50.4.6"),sQuery(id+"F3.wireOp",EDGE,"E50.4.8"),subQ49,subQ43,subQ64,subQ81,sQuery(id+"F3.wireOp",EDGE,"E50.5.6"),sQuery(id+"F3.wireOp",EDGE,"E50.5.8"),subQ84,subQ85,subQ93,subQ98,sQuery(id+"F3.wireOp",EDGE,"E50.6.6"),sQuery(id+"F3.wireOp",EDGE,"E50.6.8"),subQ54,subQ66,subQ105,subQ86,sQuery(id+"F3.wireOp",EDGE,"E50.7.6"),sQuery(id+"F3.wireOp",EDGE,"E50.7.8"),subQ99,subQ63,subQ61,subQ56,sQuery(id+"F3.wireOp",EDGE,"E50.8.6"),sQuery(id+"F3.wireOp",EDGE,"E50.8.8"),subQ106,subQ108,subQ78,subQ109,subQ113,subQ116,subQ117,subQ89,subQ95,subQ96,subQ101,subQ40,subQ47,subQ39,subQ38,subQ37,subQ35,subQ31,subQ29,subQ87,subQ59,subQ28,subQ53,subQ65,subQ103,subQ68,subQ26,subQ74,subQ75,subQ25,subQ8,subQ24,subQ23,subQ22,subQ20,subQ19,subQ44])],"isStart":false})]}),makeQuery(id+"F6.opExtrude","CAP_FACE",FACE,{"disambiguationData":[OSD([sQuery(id+"F5.wireOp",EDGE,"E88"),sQuery(id+"F5.wireOp",EDGE,"E89"),subQ16,sQuery(id+"F5.wireOp",EDGE,"E91.0"),sQuery(id+"F5.wireOp",EDGE,"E92"),sQuery(id+"F5.wireOp",EDGE,"E93"),subQ15,subQ115,subQ13,sQuery(id+"F5.wireOp",EDGE,"E97.trimOffspring"),subQ32,subQ107,subQ10,sQuery(id+"F5.wireOp",EDGE,"E98.1.6"),sQuery(id+"F5.wireOp",EDGE,"E98.1.7"),sQuery(id+"F5.wireOp",EDGE,"E98.1.8"),sQuery(id+"F5.wireOp",EDGE,"E98.1.9"),subQ58,subQ7,subQ42,subQ6,sQuery(id+"F5.wireOp",EDGE,"E98.2.6"),sQuery(id+"F5.wireOp",EDGE,"E98.2.7"),sQuery(id+"F5.wireOp",EDGE,"E98.2.8"),sQuery(id+"F5.wireOp",EDGE,"E98.2.9"),subQ111,subQ4,subQ97,sQuery(id+"F5.wireOp",EDGE,"E98.3.5"),sQuery(id+"F5.wireOp",EDGE,"E98.3.6"),sQuery(id+"F5.wireOp",EDGE,"E98.3.7"),sQuery(id+"F5.wireOp",EDGE,"E98.3.8"),sQuery(id+"F5.wireOp",EDGE,"E98.3.9"),sQuery(id+"F5.wireOp",EDGE,"E98.3.10"),subQ11,subQ45,sQuery(id+"F5.wireOp",EDGE,"E98.4.5"),sQuery(id+"F5.wireOp",EDGE,"E98.4.6"),sQuery(id+"F5.wireOp",EDGE,"E98.4.7"),sQuery(id+"F5.wireOp",EDGE,"E98.4.8"),sQuery(id+"F5.wireOp",EDGE,"E98.4.9"),sQuery(id+"F5.wireOp",EDGE,"E98.4.10"),subQ91,subQ3,sQuery(id+"F5.wireOp",EDGE,"E98.5.5"),sQuery(id+"F5.wireOp",EDGE,"E98.5.6"),sQuery(id+"F5.wireOp",EDGE,"E98.5.7"),sQuery(id+"F5.wireOp",EDGE,"E98.5.8"),sQuery(id+"F5.wireOp",EDGE,"E98.5.9"),sQuery(id+"F5.wireOp",EDGE,"E98.5.10"),subQ1,subQ17,sQuery(id+"F5.wireOp",EDGE,"E98.6.5"),sQuery(id+"F5.wireOp",EDGE,"E98.6.6"),sQuery(id+"F5.wireOp",EDGE,"E98.6.7"),sQuery(id+"F5.wireOp",EDGE,"E98.6.8"),sQuery(id+"F5.wireOp",EDGE,"E98.6.9"),sQuery(id+"F5.wireOp",EDGE,"E98.6.10"),subQ0,subQ33,subQ51,sQuery(id+"F5.wireOp",EDGE,"E98.7.6"),sQuery(id+"F5.wireOp",EDGE,"E98.7.7"),sQuery(id+"F5.wireOp",EDGE,"E98.7.8"),sQuery(id+"F5.wireOp",EDGE,"E98.7.9"),subQ27,subQ118,subQ14,subQ48,sQuery(id+"F5.wireOp",EDGE,"E98.8.6"),sQuery(id+"F5.wireOp",EDGE,"E98.8.7"),sQuery(id+"F5.wireOp",EDGE,"E98.8.8"),sQuery(id+"F5.wireOp",EDGE,"E98.8.9"),subQ21,subQ119,subQ120,subQ60,subQ9,subQ121,subQ110,subQ122,subQ102,subQ123,subQ124,subQ112,subQ5,subQ90,subQ82,subQ125,subQ30,subQ126,subQ127,subQ114,subQ12,subQ41,subQ128,subQ129,subQ100,subQ130,subQ131,subQ132,subQ92,subQ88,subQ133,subQ134,subQ79,subQ135,subQ136,subQ55,subQ2])],"isStart":true})]}),makeQuery(id+"F8.opExtrude","CAP_FACE",FACE,{"disambiguationData":[OSD([sQuery(id+"F7.wireOp",EDGE,"E135"),subQ36])],"isStart":true})]})});}
            var sketch = newSketch(context, id + "F11", { "sketchPlane" : qUnion([Q0])});
            skLineSegment(sketch, "E140", {"start": v(0, 0) * mm, "end": v(0, 51.6) * mm});
            skLineSegment(sketch, "E141", {"start": v(0, 51.6) * mm, "end": v(0, 55.33) * mm});
            skLineSegment(sketch, "E142", {"start": v(0, 55.33) * mm, "end": v(-2.86, 51.52) * mm});
            skLineSegment(sketch, "E143.MirrorCS", {"start": v(0, 55.33) * mm, "end": v(2.86, 51.52) * mm});
            skLineSegment(sketch, "E144", {"start": v(-2.86, 51.52) * mm, "end": v(0, 50.05) * mm});
            skLineSegment(sketch, "E145", {"start": v(0, 50.05) * mm, "end": v(2.86, 51.52) * mm});
            skLineSegment(sketch, "E146.1.0", {"start": v(-39.12, 39.12) * mm, "end": v(-34.4, 38.45) * mm});
            skLineSegment(sketch, "E146.1.1", {"start": v(-39.12, 39.12) * mm, "end": v(-38.45, 34.4) * mm});
            skLineSegment(sketch, "E146.1.2", {"start": v(-38.45, 34.4) * mm, "end": v(-35.39, 35.39) * mm});
            skLineSegment(sketch, "E146.1.3", {"start": v(-35.39, 35.39) * mm, "end": v(-34.4, 38.45) * mm});
            skLineSegment(sketch, "E146.2.0", {"start": v(-55.33, 0) * mm, "end": v(-51.52, 2.86) * mm});
            skLineSegment(sketch, "E146.2.1", {"start": v(-55.33, 0) * mm, "end": v(-51.52, -2.86) * mm});
            skLineSegment(sketch, "E146.2.2", {"start": v(-51.52, -2.86) * mm, "end": v(-50.05, 0) * mm});
            skLineSegment(sketch, "E146.2.3", {"start": v(-50.05, 0) * mm, "end": v(-51.52, 2.86) * mm});
            skLineSegment(sketch, "E146.3.0", {"start": v(-39.12, -39.12) * mm, "end": v(-38.45, -34.4) * mm});
            skLineSegment(sketch, "E146.3.1", {"start": v(-39.12, -39.12) * mm, "end": v(-34.4, -38.45) * mm});
            skLineSegment(sketch, "E146.3.2", {"start": v(-34.4, -38.45) * mm, "end": v(-35.39, -35.39) * mm});
            skLineSegment(sketch, "E146.3.3", {"start": v(-35.39, -35.39) * mm, "end": v(-38.45, -34.4) * mm});
            skLineSegment(sketch, "E146.4.0", {"start": v(0, -55.33) * mm, "end": v(-2.86, -51.52) * mm});
            skLineSegment(sketch, "E146.4.1", {"start": v(0, -55.33) * mm, "end": v(2.86, -51.52) * mm});
            skLineSegment(sketch, "E146.4.2", {"start": v(2.86, -51.52) * mm, "end": v(0, -50.05) * mm});
            skLineSegment(sketch, "E146.4.3", {"start": v(0, -50.05) * mm, "end": v(-2.86, -51.52) * mm});
            skLineSegment(sketch, "E146.5.0", {"start": v(39.12, -39.12) * mm, "end": v(34.4, -38.45) * mm});
            skLineSegment(sketch, "E146.5.1", {"start": v(39.12, -39.12) * mm, "end": v(38.45, -34.4) * mm});
            skLineSegment(sketch, "E146.5.2", {"start": v(38.45, -34.4) * mm, "end": v(35.39, -35.39) * mm});
            skLineSegment(sketch, "E146.5.3", {"start": v(35.39, -35.39) * mm, "end": v(34.4, -38.45) * mm});
            skLineSegment(sketch, "E146.6.0", {"start": v(55.33, 0) * mm, "end": v(51.52, -2.86) * mm});
            skLineSegment(sketch, "E146.6.1", {"start": v(55.33, 0) * mm, "end": v(51.52, 2.86) * mm});
            skLineSegment(sketch, "E146.6.2", {"start": v(51.52, 2.86) * mm, "end": v(50.05, 0) * mm});
            skLineSegment(sketch, "E146.6.3", {"start": v(50.05, 0) * mm, "end": v(51.52, -2.86) * mm});
            skLineSegment(sketch, "E146.7.0", {"start": v(39.12, 39.12) * mm, "end": v(38.45, 34.4) * mm});
            skLineSegment(sketch, "E146.7.1", {"start": v(39.12, 39.12) * mm, "end": v(34.4, 38.45) * mm});
            skLineSegment(sketch, "E146.7.2", {"start": v(34.4, 38.45) * mm, "end": v(35.39, 35.39) * mm});
            skLineSegment(sketch, "E146.7.3", {"start": v(35.39, 35.39) * mm, "end": v(38.45, 34.4) * mm});
            skPoint(sketch, "E146.center", {"position": v(0, 0) * mm});
            skSolve(sketch);
        }
        {
            var Q0;
            Q0=qSketchRegion(id+"F11",true);
            extrude(context, id + "F12", {"entities" : qUnion([Q0]), "oppositeDirection" : true, "depth" : 5.08 * mm});
        }
        {
            var Q0;
            Q0=makeQuery(id+"F10.boolean.opBoolean","SPLIT",BODY,{"disambiguationData":[OD(0.0)],"derivedFrom":makeQuery(id+"F1.opExtrude","SWEPT_BODY",BODY,{"disambiguationData":[OSD([sQuery(id+"F0.wireOp",EDGE,"E12.1.0"),sQuery(id+"F0.wireOp",EDGE,"E12.1.1"),sQuery(id+"F0.wireOp",EDGE,"E12.1.2"),sQuery(id+"F0.wireOp",EDGE,"E12.1.3"),sQuery(id+"F0.wireOp",EDGE,"E12.1.4"),sQuery(id+"F0.wireOp",EDGE,"E12.1.5"),sQuery(id+"F0.wireOp",EDGE,"E12.1.6"),sQuery(id+"F0.wireOp",EDGE,"E12.1.7"),sQuery(id+"F0.wireOp",EDGE,"E12.1.10"),sQuery(id+"F0.wireOp",EDGE,"E12.1.11"),sQuery(id+"F0.wireOp",EDGE,"E12.2.0"),sQuery(id+"F0.wireOp",EDGE,"E12.2.1"),sQuery(id+"F0.wireOp",EDGE,"E12.2.2"),sQuery(id+"F0.wireOp",EDGE,"E12.2.3"),sQuery(id+"F0.wireOp",EDGE,"E12.2.4"),sQuery(id+"F0.wireOp",EDGE,"E12.2.5"),sQuery(id+"F0.wireOp",EDGE,"E12.2.6"),sQuery(id+"F0.wireOp",EDGE,"E12.2.7"),sQuery(id+"F0.wireOp",EDGE,"E12.2.10"),sQuery(id+"F0.wireOp",EDGE,"E12.2.11"),sQuery(id+"F0.wireOp",EDGE,"E12.3.0"),sQuery(id+"F0.wireOp",EDGE,"E12.3.1"),sQuery(id+"F0.wireOp",EDGE,"E12.3.2"),sQuery(id+"F0.wireOp",EDGE,"E12.3.3"),sQuery(id+"F0.wireOp",EDGE,"E12.3.4"),sQuery(id+"F0.wireOp",EDGE,"E12.3.5"),sQuery(id+"F0.wireOp",EDGE,"E12.3.6"),sQuery(id+"F0.wireOp",EDGE,"E12.3.7"),sQuery(id+"F0.wireOp",EDGE,"E12.3.10"),sQuery(id+"F0.wireOp",EDGE,"E12.3.11"),sQuery(id+"F0.wireOp",EDGE,"E12.4.0"),sQuery(id+"F0.wireOp",EDGE,"E12.4.1"),sQuery(id+"F0.wireOp",EDGE,"E12.4.2"),sQuery(id+"F0.wireOp",EDGE,"E12.4.3"),sQuery(id+"F0.wireOp",EDGE,"E12.4.4"),sQuery(id+"F0.wireOp",EDGE,"E12.4.5"),sQuery(id+"F0.wireOp",EDGE,"E12.4.6"),sQuery(id+"F0.wireOp",EDGE,"E12.4.7"),sQuery(id+"F0.wireOp",EDGE,"E12.4.10"),sQuery(id+"F0.wireOp",EDGE,"E12.4.11"),sQuery(id+"F0.wireOp",EDGE,"E12.5.0"),sQuery(id+"F0.wireOp",EDGE,"E12.5.1"),sQuery(id+"F0.wireOp",EDGE,"E12.5.2"),sQuery(id+"F0.wireOp",EDGE,"E12.5.3"),sQuery(id+"F0.wireOp",EDGE,"E12.5.4"),sQuery(id+"F0.wireOp",EDGE,"E12.5.5"),sQuery(id+"F0.wireOp",EDGE,"E12.5.6"),sQuery(id+"F0.wireOp",EDGE,"E12.5.7"),sQuery(id+"F0.wireOp",EDGE,"E12.5.10"),sQuery(id+"F0.wireOp",EDGE,"E12.5.11"),sQuery(id+"F0.wireOp",EDGE,"E12.6.0"),sQuery(id+"F0.wireOp",EDGE,"E12.6.1"),sQuery(id+"F0.wireOp",EDGE,"E12.6.2"),sQuery(id+"F0.wireOp",EDGE,"E12.6.3"),sQuery(id+"F0.wireOp",EDGE,"E12.6.4"),sQuery(id+"F0.wireOp",EDGE,"E12.6.5"),sQuery(id+"F0.wireOp",EDGE,"E12.6.6"),sQuery(id+"F0.wireOp",EDGE,"E12.6.7"),sQuery(id+"F0.wireOp",EDGE,"E12.6.10"),sQuery(id+"F0.wireOp",EDGE,"E12.6.11"),sQuery(id+"F0.wireOp",EDGE,"E12.7.0"),sQuery(id+"F0.wireOp",EDGE,"E12.7.1"),sQuery(id+"F0.wireOp",EDGE,"E12.7.2"),sQuery(id+"F0.wireOp",EDGE,"E12.7.3"),sQuery(id+"F0.wireOp",EDGE,"E12.7.4"),sQuery(id+"F0.wireOp",EDGE,"E12.7.5"),sQuery(id+"F0.wireOp",EDGE,"E12.7.6"),sQuery(id+"F0.wireOp",EDGE,"E12.7.7"),sQuery(id+"F0.wireOp",EDGE,"E12.7.10"),sQuery(id+"F0.wireOp",EDGE,"E12.7.11"),sQuery(id+"F0.wireOp",EDGE,"E12.8.0"),sQuery(id+"F0.wireOp",EDGE,"E12.8.1"),sQuery(id+"F0.wireOp",EDGE,"E12.8.2"),sQuery(id+"F0.wireOp",EDGE,"E12.8.3"),sQuery(id+"F0.wireOp",EDGE,"E12.8.4"),sQuery(id+"F0.wireOp",EDGE,"E12.8.5"),sQuery(id+"F0.wireOp",EDGE,"E12.8.6"),sQuery(id+"F0.wireOp",EDGE,"E12.8.7"),sQuery(id+"F0.wireOp",EDGE,"E12.8.10"),sQuery(id+"F0.wireOp",EDGE,"E12.8.11"),sQuery(id+"F0.wireOp",EDGE,"E12.9.0"),sQuery(id+"F0.wireOp",EDGE,"E12.9.1"),sQuery(id+"F0.wireOp",EDGE,"E12.9.2"),sQuery(id+"F0.wireOp",EDGE,"E12.9.3"),sQuery(id+"F0.wireOp",EDGE,"E12.9.4"),sQuery(id+"F0.wireOp",EDGE,"E12.9.5"),sQuery(id+"F0.wireOp",EDGE,"E12.9.6"),sQuery(id+"F0.wireOp",EDGE,"E12.9.7"),sQuery(id+"F0.wireOp",EDGE,"E12.9.10"),sQuery(id+"F0.wireOp",EDGE,"E12.9.11"),sQuery(id+"F0.wireOp",EDGE,"E13.1.0"),sQuery(id+"F0.wireOp",EDGE,"E13.1.1"),sQuery(id+"F0.wireOp",EDGE,"E13.1.2"),sQuery(id+"F0.wireOp",EDGE,"E13.1.5"),sQuery(id+"F0.wireOp",EDGE,"E13.1.6"),sQuery(id+"F0.wireOp",EDGE,"E13.1.7"),sQuery(id+"F0.wireOp",EDGE,"E13.1.8"),sQuery(id+"F0.wireOp",EDGE,"E13.1.9"),sQuery(id+"F0.wireOp",EDGE,"E13.1.10"),sQuery(id+"F0.wireOp",EDGE,"E13.1.11"),sQuery(id+"F0.wireOp",EDGE,"E13.2.0"),sQuery(id+"F0.wireOp",EDGE,"E13.2.1"),sQuery(id+"F0.wireOp",EDGE,"E13.2.2"),sQuery(id+"F0.wireOp",EDGE,"E13.2.5"),sQuery(id+"F0.wireOp",EDGE,"E13.2.6"),sQuery(id+"F0.wireOp",EDGE,"E13.2.7"),sQuery(id+"F0.wireOp",EDGE,"E13.2.8"),sQuery(id+"F0.wireOp",EDGE,"E13.2.9"),sQuery(id+"F0.wireOp",EDGE,"E13.2.10"),sQuery(id+"F0.wireOp",EDGE,"E13.2.11"),sQuery(id+"F0.wireOp",EDGE,"E13.3.0"),sQuery(id+"F0.wireOp",EDGE,"E13.3.1"),sQuery(id+"F0.wireOp",EDGE,"E13.3.2"),sQuery(id+"F0.wireOp",EDGE,"E13.3.5"),sQuery(id+"F0.wireOp",EDGE,"E13.3.6"),sQuery(id+"F0.wireOp",EDGE,"E13.3.7"),sQuery(id+"F0.wireOp",EDGE,"E13.3.8"),sQuery(id+"F0.wireOp",EDGE,"E13.3.9"),sQuery(id+"F0.wireOp",EDGE,"E13.3.10"),sQuery(id+"F0.wireOp",EDGE,"E13.3.11"),sQuery(id+"F0.wireOp",EDGE,"E13.4.0"),sQuery(id+"F0.wireOp",EDGE,"E13.4.1"),sQuery(id+"F0.wireOp",EDGE,"E13.4.2"),sQuery(id+"F0.wireOp",EDGE,"E13.4.5"),sQuery(id+"F0.wireOp",EDGE,"E13.4.6"),sQuery(id+"F0.wireOp",EDGE,"E13.4.7"),sQuery(id+"F0.wireOp",EDGE,"E13.4.8"),sQuery(id+"F0.wireOp",EDGE,"E13.4.9"),sQuery(id+"F0.wireOp",EDGE,"E13.4.10"),sQuery(id+"F0.wireOp",EDGE,"E13.4.11"),sQuery(id+"F0.wireOp",EDGE,"E13.5.0"),sQuery(id+"F0.wireOp",EDGE,"E13.5.1"),sQuery(id+"F0.wireOp",EDGE,"E13.5.2"),sQuery(id+"F0.wireOp",EDGE,"E13.5.5"),sQuery(id+"F0.wireOp",EDGE,"E13.5.6"),sQuery(id+"F0.wireOp",EDGE,"E13.5.7"),sQuery(id+"F0.wireOp",EDGE,"E13.5.8"),sQuery(id+"F0.wireOp",EDGE,"E13.5.9"),sQuery(id+"F0.wireOp",EDGE,"E13.5.10"),sQuery(id+"F0.wireOp",EDGE,"E13.5.11"),sQuery(id+"F0.wireOp",EDGE,"E13.6.0"),sQuery(id+"F0.wireOp",EDGE,"E13.6.1"),sQuery(id+"F0.wireOp",EDGE,"E13.6.2"),sQuery(id+"F0.wireOp",EDGE,"E13.6.5"),sQuery(id+"F0.wireOp",EDGE,"E13.6.6"),sQuery(id+"F0.wireOp",EDGE,"E13.6.7"),sQuery(id+"F0.wireOp",EDGE,"E13.6.8"),sQuery(id+"F0.wireOp",EDGE,"E13.6.9"),sQuery(id+"F0.wireOp",EDGE,"E13.6.10"),sQuery(id+"F0.wireOp",EDGE,"E13.6.11"),sQuery(id+"F0.wireOp",EDGE,"E13.7.0"),sQuery(id+"F0.wireOp",EDGE,"E13.7.1"),sQuery(id+"F0.wireOp",EDGE,"E13.7.2"),sQuery(id+"F0.wireOp",EDGE,"E13.7.5"),sQuery(id+"F0.wireOp",EDGE,"E13.7.6"),sQuery(id+"F0.wireOp",EDGE,"E13.7.7"),sQuery(id+"F0.wireOp",EDGE,"E13.7.8"),sQuery(id+"F0.wireOp",EDGE,"E13.7.9"),sQuery(id+"F0.wireOp",EDGE,"E13.7.10"),sQuery(id+"F0.wireOp",EDGE,"E13.7.11"),sQuery(id+"F0.wireOp",EDGE,"E13.8.0"),sQuery(id+"F0.wireOp",EDGE,"E13.8.1"),sQuery(id+"F0.wireOp",EDGE,"E13.8.2"),sQuery(id+"F0.wireOp",EDGE,"E13.8.5"),sQuery(id+"F0.wireOp",EDGE,"E13.8.6"),sQuery(id+"F0.wireOp",EDGE,"E13.8.7"),sQuery(id+"F0.wireOp",EDGE,"E13.8.8"),sQuery(id+"F0.wireOp",EDGE,"E13.8.9"),sQuery(id+"F0.wireOp",EDGE,"E13.8.10"),sQuery(id+"F0.wireOp",EDGE,"E13.8.11"),sQuery(id+"F0.wireOp",EDGE,"E3"),sQuery(id+"F0.wireOp",EDGE,"E2"),sQuery(id+"F0.wireOp",EDGE,"E1"),sQuery(id+"F0.wireOp",EDGE,"E4"),sQuery(id+"F0.wireOp",EDGE,"E8"),sQuery(id+"F0.wireOp",EDGE,"E5"),sQuery(id+"F0.wireOp",EDGE,"E11"),sQuery(id+"F0.wireOp",EDGE,"E6"),sQuery(id+"F0.wireOp",EDGE,"E7"),sQuery(id+"F0.wireOp",EDGE,"E10"),sQuery(id+"F0.wireOp",EDGE,"E14"),sQuery(id+"F0.wireOp",EDGE,"E15"),sQuery(id+"F0.wireOp",EDGE,"E20.trimOffspring"),sQuery(id+"F0.wireOp",EDGE,"E21.trimOffspring"),sQuery(id+"F0.wireOp",EDGE,"E22.trimOffspring"),sQuery(id+"F0.wireOp",EDGE,"E23.trimOffspring"),sQuery(id+"F0.wireOp",EDGE,"E24.trimOffspring"),sQuery(id+"F0.wireOp",EDGE,"E25.trimOffspring"),sQuery(id+"F0.wireOp",EDGE,"E26.trimOffspring"),sQuery(id+"F0.wireOp",EDGE,"E27.trimOffspring"),sQuery(id+"F0.wireOp",EDGE,"E28.trimOffspring"),sQuery(id+"F0.wireOp",EDGE,"E29.trimOffspring"),sQuery(id+"F0.wireOp",EDGE,"E30.trimOffspring"),sQuery(id+"F0.wireOp",EDGE,"E31.trimOffspring"),sQuery(id+"F0.wireOp",EDGE,"E32.trimOffspring"),sQuery(id+"F0.wireOp",EDGE,"E33.trimOffspring"),sQuery(id+"F0.wireOp",EDGE,"E34.trimOffspring"),sQuery(id+"F0.wireOp",EDGE,"E35.trimOffspring"),sQuery(id+"F0.wireOp",EDGE,"E36.trimOffspring"),sQuery(id+"F0.wireOp",EDGE,"E37")])]})});
            var Q1;
            Q1=makeQuery(id+"F10.boolean.opBoolean","SPLIT",BODY,{"disambiguationData":[OD(1.0)],"derivedFrom":makeQuery(id+"F1.opExtrude","SWEPT_BODY",BODY,{"disambiguationData":[OSD([sQuery(id+"F0.wireOp",EDGE,"E12.1.0"),sQuery(id+"F0.wireOp",EDGE,"E12.1.1"),sQuery(id+"F0.wireOp",EDGE,"E12.1.2"),sQuery(id+"F0.wireOp",EDGE,"E12.1.3"),sQuery(id+"F0.wireOp",EDGE,"E12.1.4"),sQuery(id+"F0.wireOp",EDGE,"E12.1.5"),sQuery(id+"F0.wireOp",EDGE,"E12.1.6"),sQuery(id+"F0.wireOp",EDGE,"E12.1.7"),sQuery(id+"F0.wireOp",EDGE,"E12.1.10"),sQuery(id+"F0.wireOp",EDGE,"E12.1.11"),sQuery(id+"F0.wireOp",EDGE,"E12.2.0"),sQuery(id+"F0.wireOp",EDGE,"E12.2.1"),sQuery(id+"F0.wireOp",EDGE,"E12.2.2"),sQuery(id+"F0.wireOp",EDGE,"E12.2.3"),sQuery(id+"F0.wireOp",EDGE,"E12.2.4"),sQuery(id+"F0.wireOp",EDGE,"E12.2.5"),sQuery(id+"F0.wireOp",EDGE,"E12.2.6"),sQuery(id+"F0.wireOp",EDGE,"E12.2.7"),sQuery(id+"F0.wireOp",EDGE,"E12.2.10"),sQuery(id+"F0.wireOp",EDGE,"E12.2.11"),sQuery(id+"F0.wireOp",EDGE,"E12.3.0"),sQuery(id+"F0.wireOp",EDGE,"E12.3.1"),sQuery(id+"F0.wireOp",EDGE,"E12.3.2"),sQuery(id+"F0.wireOp",EDGE,"E12.3.3"),sQuery(id+"F0.wireOp",EDGE,"E12.3.4"),sQuery(id+"F0.wireOp",EDGE,"E12.3.5"),sQuery(id+"F0.wireOp",EDGE,"E12.3.6"),sQuery(id+"F0.wireOp",EDGE,"E12.3.7"),sQuery(id+"F0.wireOp",EDGE,"E12.3.10"),sQuery(id+"F0.wireOp",EDGE,"E12.3.11"),sQuery(id+"F0.wireOp",EDGE,"E12.4.0"),sQuery(id+"F0.wireOp",EDGE,"E12.4.1"),sQuery(id+"F0.wireOp",EDGE,"E12.4.2"),sQuery(id+"F0.wireOp",EDGE,"E12.4.3"),sQuery(id+"F0.wireOp",EDGE,"E12.4.4"),sQuery(id+"F0.wireOp",EDGE,"E12.4.5"),sQuery(id+"F0.wireOp",EDGE,"E12.4.6"),sQuery(id+"F0.wireOp",EDGE,"E12.4.7"),sQuery(id+"F0.wireOp",EDGE,"E12.4.10"),sQuery(id+"F0.wireOp",EDGE,"E12.4.11"),sQuery(id+"F0.wireOp",EDGE,"E12.5.0"),sQuery(id+"F0.wireOp",EDGE,"E12.5.1"),sQuery(id+"F0.wireOp",EDGE,"E12.5.2"),sQuery(id+"F0.wireOp",EDGE,"E12.5.3"),sQuery(id+"F0.wireOp",EDGE,"E12.5.4"),sQuery(id+"F0.wireOp",EDGE,"E12.5.5"),sQuery(id+"F0.wireOp",EDGE,"E12.5.6"),sQuery(id+"F0.wireOp",EDGE,"E12.5.7"),sQuery(id+"F0.wireOp",EDGE,"E12.5.10"),sQuery(id+"F0.wireOp",EDGE,"E12.5.11"),sQuery(id+"F0.wireOp",EDGE,"E12.6.0"),sQuery(id+"F0.wireOp",EDGE,"E12.6.1"),sQuery(id+"F0.wireOp",EDGE,"E12.6.2"),sQuery(id+"F0.wireOp",EDGE,"E12.6.3"),sQuery(id+"F0.wireOp",EDGE,"E12.6.4"),sQuery(id+"F0.wireOp",EDGE,"E12.6.5"),sQuery(id+"F0.wireOp",EDGE,"E12.6.6"),sQuery(id+"F0.wireOp",EDGE,"E12.6.7"),sQuery(id+"F0.wireOp",EDGE,"E12.6.10"),sQuery(id+"F0.wireOp",EDGE,"E12.6.11"),sQuery(id+"F0.wireOp",EDGE,"E12.7.0"),sQuery(id+"F0.wireOp",EDGE,"E12.7.1"),sQuery(id+"F0.wireOp",EDGE,"E12.7.2"),sQuery(id+"F0.wireOp",EDGE,"E12.7.3"),sQuery(id+"F0.wireOp",EDGE,"E12.7.4"),sQuery(id+"F0.wireOp",EDGE,"E12.7.5"),sQuery(id+"F0.wireOp",EDGE,"E12.7.6"),sQuery(id+"F0.wireOp",EDGE,"E12.7.7"),sQuery(id+"F0.wireOp",EDGE,"E12.7.10"),sQuery(id+"F0.wireOp",EDGE,"E12.7.11"),sQuery(id+"F0.wireOp",EDGE,"E12.8.0"),sQuery(id+"F0.wireOp",EDGE,"E12.8.1"),sQuery(id+"F0.wireOp",EDGE,"E12.8.2"),sQuery(id+"F0.wireOp",EDGE,"E12.8.3"),sQuery(id+"F0.wireOp",EDGE,"E12.8.4"),sQuery(id+"F0.wireOp",EDGE,"E12.8.5"),sQuery(id+"F0.wireOp",EDGE,"E12.8.6"),sQuery(id+"F0.wireOp",EDGE,"E12.8.7"),sQuery(id+"F0.wireOp",EDGE,"E12.8.10"),sQuery(id+"F0.wireOp",EDGE,"E12.8.11"),sQuery(id+"F0.wireOp",EDGE,"E12.9.0"),sQuery(id+"F0.wireOp",EDGE,"E12.9.1"),sQuery(id+"F0.wireOp",EDGE,"E12.9.2"),sQuery(id+"F0.wireOp",EDGE,"E12.9.3"),sQuery(id+"F0.wireOp",EDGE,"E12.9.4"),sQuery(id+"F0.wireOp",EDGE,"E12.9.5"),sQuery(id+"F0.wireOp",EDGE,"E12.9.6"),sQuery(id+"F0.wireOp",EDGE,"E12.9.7"),sQuery(id+"F0.wireOp",EDGE,"E12.9.10"),sQuery(id+"F0.wireOp",EDGE,"E12.9.11"),sQuery(id+"F0.wireOp",EDGE,"E13.1.0"),sQuery(id+"F0.wireOp",EDGE,"E13.1.1"),sQuery(id+"F0.wireOp",EDGE,"E13.1.2"),sQuery(id+"F0.wireOp",EDGE,"E13.1.5"),sQuery(id+"F0.wireOp",EDGE,"E13.1.6"),sQuery(id+"F0.wireOp",EDGE,"E13.1.7"),sQuery(id+"F0.wireOp",EDGE,"E13.1.8"),sQuery(id+"F0.wireOp",EDGE,"E13.1.9"),sQuery(id+"F0.wireOp",EDGE,"E13.1.10"),sQuery(id+"F0.wireOp",EDGE,"E13.1.11"),sQuery(id+"F0.wireOp",EDGE,"E13.2.0"),sQuery(id+"F0.wireOp",EDGE,"E13.2.1"),sQuery(id+"F0.wireOp",EDGE,"E13.2.2"),sQuery(id+"F0.wireOp",EDGE,"E13.2.5"),sQuery(id+"F0.wireOp",EDGE,"E13.2.6"),sQuery(id+"F0.wireOp",EDGE,"E13.2.7"),sQuery(id+"F0.wireOp",EDGE,"E13.2.8"),sQuery(id+"F0.wireOp",EDGE,"E13.2.9"),sQuery(id+"F0.wireOp",EDGE,"E13.2.10"),sQuery(id+"F0.wireOp",EDGE,"E13.2.11"),sQuery(id+"F0.wireOp",EDGE,"E13.3.0"),sQuery(id+"F0.wireOp",EDGE,"E13.3.1"),sQuery(id+"F0.wireOp",EDGE,"E13.3.2"),sQuery(id+"F0.wireOp",EDGE,"E13.3.5"),sQuery(id+"F0.wireOp",EDGE,"E13.3.6"),sQuery(id+"F0.wireOp",EDGE,"E13.3.7"),sQuery(id+"F0.wireOp",EDGE,"E13.3.8"),sQuery(id+"F0.wireOp",EDGE,"E13.3.9"),sQuery(id+"F0.wireOp",EDGE,"E13.3.10"),sQuery(id+"F0.wireOp",EDGE,"E13.3.11"),sQuery(id+"F0.wireOp",EDGE,"E13.4.0"),sQuery(id+"F0.wireOp",EDGE,"E13.4.1"),sQuery(id+"F0.wireOp",EDGE,"E13.4.2"),sQuery(id+"F0.wireOp",EDGE,"E13.4.5"),sQuery(id+"F0.wireOp",EDGE,"E13.4.6"),sQuery(id+"F0.wireOp",EDGE,"E13.4.7"),sQuery(id+"F0.wireOp",EDGE,"E13.4.8"),sQuery(id+"F0.wireOp",EDGE,"E13.4.9"),sQuery(id+"F0.wireOp",EDGE,"E13.4.10"),sQuery(id+"F0.wireOp",EDGE,"E13.4.11"),sQuery(id+"F0.wireOp",EDGE,"E13.5.0"),sQuery(id+"F0.wireOp",EDGE,"E13.5.1"),sQuery(id+"F0.wireOp",EDGE,"E13.5.2"),sQuery(id+"F0.wireOp",EDGE,"E13.5.5"),sQuery(id+"F0.wireOp",EDGE,"E13.5.6"),sQuery(id+"F0.wireOp",EDGE,"E13.5.7"),sQuery(id+"F0.wireOp",EDGE,"E13.5.8"),sQuery(id+"F0.wireOp",EDGE,"E13.5.9"),sQuery(id+"F0.wireOp",EDGE,"E13.5.10"),sQuery(id+"F0.wireOp",EDGE,"E13.5.11"),sQuery(id+"F0.wireOp",EDGE,"E13.6.0"),sQuery(id+"F0.wireOp",EDGE,"E13.6.1"),sQuery(id+"F0.wireOp",EDGE,"E13.6.2"),sQuery(id+"F0.wireOp",EDGE,"E13.6.5"),sQuery(id+"F0.wireOp",EDGE,"E13.6.6"),sQuery(id+"F0.wireOp",EDGE,"E13.6.7"),sQuery(id+"F0.wireOp",EDGE,"E13.6.8"),sQuery(id+"F0.wireOp",EDGE,"E13.6.9"),sQuery(id+"F0.wireOp",EDGE,"E13.6.10"),sQuery(id+"F0.wireOp",EDGE,"E13.6.11"),sQuery(id+"F0.wireOp",EDGE,"E13.7.0"),sQuery(id+"F0.wireOp",EDGE,"E13.7.1"),sQuery(id+"F0.wireOp",EDGE,"E13.7.2"),sQuery(id+"F0.wireOp",EDGE,"E13.7.5"),sQuery(id+"F0.wireOp",EDGE,"E13.7.6"),sQuery(id+"F0.wireOp",EDGE,"E13.7.7"),sQuery(id+"F0.wireOp",EDGE,"E13.7.8"),sQuery(id+"F0.wireOp",EDGE,"E13.7.9"),sQuery(id+"F0.wireOp",EDGE,"E13.7.10"),sQuery(id+"F0.wireOp",EDGE,"E13.7.11"),sQuery(id+"F0.wireOp",EDGE,"E13.8.0"),sQuery(id+"F0.wireOp",EDGE,"E13.8.1"),sQuery(id+"F0.wireOp",EDGE,"E13.8.2"),sQuery(id+"F0.wireOp",EDGE,"E13.8.5"),sQuery(id+"F0.wireOp",EDGE,"E13.8.6"),sQuery(id+"F0.wireOp",EDGE,"E13.8.7"),sQuery(id+"F0.wireOp",EDGE,"E13.8.8"),sQuery(id+"F0.wireOp",EDGE,"E13.8.9"),sQuery(id+"F0.wireOp",EDGE,"E13.8.10"),sQuery(id+"F0.wireOp",EDGE,"E13.8.11"),sQuery(id+"F0.wireOp",EDGE,"E3"),sQuery(id+"F0.wireOp",EDGE,"E2"),sQuery(id+"F0.wireOp",EDGE,"E1"),sQuery(id+"F0.wireOp",EDGE,"E4"),sQuery(id+"F0.wireOp",EDGE,"E8"),sQuery(id+"F0.wireOp",EDGE,"E5"),sQuery(id+"F0.wireOp",EDGE,"E11"),sQuery(id+"F0.wireOp",EDGE,"E6"),sQuery(id+"F0.wireOp",EDGE,"E7"),sQuery(id+"F0.wireOp",EDGE,"E10"),sQuery(id+"F0.wireOp",EDGE,"E14"),sQuery(id+"F0.wireOp",EDGE,"E15"),sQuery(id+"F0.wireOp",EDGE,"E20.trimOffspring"),sQuery(id+"F0.wireOp",EDGE,"E21.trimOffspring"),sQuery(id+"F0.wireOp",EDGE,"E22.trimOffspring"),sQuery(id+"F0.wireOp",EDGE,"E23.trimOffspring"),sQuery(id+"F0.wireOp",EDGE,"E24.trimOffspring"),sQuery(id+"F0.wireOp",EDGE,"E25.trimOffspring"),sQuery(id+"F0.wireOp",EDGE,"E26.trimOffspring"),sQuery(id+"F0.wireOp",EDGE,"E27.trimOffspring"),sQuery(id+"F0.wireOp",EDGE,"E28.trimOffspring"),sQuery(id+"F0.wireOp",EDGE,"E29.trimOffspring"),sQuery(id+"F0.wireOp",EDGE,"E30.trimOffspring"),sQuery(id+"F0.wireOp",EDGE,"E31.trimOffspring"),sQuery(id+"F0.wireOp",EDGE,"E32.trimOffspring"),sQuery(id+"F0.wireOp",EDGE,"E33.trimOffspring"),sQuery(id+"F0.wireOp",EDGE,"E34.trimOffspring"),sQuery(id+"F0.wireOp",EDGE,"E35.trimOffspring"),sQuery(id+"F0.wireOp",EDGE,"E36.trimOffspring"),sQuery(id+"F0.wireOp",EDGE,"E37")])]})});
            var Q2;
            Q2=makeQuery(id+"F12.opExtrude","SWEPT_BODY",BODY,{"disambiguationData":[OSD([sQuery(id+"F11.wireOp",EDGE,"E142"),sQuery(id+"F11.wireOp",EDGE,"E143.MirrorCS"),sQuery(id+"F11.wireOp",EDGE,"E144"),sQuery(id+"F11.wireOp",EDGE,"E145")])]});
            var Q3;
            Q3=makeQuery(id+"F12.opExtrude","SWEPT_BODY",BODY,{"disambiguationData":[OSD([sQuery(id+"F11.wireOp",EDGE,"E146.1.0"),sQuery(id+"F11.wireOp",EDGE,"E146.1.1"),sQuery(id+"F11.wireOp",EDGE,"E146.1.2"),sQuery(id+"F11.wireOp",EDGE,"E146.1.3")])]});
            var Q4;
            Q4=makeQuery(id+"F12.opExtrude","SWEPT_BODY",BODY,{"disambiguationData":[OSD([sQuery(id+"F11.wireOp",EDGE,"E146.2.0"),sQuery(id+"F11.wireOp",EDGE,"E146.2.1"),sQuery(id+"F11.wireOp",EDGE,"E146.2.2"),sQuery(id+"F11.wireOp",EDGE,"E146.2.3")])]});
            var Q5;
            Q5=makeQuery(id+"F12.opExtrude","SWEPT_BODY",BODY,{"disambiguationData":[OSD([sQuery(id+"F11.wireOp",EDGE,"E146.3.0"),sQuery(id+"F11.wireOp",EDGE,"E146.3.1"),sQuery(id+"F11.wireOp",EDGE,"E146.3.2"),sQuery(id+"F11.wireOp",EDGE,"E146.3.3")])]});
            var Q6;
            Q6=makeQuery(id+"F12.opExtrude","SWEPT_BODY",BODY,{"disambiguationData":[OSD([sQuery(id+"F11.wireOp",EDGE,"E146.4.0"),sQuery(id+"F11.wireOp",EDGE,"E146.4.1"),sQuery(id+"F11.wireOp",EDGE,"E146.4.2"),sQuery(id+"F11.wireOp",EDGE,"E146.4.3")])]});
            var Q7;
            Q7=makeQuery(id+"F12.opExtrude","SWEPT_BODY",BODY,{"disambiguationData":[OSD([sQuery(id+"F11.wireOp",EDGE,"E146.5.0"),sQuery(id+"F11.wireOp",EDGE,"E146.5.1"),sQuery(id+"F11.wireOp",EDGE,"E146.5.2"),sQuery(id+"F11.wireOp",EDGE,"E146.5.3")])]});
            var Q8;
            Q8=makeQuery(id+"F12.opExtrude","SWEPT_BODY",BODY,{"disambiguationData":[OSD([sQuery(id+"F11.wireOp",EDGE,"E146.6.0"),sQuery(id+"F11.wireOp",EDGE,"E146.6.1"),sQuery(id+"F11.wireOp",EDGE,"E146.6.2"),sQuery(id+"F11.wireOp",EDGE,"E146.6.3")])]});
            var Q9;
            Q9=makeQuery(id+"F12.opExtrude","SWEPT_BODY",BODY,{"disambiguationData":[OSD([sQuery(id+"F11.wireOp",EDGE,"E146.7.0"),sQuery(id+"F11.wireOp",EDGE,"E146.7.1"),sQuery(id+"F11.wireOp",EDGE,"E146.7.2"),sQuery(id+"F11.wireOp",EDGE,"E146.7.3")])]});
            booleanBodies(context, id + "F13", {"operationType" : BooleanOperationType.UNION, "tools" : qUnion([Q0, Q1, Q2, Q3, Q4, Q5, Q6, Q7, Q8, Q9])});
        }
        {
            var Q0;
            {var subQ0=sQuery(id+"F5.wireOp",EDGE,"E98.7.0");var subQ1=sQuery(id+"F5.wireOp",EDGE,"E98.6.0");var subQ2=sQuery(id+"F5.wireOp",EDGE,"E134.trimOffspring");var subQ3=sQuery(id+"F5.wireOp",EDGE,"E98.5.1");var subQ4=sQuery(id+"F5.wireOp",EDGE,"E98.3.0");var subQ5=sQuery(id+"F5.wireOp",EDGE,"E110.trimOffspring");var subQ6=sQuery(id+"F5.wireOp",EDGE,"E98.2.5");var subQ7=sQuery(id+"F5.wireOp",EDGE,"E98.2.0");var subQ8=sQuery(id+"F3.wireOp",EDGE,"E80.trimOffspring");var subQ9=sQuery(id+"F5.wireOp",EDGE,"E102.trimOffspring");var subQ10=sQuery(id+"F5.wireOp",EDGE,"E98.1.5");var subQ11=sQuery(id+"F5.wireOp",EDGE,"E98.4.0");var subQ12=sQuery(id+"F5.wireOp",EDGE,"E118.trimOffspring");var subQ13=sQuery(id+"F5.wireOp",EDGE,"E96.trimOffspring");var subQ14=sQuery(id+"F5.wireOp",EDGE,"E98.8.1");var subQ15=sQuery(id+"F5.wireOp",EDGE,"E94.trimOffspring");var subQ16=sQuery(id+"F5.wireOp",EDGE,"E90");var subQ17=sQuery(id+"F5.wireOp",EDGE,"E98.6.1");var subQ18=sQuery(id+"F3.wireOp",EDGE,"E42");var subQ19=sQuery(id+"F3.wireOp",EDGE,"E85.trimOffspring");var subQ20=sQuery(id+"F3.wireOp",EDGE,"E84.trimOffspring");var subQ21=sQuery(id+"F5.wireOp",EDGE,"E98.8.10");var subQ22=sQuery(id+"F3.wireOp",EDGE,"E83.trimOffspring");var subQ23=sQuery(id+"F3.wireOp",EDGE,"E82.trimOffspring");var subQ24=sQuery(id+"F3.wireOp",EDGE,"E81.trimOffspring");var subQ25=sQuery(id+"F3.wireOp",EDGE,"E79.trimOffspring");var subQ26=sQuery(id+"F3.wireOp",EDGE,"E76.trimOffspring");var subQ27=sQuery(id+"F5.wireOp",EDGE,"E98.7.10");var subQ28=sQuery(id+"F3.wireOp",EDGE,"E71.trimOffspring");var subQ29=sQuery(id+"F3.wireOp",EDGE,"E68.trimOffspring");var subQ30=sQuery(id+"F5.wireOp",EDGE,"E114.trimOffspring");var subQ31=sQuery(id+"F3.wireOp",EDGE,"E67.trimOffspring");var subQ32=sQuery(id+"F5.wireOp",EDGE,"E98.1.0");var subQ33=sQuery(id+"F5.wireOp",EDGE,"E98.7.1");var subQ34=sQuery(id+"F3.wireOp",EDGE,"E50.1.0");var subQ35=sQuery(id+"F3.wireOp",EDGE,"E66.trimOffspring");var subQ36=sQuery(id+"F7.wireOp",EDGE,"E137");var subQ37=sQuery(id+"F3.wireOp",EDGE,"E65.trimOffspring");var subQ38=sQuery(id+"F3.wireOp",EDGE,"E64.trimOffspring");var subQ39=sQuery(id+"F3.wireOp",EDGE,"E63.trimOffspring");var subQ40=sQuery(id+"F3.wireOp",EDGE,"E61.trimOffspring");var subQ41=sQuery(id+"F5.wireOp",EDGE,"E119.trimOffspring");var subQ42=sQuery(id+"F5.wireOp",EDGE,"E98.2.1");var subQ43=sQuery(id+"F3.wireOp",EDGE,"E50.5.0");var subQ44=sQuery(id+"F3.wireOp",EDGE,"E86.trimOffspring");var subQ45=sQuery(id+"F5.wireOp",EDGE,"E98.4.1");var subQ46=sQuery(id+"F3.wireOp",EDGE,"E50.2.5");var subQ47=sQuery(id+"F3.wireOp",EDGE,"E62.trimOffspring");var subQ48=sQuery(id+"F5.wireOp",EDGE,"E98.8.5");var subQ49=sQuery(id+"F3.wireOp",EDGE,"E50.4.10");var subQ50=sQuery(id+"F3.wireOp",EDGE,"E50.4.5");var subQ51=sQuery(id+"F5.wireOp",EDGE,"E98.7.5");var subQ52=sQuery(id+"F3.wireOp",EDGE,"E50.4.1");var subQ53=sQuery(id+"F3.wireOp",EDGE,"E72.trimOffspring");var subQ54=sQuery(id+"F3.wireOp",EDGE,"E50.6.10");var subQ55=sQuery(id+"F5.wireOp",EDGE,"E133.trimOffspring");var subQ56=sQuery(id+"F3.wireOp",EDGE,"E50.8.5");var subQ57=sQuery(id+"F3.wireOp",EDGE,"E50.4.0");var subQ58=sQuery(id+"F5.wireOp",EDGE,"E98.1.10");var subQ59=sQuery(id+"F3.wireOp",EDGE,"E70.trimOffspring");var subQ60=sQuery(id+"F5.wireOp",EDGE,"E101.trimOffspring");var subQ61=sQuery(id+"F3.wireOp",EDGE,"E50.8.1");var subQ62=sQuery(id+"F3.wireOp",EDGE,"E50.3.10");var subQ63=sQuery(id+"F3.wireOp",EDGE,"E50.8.0");var subQ64=sQuery(id+"F3.wireOp",EDGE,"E50.5.1");var subQ65=sQuery(id+"F3.wireOp",EDGE,"E73.trimOffspring");var subQ66=sQuery(id+"F3.wireOp",EDGE,"E50.7.0");var subQ67=sQuery(id+"F3.wireOp",EDGE,"E50.2.10");var subQ68=sQuery(id+"F3.wireOp",EDGE,"E75.trimOffspring");var subQ69=sQuery(id+"F3.wireOp",EDGE,"E50.1.5");var subQ70=sQuery(id+"F3.wireOp",EDGE,"E48.trimOffspring");var subQ71=sQuery(id+"F3.wireOp",EDGE,"E50.2.1");var subQ72=sQuery(id+"F3.wireOp",EDGE,"E47.trimOffspring");var subQ73=sQuery(id+"F3.wireOp",EDGE,"E50.1.10");var subQ74=sQuery(id+"F3.wireOp",EDGE,"E77.trimOffspring");var subQ75=sQuery(id+"F3.wireOp",EDGE,"E78.trimOffspring");var subQ76=sQuery(id+"F3.wireOp",EDGE,"E50.3.5");var subQ77=sQuery(id+"F3.wireOp",EDGE,"E50.2.0");var subQ78=sQuery(id+"F3.wireOp",EDGE,"E52.trimOffspring");var subQ79=sQuery(id+"F5.wireOp",EDGE,"E130.trimOffspring");var subQ80=sQuery(id+"F3.wireOp",EDGE,"E50.1.1");var subQ81=sQuery(id+"F3.wireOp",EDGE,"E50.5.5");var subQ82=sQuery(id+"F5.wireOp",EDGE,"E112.trimOffspring");var subQ83=sQuery(id+"F3.wireOp",EDGE,"E50.3.1");var subQ84=sQuery(id+"F3.wireOp",EDGE,"E50.5.10");var subQ85=sQuery(id+"F3.wireOp",EDGE,"E50.6.0");var subQ86=sQuery(id+"F3.wireOp",EDGE,"E50.7.5");var subQ87=sQuery(id+"F3.wireOp",EDGE,"E69.trimOffspring");var subQ88=sQuery(id+"F5.wireOp",EDGE,"E127.trimOffspring");var subQ89=sQuery(id+"F3.wireOp",EDGE,"E57.trimOffspring");var subQ90=sQuery(id+"F5.wireOp",EDGE,"E111.trimOffspring");var subQ91=sQuery(id+"F5.wireOp",EDGE,"E98.5.0");var subQ92=sQuery(id+"F5.wireOp",EDGE,"E126.trimOffspring");var subQ93=sQuery(id+"F3.wireOp",EDGE,"E50.6.1");var subQ94=sQuery(id+"F3.wireOp",EDGE,"E46.trimOffspring");var subQ95=sQuery(id+"F3.wireOp",EDGE,"E58.trimOffspring");var subQ96=sQuery(id+"F3.wireOp",EDGE,"E59.trimOffspring");var subQ97=sQuery(id+"F5.wireOp",EDGE,"E98.3.1");var subQ98=sQuery(id+"F3.wireOp",EDGE,"E50.6.5");var subQ99=sQuery(id+"F3.wireOp",EDGE,"E50.7.10");var subQ100=sQuery(id+"F5.wireOp",EDGE,"E122.trimOffspring");var subQ101=sQuery(id+"F3.wireOp",EDGE,"E60.trimOffspring");var subQ102=sQuery(id+"F5.wireOp",EDGE,"E106.trimOffspring");var subQ103=sQuery(id+"F3.wireOp",EDGE,"E74.trimOffspring");var subQ104=sQuery(id+"F3.wireOp",EDGE,"E50.3.0");var subQ105=sQuery(id+"F3.wireOp",EDGE,"E50.7.1");var subQ106=sQuery(id+"F3.wireOp",EDGE,"E50.8.10");var subQ107=sQuery(id+"F5.wireOp",EDGE,"E98.1.1");var subQ108=sQuery(id+"F3.wireOp",EDGE,"E51.trimOffspring");var subQ109=sQuery(id+"F3.wireOp",EDGE,"E53.trimOffspring");var subQ110=sQuery(id+"F5.wireOp",EDGE,"E104.trimOffspring");var subQ111=sQuery(id+"F5.wireOp",EDGE,"E98.2.10");var subQ112=sQuery(id+"F5.wireOp",EDGE,"E109.trimOffspring");var subQ113=sQuery(id+"F3.wireOp",EDGE,"E54.trimOffspring");var subQ114=sQuery(id+"F5.wireOp",EDGE,"E117.trimOffspring");var subQ115=sQuery(id+"F5.wireOp",EDGE,"E95.trimOffspring");var subQ116=sQuery(id+"F3.wireOp",EDGE,"E55.trimOffspring");var subQ117=sQuery(id+"F3.wireOp",EDGE,"E56.trimOffspring");var subQ118=sQuery(id+"F5.wireOp",EDGE,"E98.8.0");var subQ119=sQuery(id+"F5.wireOp",EDGE,"E99.trimOffspring");var subQ120=sQuery(id+"F5.wireOp",EDGE,"E100.trimOffspring");var subQ121=sQuery(id+"F5.wireOp",EDGE,"E103.trimOffspring");var subQ122=sQuery(id+"F5.wireOp",EDGE,"E105.trimOffspring");var subQ123=sQuery(id+"F5.wireOp",EDGE,"E107.trimOffspring");var subQ124=sQuery(id+"F5.wireOp",EDGE,"E108.trimOffspring");var subQ125=sQuery(id+"F5.wireOp",EDGE,"E113.trimOffspring");var subQ126=sQuery(id+"F5.wireOp",EDGE,"E115.trimOffspring");var subQ127=sQuery(id+"F5.wireOp",EDGE,"E116.trimOffspring");var subQ128=sQuery(id+"F5.wireOp",EDGE,"E120.trimOffspring");var subQ129=sQuery(id+"F5.wireOp",EDGE,"E121.trimOffspring");var subQ130=sQuery(id+"F5.wireOp",EDGE,"E123.trimOffspring");var subQ131=sQuery(id+"F5.wireOp",EDGE,"E124.trimOffspring");var subQ132=sQuery(id+"F5.wireOp",EDGE,"E125.trimOffspring");var subQ133=sQuery(id+"F5.wireOp",EDGE,"E128.trimOffspring");var subQ134=sQuery(id+"F5.wireOp",EDGE,"E129.trimOffspring");var subQ135=sQuery(id+"F5.wireOp",EDGE,"E131.trimOffspring");var subQ136=sQuery(id+"F5.wireOp",EDGE,"E132.trimOffspring");var subQ137=sQuery(id+"F0.wireOp",EDGE,"E15");var subQ138=sQuery(id+"F0.wireOp",EDGE,"E37");var subQ139=sQuery(id+"F0.wireOp",EDGE,"E36.trimOffspring");var subQ140=sQuery(id+"F0.wireOp",EDGE,"E35.trimOffspring");var subQ141=sQuery(id+"F0.wireOp",EDGE,"E34.trimOffspring");var subQ142=sQuery(id+"F0.wireOp",EDGE,"E33.trimOffspring");var subQ143=sQuery(id+"F0.wireOp",EDGE,"E32.trimOffspring");var subQ144=sQuery(id+"F0.wireOp",EDGE,"E31.trimOffspring");var subQ145=sQuery(id+"F0.wireOp",EDGE,"E30.trimOffspring");var subQ146=sQuery(id+"F0.wireOp",EDGE,"E29.trimOffspring");var subQ147=sQuery(id+"F0.wireOp",EDGE,"E28.trimOffspring");var subQ148=sQuery(id+"F0.wireOp",EDGE,"E27.trimOffspring");var subQ149=sQuery(id+"F0.wireOp",EDGE,"E26.trimOffspring");var subQ150=sQuery(id+"F0.wireOp",EDGE,"E25.trimOffspring");var subQ151=sQuery(id+"F0.wireOp",EDGE,"E24.trimOffspring");var subQ152=sQuery(id+"F0.wireOp",EDGE,"E23.trimOffspring");var subQ153=sQuery(id+"F0.wireOp",EDGE,"E22.trimOffspring");var subQ154=sQuery(id+"F0.wireOp",EDGE,"E21.trimOffspring");var subQ155=sQuery(id+"F0.wireOp",EDGE,"E20.trimOffspring");var subQ156=sQuery(id+"F0.wireOp",EDGE,"E14");var subQ157=sQuery(id+"F0.wireOp",EDGE,"E5");var subQ158=sQuery(id+"F0.wireOp",EDGE,"E8");var subQ159=sQuery(id+"F0.wireOp",EDGE,"E4");var subQ160=sQuery(id+"F0.wireOp",EDGE,"E1");var subQ161=sQuery(id+"F0.wireOp",EDGE,"E2");var subQ162=sQuery(id+"F0.wireOp",EDGE,"E3");var subQ163=sQuery(id+"F0.wireOp",EDGE,"E13.8.7");var subQ164=sQuery(id+"F0.wireOp",EDGE,"E13.8.6");var subQ165=sQuery(id+"F0.wireOp",EDGE,"E13.8.5");var subQ166=sQuery(id+"F0.wireOp",EDGE,"E13.8.2");var subQ167=sQuery(id+"F0.wireOp",EDGE,"E13.8.1");var subQ168=sQuery(id+"F0.wireOp",EDGE,"E13.8.0");var subQ169=sQuery(id+"F0.wireOp",EDGE,"E13.7.7");var subQ170=sQuery(id+"F0.wireOp",EDGE,"E13.7.6");var subQ171=sQuery(id+"F0.wireOp",EDGE,"E13.7.5");var subQ172=sQuery(id+"F0.wireOp",EDGE,"E13.7.2");var subQ173=sQuery(id+"F0.wireOp",EDGE,"E13.7.1");var subQ174=sQuery(id+"F0.wireOp",EDGE,"E13.7.0");var subQ175=sQuery(id+"F0.wireOp",EDGE,"E13.6.7");var subQ176=sQuery(id+"F0.wireOp",EDGE,"E13.6.6");var subQ177=sQuery(id+"F0.wireOp",EDGE,"E13.6.5");var subQ178=sQuery(id+"F0.wireOp",EDGE,"E13.6.2");var subQ179=sQuery(id+"F0.wireOp",EDGE,"E13.6.1");var subQ180=sQuery(id+"F0.wireOp",EDGE,"E13.6.0");var subQ181=sQuery(id+"F0.wireOp",EDGE,"E13.5.7");var subQ182=sQuery(id+"F0.wireOp",EDGE,"E13.5.6");var subQ183=sQuery(id+"F0.wireOp",EDGE,"E13.5.5");var subQ184=sQuery(id+"F0.wireOp",EDGE,"E13.5.2");var subQ185=sQuery(id+"F0.wireOp",EDGE,"E13.5.1");var subQ186=sQuery(id+"F0.wireOp",EDGE,"E13.5.0");var subQ187=sQuery(id+"F0.wireOp",EDGE,"E13.4.7");var subQ188=sQuery(id+"F0.wireOp",EDGE,"E13.4.6");var subQ189=sQuery(id+"F0.wireOp",EDGE,"E13.4.5");var subQ190=sQuery(id+"F0.wireOp",EDGE,"E13.4.2");var subQ191=sQuery(id+"F0.wireOp",EDGE,"E13.4.1");var subQ192=sQuery(id+"F0.wireOp",EDGE,"E13.4.0");var subQ193=sQuery(id+"F0.wireOp",EDGE,"E13.3.7");var subQ194=sQuery(id+"F0.wireOp",EDGE,"E13.3.6");var subQ195=sQuery(id+"F0.wireOp",EDGE,"E13.3.5");var subQ196=sQuery(id+"F0.wireOp",EDGE,"E13.3.2");var subQ197=sQuery(id+"F0.wireOp",EDGE,"E13.3.1");var subQ198=sQuery(id+"F0.wireOp",EDGE,"E13.3.0");var subQ199=sQuery(id+"F0.wireOp",EDGE,"E13.2.7");var subQ200=sQuery(id+"F0.wireOp",EDGE,"E13.2.6");var subQ201=sQuery(id+"F0.wireOp",EDGE,"E13.2.5");var subQ202=sQuery(id+"F0.wireOp",EDGE,"E13.2.2");var subQ203=sQuery(id+"F0.wireOp",EDGE,"E13.2.1");var subQ204=sQuery(id+"F0.wireOp",EDGE,"E13.2.0");var subQ205=sQuery(id+"F0.wireOp",EDGE,"E13.1.7");var subQ206=sQuery(id+"F0.wireOp",EDGE,"E13.1.6");var subQ207=sQuery(id+"F0.wireOp",EDGE,"E13.1.5");var subQ208=sQuery(id+"F0.wireOp",EDGE,"E13.1.2");var subQ209=sQuery(id+"F0.wireOp",EDGE,"E13.1.1");var subQ210=sQuery(id+"F0.wireOp",EDGE,"E13.1.0");var subQ211=sQuery(id+"F0.wireOp",EDGE,"E12.9.11");var subQ212=sQuery(id+"F0.wireOp",EDGE,"E12.9.10");var subQ213=sQuery(id+"F0.wireOp",EDGE,"E12.9.5");var subQ214=sQuery(id+"F0.wireOp",EDGE,"E12.9.4");var subQ215=sQuery(id+"F0.wireOp",EDGE,"E12.9.1");var subQ216=sQuery(id+"F0.wireOp",EDGE,"E12.9.0");var subQ217=sQuery(id+"F0.wireOp",EDGE,"E12.8.11");var subQ218=sQuery(id+"F0.wireOp",EDGE,"E12.8.10");var subQ219=sQuery(id+"F0.wireOp",EDGE,"E12.8.5");var subQ220=sQuery(id+"F0.wireOp",EDGE,"E12.8.4");var subQ221=sQuery(id+"F0.wireOp",EDGE,"E12.8.1");var subQ222=sQuery(id+"F0.wireOp",EDGE,"E12.8.0");var subQ223=sQuery(id+"F0.wireOp",EDGE,"E12.7.11");var subQ224=sQuery(id+"F0.wireOp",EDGE,"E12.7.10");var subQ225=sQuery(id+"F0.wireOp",EDGE,"E12.7.5");var subQ226=sQuery(id+"F0.wireOp",EDGE,"E12.7.4");var subQ227=sQuery(id+"F0.wireOp",EDGE,"E12.7.1");var subQ228=sQuery(id+"F0.wireOp",EDGE,"E12.7.0");var subQ229=sQuery(id+"F0.wireOp",EDGE,"E12.6.11");var subQ230=sQuery(id+"F0.wireOp",EDGE,"E12.6.10");var subQ231=sQuery(id+"F0.wireOp",EDGE,"E12.6.5");var subQ232=sQuery(id+"F0.wireOp",EDGE,"E12.6.4");var subQ233=sQuery(id+"F0.wireOp",EDGE,"E12.6.1");var subQ234=sQuery(id+"F0.wireOp",EDGE,"E12.6.0");var subQ235=sQuery(id+"F0.wireOp",EDGE,"E12.5.11");var subQ236=sQuery(id+"F0.wireOp",EDGE,"E12.5.10");var subQ237=sQuery(id+"F0.wireOp",EDGE,"E12.5.5");var subQ238=sQuery(id+"F0.wireOp",EDGE,"E12.5.4");var subQ239=sQuery(id+"F0.wireOp",EDGE,"E12.5.1");var subQ240=sQuery(id+"F0.wireOp",EDGE,"E12.5.0");var subQ241=sQuery(id+"F0.wireOp",EDGE,"E12.4.11");var subQ242=sQuery(id+"F0.wireOp",EDGE,"E12.4.10");var subQ243=sQuery(id+"F0.wireOp",EDGE,"E12.4.5");var subQ244=sQuery(id+"F0.wireOp",EDGE,"E12.4.4");var subQ245=sQuery(id+"F0.wireOp",EDGE,"E12.4.1");var subQ246=sQuery(id+"F0.wireOp",EDGE,"E12.4.0");var subQ247=sQuery(id+"F0.wireOp",EDGE,"E12.3.11");var subQ248=sQuery(id+"F0.wireOp",EDGE,"E12.3.10");var subQ249=sQuery(id+"F0.wireOp",EDGE,"E12.3.5");var subQ250=sQuery(id+"F0.wireOp",EDGE,"E12.3.4");var subQ251=sQuery(id+"F0.wireOp",EDGE,"E12.3.1");var subQ252=sQuery(id+"F0.wireOp",EDGE,"E12.3.0");var subQ253=sQuery(id+"F0.wireOp",EDGE,"E12.2.11");var subQ254=sQuery(id+"F0.wireOp",EDGE,"E12.2.10");var subQ255=sQuery(id+"F0.wireOp",EDGE,"E12.2.5");var subQ256=sQuery(id+"F0.wireOp",EDGE,"E12.2.4");var subQ257=sQuery(id+"F0.wireOp",EDGE,"E12.2.1");var subQ258=sQuery(id+"F0.wireOp",EDGE,"E12.2.0");var subQ259=sQuery(id+"F0.wireOp",EDGE,"E12.1.11");var subQ260=sQuery(id+"F0.wireOp",EDGE,"E12.1.10");var subQ261=sQuery(id+"F0.wireOp",EDGE,"E12.1.5");var subQ262=sQuery(id+"F0.wireOp",EDGE,"E12.1.4");var subQ263=sQuery(id+"F0.wireOp",EDGE,"E12.1.1");var subQ264=sQuery(id+"F0.wireOp",EDGE,"E12.1.0");var subQ265=makeQuery(id+"F8.boolean.opBoolean","MERGE",FACE,{"derivedFrom":[makeQuery(id+"F6.boolean.opBoolean","MERGE",FACE,{"derivedFrom":[makeQuery(id+"F4.boolean.opBoolean","MERGE",FACE,{"derivedFrom":[makeQuery(id+"F2.opChamfer","SPLIT",FACE,{"disambiguationData":[OD(18.0)],"derivedFrom":makeQuery(id+"F1.opExtrude","CAP_FACE",FACE,{"disambiguationData":[OSD([subQ264,subQ263,sQuery(id+"F0.wireOp",EDGE,"E12.1.2"),sQuery(id+"F0.wireOp",EDGE,"E12.1.3"),subQ262,subQ261,sQuery(id+"F0.wireOp",EDGE,"E12.1.6"),sQuery(id+"F0.wireOp",EDGE,"E12.1.7"),subQ260,subQ259,subQ258,subQ257,sQuery(id+"F0.wireOp",EDGE,"E12.2.2"),sQuery(id+"F0.wireOp",EDGE,"E12.2.3"),subQ256,subQ255,sQuery(id+"F0.wireOp",EDGE,"E12.2.6"),sQuery(id+"F0.wireOp",EDGE,"E12.2.7"),subQ254,subQ253,subQ252,subQ251,sQuery(id+"F0.wireOp",EDGE,"E12.3.2"),sQuery(id+"F0.wireOp",EDGE,"E12.3.3"),subQ250,subQ249,sQuery(id+"F0.wireOp",EDGE,"E12.3.6"),sQuery(id+"F0.wireOp",EDGE,"E12.3.7"),subQ248,subQ247,subQ246,subQ245,sQuery(id+"F0.wireOp",EDGE,"E12.4.2"),sQuery(id+"F0.wireOp",EDGE,"E12.4.3"),subQ244,subQ243,sQuery(id+"F0.wireOp",EDGE,"E12.4.6"),sQuery(id+"F0.wireOp",EDGE,"E12.4.7"),subQ242,subQ241,subQ240,subQ239,sQuery(id+"F0.wireOp",EDGE,"E12.5.2"),sQuery(id+"F0.wireOp",EDGE,"E12.5.3"),subQ238,subQ237,sQuery(id+"F0.wireOp",EDGE,"E12.5.6"),sQuery(id+"F0.wireOp",EDGE,"E12.5.7"),subQ236,subQ235,subQ234,subQ233,sQuery(id+"F0.wireOp",EDGE,"E12.6.2"),sQuery(id+"F0.wireOp",EDGE,"E12.6.3"),subQ232,subQ231,sQuery(id+"F0.wireOp",EDGE,"E12.6.6"),sQuery(id+"F0.wireOp",EDGE,"E12.6.7"),subQ230,subQ229,subQ228,subQ227,sQuery(id+"F0.wireOp",EDGE,"E12.7.2"),sQuery(id+"F0.wireOp",EDGE,"E12.7.3"),subQ226,subQ225,sQuery(id+"F0.wireOp",EDGE,"E12.7.6"),sQuery(id+"F0.wireOp",EDGE,"E12.7.7"),subQ224,subQ223,subQ222,subQ221,sQuery(id+"F0.wireOp",EDGE,"E12.8.2"),sQuery(id+"F0.wireOp",EDGE,"E12.8.3"),subQ220,subQ219,sQuery(id+"F0.wireOp",EDGE,"E12.8.6"),sQuery(id+"F0.wireOp",EDGE,"E12.8.7"),subQ218,subQ217,subQ216,subQ215,sQuery(id+"F0.wireOp",EDGE,"E12.9.2"),sQuery(id+"F0.wireOp",EDGE,"E12.9.3"),subQ214,subQ213,sQuery(id+"F0.wireOp",EDGE,"E12.9.6"),sQuery(id+"F0.wireOp",EDGE,"E12.9.7"),subQ212,subQ211,subQ210,subQ209,subQ208,subQ207,subQ206,subQ205,sQuery(id+"F0.wireOp",EDGE,"E13.1.8"),sQuery(id+"F0.wireOp",EDGE,"E13.1.9"),sQuery(id+"F0.wireOp",EDGE,"E13.1.10"),sQuery(id+"F0.wireOp",EDGE,"E13.1.11"),subQ204,subQ203,subQ202,subQ201,subQ200,subQ199,sQuery(id+"F0.wireOp",EDGE,"E13.2.8"),sQuery(id+"F0.wireOp",EDGE,"E13.2.9"),sQuery(id+"F0.wireOp",EDGE,"E13.2.10"),sQuery(id+"F0.wireOp",EDGE,"E13.2.11"),subQ198,subQ197,subQ196,subQ195,subQ194,subQ193,sQuery(id+"F0.wireOp",EDGE,"E13.3.8"),sQuery(id+"F0.wireOp",EDGE,"E13.3.9"),sQuery(id+"F0.wireOp",EDGE,"E13.3.10"),sQuery(id+"F0.wireOp",EDGE,"E13.3.11"),subQ192,subQ191,subQ190,subQ189,subQ188,subQ187,sQuery(id+"F0.wireOp",EDGE,"E13.4.8"),sQuery(id+"F0.wireOp",EDGE,"E13.4.9"),sQuery(id+"F0.wireOp",EDGE,"E13.4.10"),sQuery(id+"F0.wireOp",EDGE,"E13.4.11"),subQ186,subQ185,subQ184,subQ183,subQ182,subQ181,sQuery(id+"F0.wireOp",EDGE,"E13.5.8"),sQuery(id+"F0.wireOp",EDGE,"E13.5.9"),sQuery(id+"F0.wireOp",EDGE,"E13.5.10"),sQuery(id+"F0.wireOp",EDGE,"E13.5.11"),subQ180,subQ179,subQ178,subQ177,subQ176,subQ175,sQuery(id+"F0.wireOp",EDGE,"E13.6.8"),sQuery(id+"F0.wireOp",EDGE,"E13.6.9"),sQuery(id+"F0.wireOp",EDGE,"E13.6.10"),sQuery(id+"F0.wireOp",EDGE,"E13.6.11"),subQ174,subQ173,subQ172,subQ171,subQ170,subQ169,sQuery(id+"F0.wireOp",EDGE,"E13.7.8"),sQuery(id+"F0.wireOp",EDGE,"E13.7.9"),sQuery(id+"F0.wireOp",EDGE,"E13.7.10"),sQuery(id+"F0.wireOp",EDGE,"E13.7.11"),subQ168,subQ167,subQ166,subQ165,subQ164,subQ163,sQuery(id+"F0.wireOp",EDGE,"E13.8.8"),sQuery(id+"F0.wireOp",EDGE,"E13.8.9"),sQuery(id+"F0.wireOp",EDGE,"E13.8.10"),sQuery(id+"F0.wireOp",EDGE,"E13.8.11"),subQ162,subQ161,subQ160,subQ159,subQ158,subQ157,sQuery(id+"F0.wireOp",EDGE,"E11"),sQuery(id+"F0.wireOp",EDGE,"E6"),sQuery(id+"F0.wireOp",EDGE,"E7"),sQuery(id+"F0.wireOp",EDGE,"E10"),subQ156,subQ137,subQ155,subQ154,subQ153,subQ152,subQ151,subQ150,subQ149,subQ148,subQ147,subQ146,subQ145,subQ144,subQ143,subQ142,subQ141,subQ140,subQ139,subQ138])],"isStart":false})}),makeQuery(id+"F4.opExtrude","CAP_FACE",FACE,{"disambiguationData":[OSD([subQ137,subQ18,sQuery(id+"F3.wireOp",EDGE,"E43.0"),subQ94,subQ72,subQ70,sQuery(id+"F3.wireOp",EDGE,"E49.trimOffspring"),subQ34,subQ80,subQ69,sQuery(id+"F3.wireOp",EDGE,"E50.1.6"),sQuery(id+"F3.wireOp",EDGE,"E50.1.8"),subQ73,subQ77,subQ71,subQ46,sQuery(id+"F3.wireOp",EDGE,"E50.2.6"),sQuery(id+"F3.wireOp",EDGE,"E50.2.8"),subQ67,subQ104,subQ83,subQ76,sQuery(id+"F3.wireOp",EDGE,"E50.3.6"),sQuery(id+"F3.wireOp",EDGE,"E50.3.8"),subQ62,subQ57,subQ52,subQ50,sQuery(id+"F3.wireOp",EDGE,"E50.4.6"),sQuery(id+"F3.wireOp",EDGE,"E50.4.8"),subQ49,subQ43,subQ64,subQ81,sQuery(id+"F3.wireOp",EDGE,"E50.5.6"),sQuery(id+"F3.wireOp",EDGE,"E50.5.8"),subQ84,subQ85,subQ93,subQ98,sQuery(id+"F3.wireOp",EDGE,"E50.6.6"),sQuery(id+"F3.wireOp",EDGE,"E50.6.8"),subQ54,subQ66,subQ105,subQ86,sQuery(id+"F3.wireOp",EDGE,"E50.7.6"),sQuery(id+"F3.wireOp",EDGE,"E50.7.8"),subQ99,subQ63,subQ61,subQ56,sQuery(id+"F3.wireOp",EDGE,"E50.8.6"),sQuery(id+"F3.wireOp",EDGE,"E50.8.8"),subQ106,subQ108,subQ78,subQ109,subQ113,subQ116,subQ117,subQ89,subQ95,subQ96,subQ101,subQ40,subQ47,subQ39,subQ38,subQ37,subQ35,subQ31,subQ29,subQ87,subQ59,subQ28,subQ53,subQ65,subQ103,subQ68,subQ26,subQ74,subQ75,subQ25,subQ8,subQ24,subQ23,subQ22,subQ20,subQ19,subQ44])],"isStart":false})]}),makeQuery(id+"F6.opExtrude","CAP_FACE",FACE,{"disambiguationData":[OSD([sQuery(id+"F5.wireOp",EDGE,"E88"),sQuery(id+"F5.wireOp",EDGE,"E89"),subQ16,sQuery(id+"F5.wireOp",EDGE,"E91.0"),sQuery(id+"F5.wireOp",EDGE,"E92"),sQuery(id+"F5.wireOp",EDGE,"E93"),subQ15,subQ115,subQ13,sQuery(id+"F5.wireOp",EDGE,"E97.trimOffspring"),subQ32,subQ107,subQ10,sQuery(id+"F5.wireOp",EDGE,"E98.1.6"),sQuery(id+"F5.wireOp",EDGE,"E98.1.7"),sQuery(id+"F5.wireOp",EDGE,"E98.1.8"),sQuery(id+"F5.wireOp",EDGE,"E98.1.9"),subQ58,subQ7,subQ42,subQ6,sQuery(id+"F5.wireOp",EDGE,"E98.2.6"),sQuery(id+"F5.wireOp",EDGE,"E98.2.7"),sQuery(id+"F5.wireOp",EDGE,"E98.2.8"),sQuery(id+"F5.wireOp",EDGE,"E98.2.9"),subQ111,subQ4,subQ97,sQuery(id+"F5.wireOp",EDGE,"E98.3.5"),sQuery(id+"F5.wireOp",EDGE,"E98.3.6"),sQuery(id+"F5.wireOp",EDGE,"E98.3.7"),sQuery(id+"F5.wireOp",EDGE,"E98.3.8"),sQuery(id+"F5.wireOp",EDGE,"E98.3.9"),sQuery(id+"F5.wireOp",EDGE,"E98.3.10"),subQ11,subQ45,sQuery(id+"F5.wireOp",EDGE,"E98.4.5"),sQuery(id+"F5.wireOp",EDGE,"E98.4.6"),sQuery(id+"F5.wireOp",EDGE,"E98.4.7"),sQuery(id+"F5.wireOp",EDGE,"E98.4.8"),sQuery(id+"F5.wireOp",EDGE,"E98.4.9"),sQuery(id+"F5.wireOp",EDGE,"E98.4.10"),subQ91,subQ3,sQuery(id+"F5.wireOp",EDGE,"E98.5.5"),sQuery(id+"F5.wireOp",EDGE,"E98.5.6"),sQuery(id+"F5.wireOp",EDGE,"E98.5.7"),sQuery(id+"F5.wireOp",EDGE,"E98.5.8"),sQuery(id+"F5.wireOp",EDGE,"E98.5.9"),sQuery(id+"F5.wireOp",EDGE,"E98.5.10"),subQ1,subQ17,sQuery(id+"F5.wireOp",EDGE,"E98.6.5"),sQuery(id+"F5.wireOp",EDGE,"E98.6.6"),sQuery(id+"F5.wireOp",EDGE,"E98.6.7"),sQuery(id+"F5.wireOp",EDGE,"E98.6.8"),sQuery(id+"F5.wireOp",EDGE,"E98.6.9"),sQuery(id+"F5.wireOp",EDGE,"E98.6.10"),subQ0,subQ33,subQ51,sQuery(id+"F5.wireOp",EDGE,"E98.7.6"),sQuery(id+"F5.wireOp",EDGE,"E98.7.7"),sQuery(id+"F5.wireOp",EDGE,"E98.7.8"),sQuery(id+"F5.wireOp",EDGE,"E98.7.9"),subQ27,subQ118,subQ14,subQ48,sQuery(id+"F5.wireOp",EDGE,"E98.8.6"),sQuery(id+"F5.wireOp",EDGE,"E98.8.7"),sQuery(id+"F5.wireOp",EDGE,"E98.8.8"),sQuery(id+"F5.wireOp",EDGE,"E98.8.9"),subQ21,subQ119,subQ120,subQ60,subQ9,subQ121,subQ110,subQ122,subQ102,subQ123,subQ124,subQ112,subQ5,subQ90,subQ82,subQ125,subQ30,subQ126,subQ127,subQ114,subQ12,subQ41,subQ128,subQ129,subQ100,subQ130,subQ131,subQ132,subQ92,subQ88,subQ133,subQ134,subQ79,subQ135,subQ136,subQ55,subQ2])],"isStart":true})]}),makeQuery(id+"F8.opExtrude","CAP_FACE",FACE,{"disambiguationData":[OSD([sQuery(id+"F7.wireOp",EDGE,"E135"),subQ36])],"isStart":true})]});Q0=makeQuery(id+"F13.opBoolean","MERGE",FACE,{"derivedFrom":[makeQuery(id+"F10.boolean.opBoolean","SPLIT",FACE,{"disambiguationData":[TD([makeQuery(id+"F1.opExtrude","SWEPT_FACE",FACE,{"disambiguationData":[OSD([subQ262])]})])],"derivedFrom":subQ265}),makeQuery(id+"F10.boolean.opBoolean","SPLIT",FACE,{"disambiguationData":[TD([makeQuery(id+"F4.opExtrude","SWEPT_FACE",FACE,{"disambiguationData":[OSD([subQ18])]})])],"derivedFrom":subQ265}),makeQuery(id+"F12.opExtrude","CAP_FACE",FACE,{"disambiguationData":[OSD([sQuery(id+"F11.wireOp",EDGE,"E142"),sQuery(id+"F11.wireOp",EDGE,"E143.MirrorCS"),sQuery(id+"F11.wireOp",EDGE,"E144"),sQuery(id+"F11.wireOp",EDGE,"E145")])],"isStart":true}),makeQuery(id+"F12.opExtrude","CAP_FACE",FACE,{"disambiguationData":[OSD([sQuery(id+"F11.wireOp",EDGE,"E146.1.0"),sQuery(id+"F11.wireOp",EDGE,"E146.1.1"),sQuery(id+"F11.wireOp",EDGE,"E146.1.2"),sQuery(id+"F11.wireOp",EDGE,"E146.1.3")])],"isStart":true}),makeQuery(id+"F12.opExtrude","CAP_FACE",FACE,{"disambiguationData":[OSD([sQuery(id+"F11.wireOp",EDGE,"E146.2.0"),sQuery(id+"F11.wireOp",EDGE,"E146.2.1"),sQuery(id+"F11.wireOp",EDGE,"E146.2.2"),sQuery(id+"F11.wireOp",EDGE,"E146.2.3")])],"isStart":true}),makeQuery(id+"F12.opExtrude","CAP_FACE",FACE,{"disambiguationData":[OSD([sQuery(id+"F11.wireOp",EDGE,"E146.3.0"),sQuery(id+"F11.wireOp",EDGE,"E146.3.1"),sQuery(id+"F11.wireOp",EDGE,"E146.3.2"),sQuery(id+"F11.wireOp",EDGE,"E146.3.3")])],"isStart":true}),makeQuery(id+"F12.opExtrude","CAP_FACE",FACE,{"disambiguationData":[OSD([sQuery(id+"F11.wireOp",EDGE,"E146.4.0"),sQuery(id+"F11.wireOp",EDGE,"E146.4.1"),sQuery(id+"F11.wireOp",EDGE,"E146.4.2"),sQuery(id+"F11.wireOp",EDGE,"E146.4.3")])],"isStart":true}),makeQuery(id+"F12.opExtrude","CAP_FACE",FACE,{"disambiguationData":[OSD([sQuery(id+"F11.wireOp",EDGE,"E146.5.0"),sQuery(id+"F11.wireOp",EDGE,"E146.5.1"),sQuery(id+"F11.wireOp",EDGE,"E146.5.2"),sQuery(id+"F11.wireOp",EDGE,"E146.5.3")])],"isStart":true}),makeQuery(id+"F12.opExtrude","CAP_FACE",FACE,{"disambiguationData":[OSD([sQuery(id+"F11.wireOp",EDGE,"E146.6.0"),sQuery(id+"F11.wireOp",EDGE,"E146.6.1"),sQuery(id+"F11.wireOp",EDGE,"E146.6.2"),sQuery(id+"F11.wireOp",EDGE,"E146.6.3")])],"isStart":true}),makeQuery(id+"F12.opExtrude","CAP_FACE",FACE,{"disambiguationData":[OSD([sQuery(id+"F11.wireOp",EDGE,"E146.7.0"),sQuery(id+"F11.wireOp",EDGE,"E146.7.1"),sQuery(id+"F11.wireOp",EDGE,"E146.7.2"),sQuery(id+"F11.wireOp",EDGE,"E146.7.3")])],"isStart":true})]});}
            var sketch = newSketch(context, id + "F14", { "sketchPlane" : qUnion([Q0])});
            skCircle(sketch, "E147", {"center": v(0, 0) * mm, "radius": 4.03 * mm});
            skSolve(sketch);
        }
        {
            var Q0;
            Q0=makeQuery(id+"F14.imprint","IMPRINT",FACE,{"disambiguationData":[TD([[makeQuery(id+"F14.imprint","IMPRINT",EDGE,{"derivedFrom":sQuery(id+"F14.wireOp",EDGE,"E147")}),1.0]])]});
            extrude(context, id + "F15", {"entities" : qUnion([Q0]), "operationType" : NewBodyOperationType.REMOVE, "oppositeDirection" : true, "depth" : 25.4 * mm});
        }
    });
